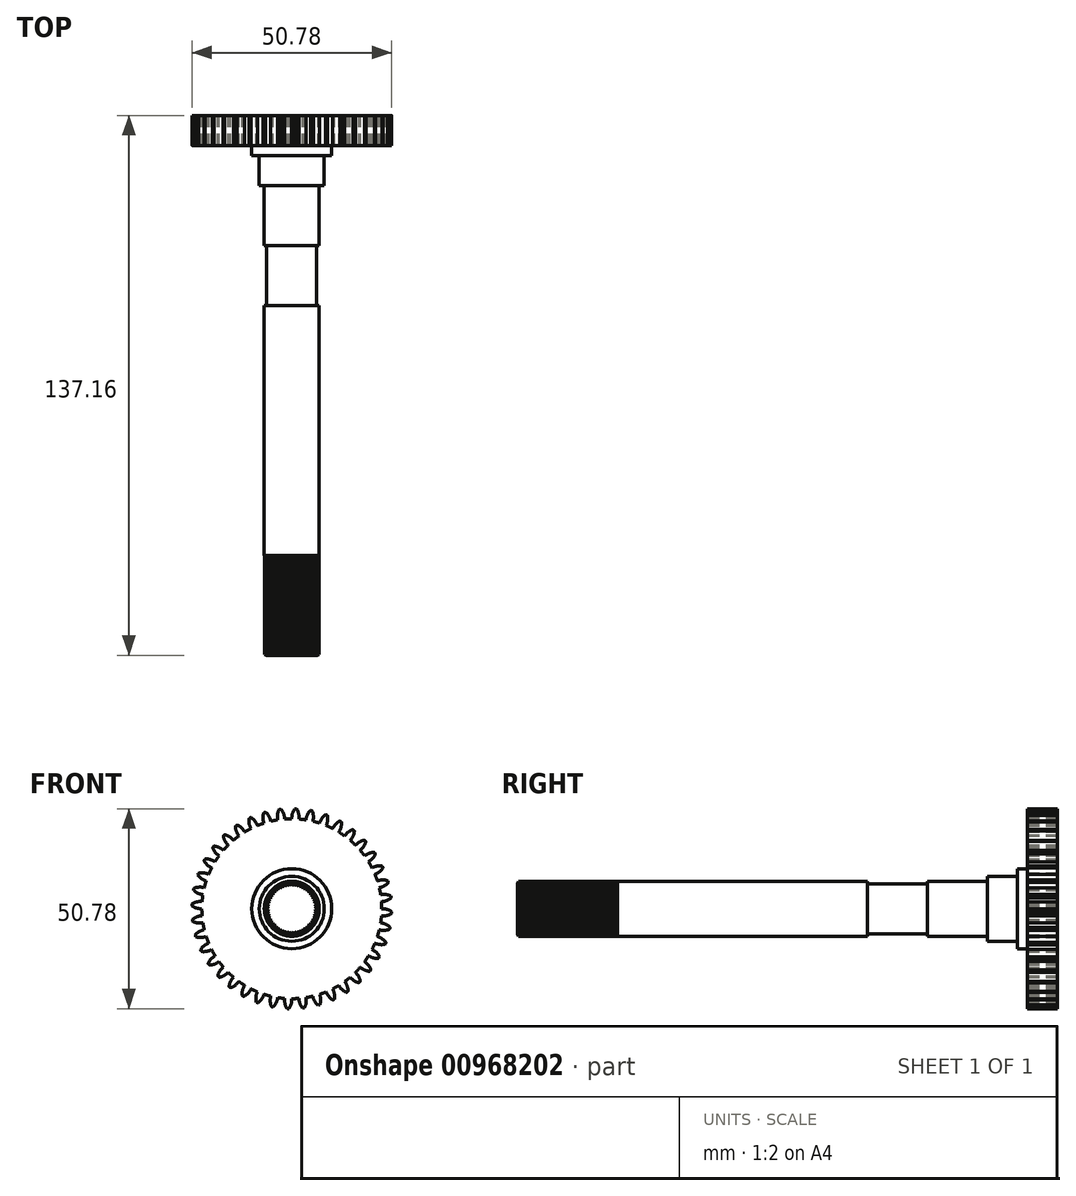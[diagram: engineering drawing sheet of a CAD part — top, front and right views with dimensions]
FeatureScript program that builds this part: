
annotation { "Feature Type Name" : "Feature", "Feature Type Description" : "" }
export const myFeature = defineFeature(function(context is Context, id is Id, definition is map)
    precondition{}
    {
        {
            var Q0;
            Q0=qCreatedBy(makeId("Front.planeOp"),FACE);
            var sketch = newSketch(context, id + "F0", { "sketchPlane" : qUnion([Q0])});
            skArc(sketch, "E0", {"start": v(1.24, 25.37) * mm, "mid": v(1, 25.38) * mm, "end": v(0.75, 25.39) * mm});
            skArc(sketch, "E1", {"start": v(3.58, 22.58) * mm, "mid": v(1.8, 22.79) * mm, "end": v(0, 22.86) * mm});
            skLineSegment(sketch, "E2", {"start": v(0, 0) * mm, "end": v(3.58, 22.58) * mm});
            skLineSegment(sketch, "E3", {"start": v(0, 0) * mm, "end": v(0, 23.2) * mm});
            skLineSegment(sketch, "E4", {"start": v(0, 0) * mm, "end": v(1.82, 23.13) * mm});
            skArc(sketch, "E5", {"start": v(0.75, 25.39) * mm, "mid": v(0.16, 24.19) * mm, "end": v(0, 22.86) * mm});
            skArc(sketch, "E6", {"start": v(1.8, 22.79) * mm, "mid": v(1.73, 24.13) * mm, "end": v(1.24, 25.37) * mm});
            skLineSegment(sketch, "E7.1.0", {"start": v(0, 0) * mm, "end": v(-1.82, 23.13) * mm});
            skLineSegment(sketch, "E7.1.1", {"start": v(0, 0) * mm, "end": v(-3.63, 22.92) * mm});
            skLineSegment(sketch, "E7.1.2", {"start": v(0, 0) * mm, "end": v(0, 22.86) * mm});
            skArc(sketch, "E7.1.3", {"start": v(0, 22.86) * mm, "mid": v(-1.8, 22.79) * mm, "end": v(-3.58, 22.58) * mm});
            skArc(sketch, "E7.1.4", {"start": v(-1.8, 22.79) * mm, "mid": v(-2.06, 24.1) * mm, "end": v(-2.74, 25.25) * mm});
            skArc(sketch, "E7.1.5", {"start": v(-3.23, 25.2) * mm, "mid": v(-3.62, 23.91) * mm, "end": v(-3.58, 22.58) * mm});
            skArc(sketch, "E7.1.6", {"start": v(-2.74, 25.25) * mm, "mid": v(-2.99, 25.22) * mm, "end": v(-3.23, 25.2) * mm});
            skLineSegment(sketch, "E7.2.0", {"start": v(0, 0) * mm, "end": v(-5.42, 22.56) * mm});
            skLineSegment(sketch, "E7.2.1", {"start": v(0, 0) * mm, "end": v(-7.17, 22.07) * mm});
            skLineSegment(sketch, "E7.2.2", {"start": v(0, 0) * mm, "end": v(-3.58, 22.58) * mm});
            skArc(sketch, "E7.2.3", {"start": v(-3.58, 22.58) * mm, "mid": v(-5.34, 22.23) * mm, "end": v(-7.06, 21.74) * mm});
            skArc(sketch, "E7.2.4", {"start": v(-5.34, 22.23) * mm, "mid": v(-5.8, 23.48) * mm, "end": v(-6.66, 24.51) * mm});
            skArc(sketch, "E7.2.5", {"start": v(-7.13, 24.38) * mm, "mid": v(-7.32, 23.05) * mm, "end": v(-7.06, 21.74) * mm});
            skArc(sketch, "E7.2.6", {"start": v(-6.66, 24.51) * mm, "mid": v(-6.9, 24.45) * mm, "end": v(-7.13, 24.38) * mm});
            skLineSegment(sketch, "E7.3.0", {"start": v(0, 0) * mm, "end": v(-8.88, 21.44) * mm});
            skLineSegment(sketch, "E7.3.1", {"start": v(0, 0) * mm, "end": v(-10.53, 20.67) * mm});
            skLineSegment(sketch, "E7.3.2", {"start": v(0, 0) * mm, "end": v(-7.06, 21.74) * mm});
            skArc(sketch, "E7.3.3", {"start": v(-7.06, 21.74) * mm, "mid": v(-8.75, 21.12) * mm, "end": v(-10.38, 20.37) * mm});
            skArc(sketch, "E7.3.4", {"start": v(-8.75, 21.12) * mm, "mid": v(-9.4, 22.28) * mm, "end": v(-10.4, 23.17) * mm});
            skArc(sketch, "E7.3.5", {"start": v(-10.86, 22.96) * mm, "mid": v(-10.83, 21.63) * mm, "end": v(-10.38, 20.37) * mm});
            skArc(sketch, "E7.3.6", {"start": v(-10.4, 23.17) * mm, "mid": v(-10.63, 23.07) * mm, "end": v(-10.86, 22.96) * mm});
            skLineSegment(sketch, "E7.4.0", {"start": v(0, 0) * mm, "end": v(-12.12, 19.78) * mm});
            skLineSegment(sketch, "E7.4.1", {"start": v(0, 0) * mm, "end": v(-13.64, 18.77) * mm});
            skLineSegment(sketch, "E7.4.2", {"start": v(0, 0) * mm, "end": v(-10.38, 20.37) * mm});
            skArc(sketch, "E7.4.3", {"start": v(-10.38, 20.37) * mm, "mid": v(-11.94, 19.5) * mm, "end": v(-13.44, 18.5) * mm});
            skArc(sketch, "E7.4.4", {"start": v(-11.94, 19.5) * mm, "mid": v(-12.78, 20.54) * mm, "end": v(-13.9, 21.26) * mm});
            skArc(sketch, "E7.4.5", {"start": v(-14.32, 20.98) * mm, "mid": v(-14.08, 19.66) * mm, "end": v(-13.44, 18.5) * mm});
            skArc(sketch, "E7.4.6", {"start": v(-13.9, 21.26) * mm, "mid": v(-14.11, 21.12) * mm, "end": v(-14.32, 20.98) * mm});
            skLineSegment(sketch, "E7.5.0", {"start": v(0, 0) * mm, "end": v(-15.07, 17.64) * mm});
            skLineSegment(sketch, "E7.5.1", {"start": v(0, 0) * mm, "end": v(-16.4, 16.4) * mm});
            skLineSegment(sketch, "E7.5.2", {"start": v(0, 0) * mm, "end": v(-13.44, 18.5) * mm});
            skArc(sketch, "E7.5.3", {"start": v(-13.44, 18.5) * mm, "mid": v(-14.85, 17.38) * mm, "end": v(-16.16, 16.16) * mm});
            skArc(sketch, "E7.5.4", {"start": v(-14.85, 17.38) * mm, "mid": v(-15.83, 18.29) * mm, "end": v(-17.06, 18.82) * mm});
            skArc(sketch, "E7.5.5", {"start": v(-17.42, 18.48) * mm, "mid": v(-16.99, 17.22) * mm, "end": v(-16.16, 16.16) * mm});
            skArc(sketch, "E7.5.6", {"start": v(-17.06, 18.82) * mm, "mid": v(-17.24, 18.65) * mm, "end": v(-17.42, 18.48) * mm});
            skLineSegment(sketch, "E7.6.0", {"start": v(0, 0) * mm, "end": v(-17.64, 15.07) * mm});
            skLineSegment(sketch, "E7.6.1", {"start": v(0, 0) * mm, "end": v(-18.77, 13.64) * mm});
            skLineSegment(sketch, "E7.6.2", {"start": v(0, 0) * mm, "end": v(-16.16, 16.16) * mm});
            skArc(sketch, "E7.6.3", {"start": v(-16.16, 16.16) * mm, "mid": v(-17.38, 14.85) * mm, "end": v(-18.5, 13.44) * mm});
            skArc(sketch, "E7.6.4", {"start": v(-17.38, 14.85) * mm, "mid": v(-18.5, 15.58) * mm, "end": v(-19.8, 15.92) * mm});
            skArc(sketch, "E7.6.5", {"start": v(-20.1, 15.53) * mm, "mid": v(-19.47, 14.35) * mm, "end": v(-18.5, 13.44) * mm});
            skArc(sketch, "E7.6.6", {"start": v(-19.8, 15.92) * mm, "mid": v(-19.95, 15.72) * mm, "end": v(-20.1, 15.53) * mm});
            skLineSegment(sketch, "E7.7.0", {"start": v(0, 0) * mm, "end": v(-19.78, 12.12) * mm});
            skLineSegment(sketch, "E7.7.1", {"start": v(0, 0) * mm, "end": v(-20.67, 10.53) * mm});
            skLineSegment(sketch, "E7.7.2", {"start": v(0, 0) * mm, "end": v(-18.5, 13.44) * mm});
            skArc(sketch, "E7.7.3", {"start": v(-18.5, 13.44) * mm, "mid": v(-19.5, 11.94) * mm, "end": v(-20.37, 10.38) * mm});
            skArc(sketch, "E7.7.4", {"start": v(-19.5, 11.94) * mm, "mid": v(-20.7, 12.5) * mm, "end": v(-22.04, 12.63) * mm});
            skArc(sketch, "E7.7.5", {"start": v(-22.28, 12.2) * mm, "mid": v(-21.48, 11.13) * mm, "end": v(-20.37, 10.38) * mm});
            skArc(sketch, "E7.7.6", {"start": v(-22.04, 12.63) * mm, "mid": v(-22.16, 12.41) * mm, "end": v(-22.28, 12.2) * mm});
            skLineSegment(sketch, "E7.8.0", {"start": v(0, 0) * mm, "end": v(-21.44, 8.88) * mm});
            skLineSegment(sketch, "E7.8.1", {"start": v(0, 0) * mm, "end": v(-22.07, 7.17) * mm});
            skLineSegment(sketch, "E7.8.2", {"start": v(0, 0) * mm, "end": v(-20.37, 10.38) * mm});
            skArc(sketch, "E7.8.3", {"start": v(-20.37, 10.38) * mm, "mid": v(-21.12, 8.75) * mm, "end": v(-21.74, 7.06) * mm});
            skArc(sketch, "E7.8.4", {"start": v(-21.12, 8.75) * mm, "mid": v(-22.4, 9.1) * mm, "end": v(-23.74, 9.02) * mm});
            skArc(sketch, "E7.8.5", {"start": v(-23.91, 8.56) * mm, "mid": v(-22.95, 7.63) * mm, "end": v(-21.74, 7.06) * mm});
            skArc(sketch, "E7.8.6", {"start": v(-23.74, 9.02) * mm, "mid": v(-23.83, 8.8) * mm, "end": v(-23.91, 8.56) * mm});
            skLineSegment(sketch, "E7.9.0", {"start": v(0, 0) * mm, "end": v(-22.56, 5.42) * mm});
            skLineSegment(sketch, "E7.9.1", {"start": v(0, 0) * mm, "end": v(-22.92, 3.63) * mm});
            skLineSegment(sketch, "E7.9.2", {"start": v(0, 0) * mm, "end": v(-21.74, 7.06) * mm});
            skArc(sketch, "E7.9.3", {"start": v(-21.74, 7.06) * mm, "mid": v(-22.23, 5.34) * mm, "end": v(-22.58, 3.58) * mm});
            skArc(sketch, "E7.9.4", {"start": v(-22.23, 5.34) * mm, "mid": v(-23.56, 5.49) * mm, "end": v(-24.86, 5.2) * mm});
            skArc(sketch, "E7.9.5", {"start": v(-24.96, 4.71) * mm, "mid": v(-23.86, 3.95) * mm, "end": v(-22.58, 3.58) * mm});
            skArc(sketch, "E7.9.6", {"start": v(-24.86, 5.2) * mm, "mid": v(-24.91, 4.96) * mm, "end": v(-24.96, 4.71) * mm});
            skLineSegment(sketch, "E7.10.0", {"start": v(0, 0) * mm, "end": v(-23.13, 1.82) * mm});
            skLineSegment(sketch, "E7.10.1", {"start": v(0, 0) * mm, "end": v(-23.2, 0) * mm});
            skLineSegment(sketch, "E7.10.2", {"start": v(0, 0) * mm, "end": v(-22.58, 3.58) * mm});
            skArc(sketch, "E7.10.3", {"start": v(-22.58, 3.58) * mm, "mid": v(-22.79, 1.8) * mm, "end": v(-22.86, 0) * mm});
            skArc(sketch, "E7.10.4", {"start": v(-22.79, 1.8) * mm, "mid": v(-24.13, 1.73) * mm, "end": v(-25.37, 1.24) * mm});
            skArc(sketch, "E7.10.5", {"start": v(-25.39, 0.75) * mm, "mid": v(-24.19, 0.16) * mm, "end": v(-22.86, 0) * mm});
            skArc(sketch, "E7.10.6", {"start": v(-25.37, 1.24) * mm, "mid": v(-25.38, 1) * mm, "end": v(-25.39, 0.75) * mm});
            skLineSegment(sketch, "E7.11.0", {"start": v(0, 0) * mm, "end": v(-23.13, -1.82) * mm});
            skLineSegment(sketch, "E7.11.1", {"start": v(0, 0) * mm, "end": v(-22.92, -3.63) * mm});
            skLineSegment(sketch, "E7.11.2", {"start": v(0, 0) * mm, "end": v(-22.86, 0) * mm});
            skArc(sketch, "E7.11.3", {"start": v(-22.86, 0) * mm, "mid": v(-22.79, -1.8) * mm, "end": v(-22.58, -3.58) * mm});
            skArc(sketch, "E7.11.4", {"start": v(-22.79, -1.8) * mm, "mid": v(-24.1, -2.06) * mm, "end": v(-25.25, -2.74) * mm});
            skArc(sketch, "E7.11.5", {"start": v(-25.2, -3.23) * mm, "mid": v(-23.91, -3.62) * mm, "end": v(-22.58, -3.58) * mm});
            skArc(sketch, "E7.11.6", {"start": v(-25.25, -2.74) * mm, "mid": v(-25.22, -2.99) * mm, "end": v(-25.2, -3.23) * mm});
            skLineSegment(sketch, "E7.12.0", {"start": v(0, 0) * mm, "end": v(-22.56, -5.42) * mm});
            skLineSegment(sketch, "E7.12.1", {"start": v(0, 0) * mm, "end": v(-22.07, -7.17) * mm});
            skLineSegment(sketch, "E7.12.2", {"start": v(0, 0) * mm, "end": v(-22.58, -3.58) * mm});
            skArc(sketch, "E7.12.3", {"start": v(-22.58, -3.58) * mm, "mid": v(-22.23, -5.34) * mm, "end": v(-21.74, -7.06) * mm});
            skArc(sketch, "E7.12.4", {"start": v(-22.23, -5.34) * mm, "mid": v(-23.48, -5.8) * mm, "end": v(-24.51, -6.66) * mm});
            skArc(sketch, "E7.12.5", {"start": v(-24.38, -7.13) * mm, "mid": v(-23.05, -7.32) * mm, "end": v(-21.74, -7.06) * mm});
            skArc(sketch, "E7.12.6", {"start": v(-24.51, -6.66) * mm, "mid": v(-24.45, -6.9) * mm, "end": v(-24.38, -7.13) * mm});
            skLineSegment(sketch, "E7.13.0", {"start": v(0, 0) * mm, "end": v(-21.44, -8.88) * mm});
            skLineSegment(sketch, "E7.13.1", {"start": v(0, 0) * mm, "end": v(-20.67, -10.53) * mm});
            skLineSegment(sketch, "E7.13.2", {"start": v(0, 0) * mm, "end": v(-21.74, -7.06) * mm});
            skArc(sketch, "E7.13.3", {"start": v(-21.74, -7.06) * mm, "mid": v(-21.12, -8.75) * mm, "end": v(-20.37, -10.38) * mm});
            skArc(sketch, "E7.13.4", {"start": v(-21.12, -8.75) * mm, "mid": v(-22.28, -9.4) * mm, "end": v(-23.17, -10.4) * mm});
            skArc(sketch, "E7.13.5", {"start": v(-22.96, -10.86) * mm, "mid": v(-21.63, -10.83) * mm, "end": v(-20.37, -10.38) * mm});
            skArc(sketch, "E7.13.6", {"start": v(-23.17, -10.4) * mm, "mid": v(-23.07, -10.63) * mm, "end": v(-22.96, -10.86) * mm});
            skLineSegment(sketch, "E7.14.0", {"start": v(0, 0) * mm, "end": v(-19.78, -12.12) * mm});
            skLineSegment(sketch, "E7.14.1", {"start": v(0, 0) * mm, "end": v(-18.77, -13.64) * mm});
            skLineSegment(sketch, "E7.14.2", {"start": v(0, 0) * mm, "end": v(-20.37, -10.38) * mm});
            skArc(sketch, "E7.14.3", {"start": v(-20.37, -10.38) * mm, "mid": v(-19.5, -11.94) * mm, "end": v(-18.5, -13.44) * mm});
            skArc(sketch, "E7.14.4", {"start": v(-19.5, -11.94) * mm, "mid": v(-20.54, -12.78) * mm, "end": v(-21.26, -13.9) * mm});
            skArc(sketch, "E7.14.5", {"start": v(-20.98, -14.32) * mm, "mid": v(-19.66, -14.08) * mm, "end": v(-18.5, -13.44) * mm});
            skArc(sketch, "E7.14.6", {"start": v(-21.26, -13.9) * mm, "mid": v(-21.12, -14.11) * mm, "end": v(-20.98, -14.32) * mm});
            skLineSegment(sketch, "E7.15.0", {"start": v(0, 0) * mm, "end": v(-17.64, -15.07) * mm});
            skLineSegment(sketch, "E7.15.1", {"start": v(0, 0) * mm, "end": v(-16.4, -16.4) * mm});
            skLineSegment(sketch, "E7.15.2", {"start": v(0, 0) * mm, "end": v(-18.5, -13.44) * mm});
            skArc(sketch, "E7.15.3", {"start": v(-18.5, -13.44) * mm, "mid": v(-17.38, -14.85) * mm, "end": v(-16.16, -16.16) * mm});
            skArc(sketch, "E7.15.4", {"start": v(-17.38, -14.85) * mm, "mid": v(-18.29, -15.83) * mm, "end": v(-18.82, -17.06) * mm});
            skArc(sketch, "E7.15.5", {"start": v(-18.48, -17.42) * mm, "mid": v(-17.22, -16.99) * mm, "end": v(-16.16, -16.16) * mm});
            skArc(sketch, "E7.15.6", {"start": v(-18.82, -17.06) * mm, "mid": v(-18.65, -17.24) * mm, "end": v(-18.48, -17.42) * mm});
            skLineSegment(sketch, "E7.16.0", {"start": v(0, 0) * mm, "end": v(-15.07, -17.64) * mm});
            skLineSegment(sketch, "E7.16.1", {"start": v(0, 0) * mm, "end": v(-13.64, -18.77) * mm});
            skLineSegment(sketch, "E7.16.2", {"start": v(0, 0) * mm, "end": v(-16.16, -16.16) * mm});
            skArc(sketch, "E7.16.3", {"start": v(-16.16, -16.16) * mm, "mid": v(-14.85, -17.38) * mm, "end": v(-13.44, -18.5) * mm});
            skArc(sketch, "E7.16.4", {"start": v(-14.85, -17.38) * mm, "mid": v(-15.58, -18.5) * mm, "end": v(-15.92, -19.8) * mm});
            skArc(sketch, "E7.16.5", {"start": v(-15.53, -20.1) * mm, "mid": v(-14.35, -19.47) * mm, "end": v(-13.44, -18.5) * mm});
            skArc(sketch, "E7.16.6", {"start": v(-15.92, -19.8) * mm, "mid": v(-15.72, -19.95) * mm, "end": v(-15.53, -20.1) * mm});
            skLineSegment(sketch, "E7.17.0", {"start": v(0, 0) * mm, "end": v(-12.12, -19.78) * mm});
            skLineSegment(sketch, "E7.17.1", {"start": v(0, 0) * mm, "end": v(-10.53, -20.67) * mm});
            skLineSegment(sketch, "E7.17.2", {"start": v(0, 0) * mm, "end": v(-13.44, -18.5) * mm});
            skArc(sketch, "E7.17.3", {"start": v(-13.44, -18.5) * mm, "mid": v(-11.94, -19.5) * mm, "end": v(-10.38, -20.37) * mm});
            skArc(sketch, "E7.17.4", {"start": v(-11.94, -19.5) * mm, "mid": v(-12.5, -20.7) * mm, "end": v(-12.63, -22.04) * mm});
            skArc(sketch, "E7.17.5", {"start": v(-12.2, -22.28) * mm, "mid": v(-11.13, -21.48) * mm, "end": v(-10.38, -20.37) * mm});
            skArc(sketch, "E7.17.6", {"start": v(-12.63, -22.04) * mm, "mid": v(-12.41, -22.16) * mm, "end": v(-12.2, -22.28) * mm});
            skLineSegment(sketch, "E7.18.0", {"start": v(0, 0) * mm, "end": v(-8.88, -21.44) * mm});
            skLineSegment(sketch, "E7.18.1", {"start": v(0, 0) * mm, "end": v(-7.17, -22.07) * mm});
            skLineSegment(sketch, "E7.18.2", {"start": v(0, 0) * mm, "end": v(-10.38, -20.37) * mm});
            skArc(sketch, "E7.18.3", {"start": v(-10.38, -20.37) * mm, "mid": v(-8.75, -21.12) * mm, "end": v(-7.06, -21.74) * mm});
            skArc(sketch, "E7.18.4", {"start": v(-8.75, -21.12) * mm, "mid": v(-9.1, -22.4) * mm, "end": v(-9.02, -23.74) * mm});
            skArc(sketch, "E7.18.5", {"start": v(-8.56, -23.91) * mm, "mid": v(-7.63, -22.95) * mm, "end": v(-7.06, -21.74) * mm});
            skArc(sketch, "E7.18.6", {"start": v(-9.02, -23.74) * mm, "mid": v(-8.8, -23.83) * mm, "end": v(-8.56, -23.91) * mm});
            skLineSegment(sketch, "E7.19.0", {"start": v(0, 0) * mm, "end": v(-5.42, -22.56) * mm});
            skLineSegment(sketch, "E7.19.1", {"start": v(0, 0) * mm, "end": v(-3.63, -22.92) * mm});
            skLineSegment(sketch, "E7.19.2", {"start": v(0, 0) * mm, "end": v(-7.06, -21.74) * mm});
            skArc(sketch, "E7.19.3", {"start": v(-7.06, -21.74) * mm, "mid": v(-5.34, -22.23) * mm, "end": v(-3.58, -22.58) * mm});
            skArc(sketch, "E7.19.4", {"start": v(-5.34, -22.23) * mm, "mid": v(-5.49, -23.56) * mm, "end": v(-5.2, -24.86) * mm});
            skArc(sketch, "E7.19.5", {"start": v(-4.71, -24.96) * mm, "mid": v(-3.95, -23.86) * mm, "end": v(-3.58, -22.58) * mm});
            skArc(sketch, "E7.19.6", {"start": v(-5.2, -24.86) * mm, "mid": v(-4.96, -24.91) * mm, "end": v(-4.71, -24.96) * mm});
            skLineSegment(sketch, "E7.20.0", {"start": v(0, 0) * mm, "end": v(-1.82, -23.13) * mm});
            skLineSegment(sketch, "E7.20.1", {"start": v(0, 0) * mm, "end": v(0, -23.2) * mm});
            skLineSegment(sketch, "E7.20.2", {"start": v(0, 0) * mm, "end": v(-3.58, -22.58) * mm});
            skArc(sketch, "E7.20.3", {"start": v(-3.58, -22.58) * mm, "mid": v(-1.8, -22.79) * mm, "end": v(0, -22.86) * mm});
            skArc(sketch, "E7.20.4", {"start": v(-1.8, -22.79) * mm, "mid": v(-1.73, -24.13) * mm, "end": v(-1.24, -25.37) * mm});
            skArc(sketch, "E7.20.5", {"start": v(-0.75, -25.39) * mm, "mid": v(-0.16, -24.19) * mm, "end": v(0, -22.86) * mm});
            skArc(sketch, "E7.20.6", {"start": v(-1.24, -25.37) * mm, "mid": v(-1, -25.38) * mm, "end": v(-0.75, -25.39) * mm});
            skLineSegment(sketch, "E7.21.0", {"start": v(0, 0) * mm, "end": v(1.82, -23.13) * mm});
            skLineSegment(sketch, "E7.21.1", {"start": v(0, 0) * mm, "end": v(3.63, -22.92) * mm});
            skLineSegment(sketch, "E7.21.2", {"start": v(0, 0) * mm, "end": v(0, -22.86) * mm});
            skArc(sketch, "E7.21.3", {"start": v(0, -22.86) * mm, "mid": v(1.8, -22.79) * mm, "end": v(3.58, -22.58) * mm});
            skArc(sketch, "E7.21.4", {"start": v(1.8, -22.79) * mm, "mid": v(2.06, -24.1) * mm, "end": v(2.74, -25.25) * mm});
            skArc(sketch, "E7.21.5", {"start": v(3.23, -25.2) * mm, "mid": v(3.62, -23.91) * mm, "end": v(3.58, -22.58) * mm});
            skArc(sketch, "E7.21.6", {"start": v(2.74, -25.25) * mm, "mid": v(2.99, -25.22) * mm, "end": v(3.23, -25.2) * mm});
            skLineSegment(sketch, "E7.22.0", {"start": v(0, 0) * mm, "end": v(5.42, -22.56) * mm});
            skLineSegment(sketch, "E7.22.1", {"start": v(0, 0) * mm, "end": v(7.17, -22.07) * mm});
            skLineSegment(sketch, "E7.22.2", {"start": v(0, 0) * mm, "end": v(3.58, -22.58) * mm});
            skArc(sketch, "E7.22.3", {"start": v(3.58, -22.58) * mm, "mid": v(5.34, -22.23) * mm, "end": v(7.06, -21.74) * mm});
            skArc(sketch, "E7.22.4", {"start": v(5.34, -22.23) * mm, "mid": v(5.8, -23.48) * mm, "end": v(6.66, -24.51) * mm});
            skArc(sketch, "E7.22.5", {"start": v(7.13, -24.38) * mm, "mid": v(7.32, -23.05) * mm, "end": v(7.06, -21.74) * mm});
            skArc(sketch, "E7.22.6", {"start": v(6.66, -24.51) * mm, "mid": v(6.9, -24.45) * mm, "end": v(7.13, -24.38) * mm});
            skLineSegment(sketch, "E7.23.0", {"start": v(0, 0) * mm, "end": v(8.88, -21.44) * mm});
            skLineSegment(sketch, "E7.23.1", {"start": v(0, 0) * mm, "end": v(10.53, -20.67) * mm});
            skLineSegment(sketch, "E7.23.2", {"start": v(0, 0) * mm, "end": v(7.06, -21.74) * mm});
            skArc(sketch, "E7.23.3", {"start": v(7.06, -21.74) * mm, "mid": v(8.75, -21.12) * mm, "end": v(10.38, -20.37) * mm});
            skArc(sketch, "E7.23.4", {"start": v(8.75, -21.12) * mm, "mid": v(9.4, -22.28) * mm, "end": v(10.4, -23.17) * mm});
            skArc(sketch, "E7.23.5", {"start": v(10.86, -22.96) * mm, "mid": v(10.83, -21.63) * mm, "end": v(10.38, -20.37) * mm});
            skArc(sketch, "E7.23.6", {"start": v(10.4, -23.17) * mm, "mid": v(10.63, -23.07) * mm, "end": v(10.86, -22.96) * mm});
            skLineSegment(sketch, "E7.24.0", {"start": v(0, 0) * mm, "end": v(12.12, -19.78) * mm});
            skLineSegment(sketch, "E7.24.1", {"start": v(0, 0) * mm, "end": v(13.64, -18.77) * mm});
            skLineSegment(sketch, "E7.24.2", {"start": v(0, 0) * mm, "end": v(10.38, -20.37) * mm});
            skArc(sketch, "E7.24.3", {"start": v(10.38, -20.37) * mm, "mid": v(11.94, -19.5) * mm, "end": v(13.44, -18.5) * mm});
            skArc(sketch, "E7.24.4", {"start": v(11.94, -19.5) * mm, "mid": v(12.78, -20.54) * mm, "end": v(13.9, -21.26) * mm});
            skArc(sketch, "E7.24.5", {"start": v(14.32, -20.98) * mm, "mid": v(14.08, -19.66) * mm, "end": v(13.44, -18.5) * mm});
            skArc(sketch, "E7.24.6", {"start": v(13.9, -21.26) * mm, "mid": v(14.11, -21.12) * mm, "end": v(14.32, -20.98) * mm});
            skLineSegment(sketch, "E7.25.0", {"start": v(0, 0) * mm, "end": v(15.07, -17.64) * mm});
            skLineSegment(sketch, "E7.25.1", {"start": v(0, 0) * mm, "end": v(16.4, -16.4) * mm});
            skLineSegment(sketch, "E7.25.2", {"start": v(0, 0) * mm, "end": v(13.44, -18.5) * mm});
            skArc(sketch, "E7.25.3", {"start": v(13.44, -18.5) * mm, "mid": v(14.85, -17.38) * mm, "end": v(16.16, -16.16) * mm});
            skArc(sketch, "E7.25.4", {"start": v(14.85, -17.38) * mm, "mid": v(15.83, -18.29) * mm, "end": v(17.06, -18.82) * mm});
            skArc(sketch, "E7.25.5", {"start": v(17.42, -18.48) * mm, "mid": v(16.99, -17.22) * mm, "end": v(16.16, -16.16) * mm});
            skArc(sketch, "E7.25.6", {"start": v(17.06, -18.82) * mm, "mid": v(17.24, -18.65) * mm, "end": v(17.42, -18.48) * mm});
            skLineSegment(sketch, "E7.26.0", {"start": v(0, 0) * mm, "end": v(17.64, -15.07) * mm});
            skLineSegment(sketch, "E7.26.1", {"start": v(0, 0) * mm, "end": v(18.77, -13.64) * mm});
            skLineSegment(sketch, "E7.26.2", {"start": v(0, 0) * mm, "end": v(16.16, -16.16) * mm});
            skArc(sketch, "E7.26.3", {"start": v(16.16, -16.16) * mm, "mid": v(17.38, -14.85) * mm, "end": v(18.5, -13.44) * mm});
            skArc(sketch, "E7.26.4", {"start": v(17.38, -14.85) * mm, "mid": v(18.5, -15.58) * mm, "end": v(19.8, -15.92) * mm});
            skArc(sketch, "E7.26.5", {"start": v(20.1, -15.53) * mm, "mid": v(19.47, -14.35) * mm, "end": v(18.5, -13.44) * mm});
            skArc(sketch, "E7.26.6", {"start": v(19.8, -15.92) * mm, "mid": v(19.95, -15.72) * mm, "end": v(20.1, -15.53) * mm});
            skLineSegment(sketch, "E7.27.0", {"start": v(0, 0) * mm, "end": v(19.78, -12.12) * mm});
            skLineSegment(sketch, "E7.27.1", {"start": v(0, 0) * mm, "end": v(20.67, -10.53) * mm});
            skLineSegment(sketch, "E7.27.2", {"start": v(0, 0) * mm, "end": v(18.5, -13.44) * mm});
            skArc(sketch, "E7.27.3", {"start": v(18.5, -13.44) * mm, "mid": v(19.5, -11.94) * mm, "end": v(20.37, -10.38) * mm});
            skArc(sketch, "E7.27.4", {"start": v(19.5, -11.94) * mm, "mid": v(20.7, -12.5) * mm, "end": v(22.04, -12.63) * mm});
            skArc(sketch, "E7.27.5", {"start": v(22.28, -12.2) * mm, "mid": v(21.48, -11.13) * mm, "end": v(20.37, -10.38) * mm});
            skArc(sketch, "E7.27.6", {"start": v(22.04, -12.63) * mm, "mid": v(22.16, -12.41) * mm, "end": v(22.28, -12.2) * mm});
            skLineSegment(sketch, "E7.28.0", {"start": v(0, 0) * mm, "end": v(21.44, -8.88) * mm});
            skLineSegment(sketch, "E7.28.1", {"start": v(0, 0) * mm, "end": v(22.07, -7.17) * mm});
            skLineSegment(sketch, "E7.28.2", {"start": v(0, 0) * mm, "end": v(20.37, -10.38) * mm});
            skArc(sketch, "E7.28.3", {"start": v(20.37, -10.38) * mm, "mid": v(21.12, -8.75) * mm, "end": v(21.74, -7.06) * mm});
            skArc(sketch, "E7.28.4", {"start": v(21.12, -8.75) * mm, "mid": v(22.4, -9.1) * mm, "end": v(23.74, -9.02) * mm});
            skArc(sketch, "E7.28.5", {"start": v(23.91, -8.56) * mm, "mid": v(22.95, -7.63) * mm, "end": v(21.74, -7.06) * mm});
            skArc(sketch, "E7.28.6", {"start": v(23.74, -9.02) * mm, "mid": v(23.83, -8.8) * mm, "end": v(23.91, -8.56) * mm});
            skLineSegment(sketch, "E7.29.0", {"start": v(0, 0) * mm, "end": v(22.56, -5.42) * mm});
            skLineSegment(sketch, "E7.29.1", {"start": v(0, 0) * mm, "end": v(22.92, -3.63) * mm});
            skLineSegment(sketch, "E7.29.2", {"start": v(0, 0) * mm, "end": v(21.74, -7.06) * mm});
            skArc(sketch, "E7.29.3", {"start": v(21.74, -7.06) * mm, "mid": v(22.23, -5.34) * mm, "end": v(22.58, -3.58) * mm});
            skArc(sketch, "E7.29.4", {"start": v(22.23, -5.34) * mm, "mid": v(23.56, -5.49) * mm, "end": v(24.86, -5.2) * mm});
            skArc(sketch, "E7.29.5", {"start": v(24.96, -4.71) * mm, "mid": v(23.86, -3.95) * mm, "end": v(22.58, -3.58) * mm});
            skArc(sketch, "E7.29.6", {"start": v(24.86, -5.2) * mm, "mid": v(24.91, -4.96) * mm, "end": v(24.96, -4.71) * mm});
            skLineSegment(sketch, "E7.30.0", {"start": v(0, 0) * mm, "end": v(23.13, -1.82) * mm});
            skLineSegment(sketch, "E7.30.1", {"start": v(0, 0) * mm, "end": v(23.2, 0) * mm});
            skLineSegment(sketch, "E7.30.2", {"start": v(0, 0) * mm, "end": v(22.58, -3.58) * mm});
            skArc(sketch, "E7.30.3", {"start": v(22.58, -3.58) * mm, "mid": v(22.79, -1.8) * mm, "end": v(22.86, 0) * mm});
            skArc(sketch, "E7.30.4", {"start": v(22.79, -1.8) * mm, "mid": v(24.13, -1.73) * mm, "end": v(25.37, -1.24) * mm});
            skArc(sketch, "E7.30.5", {"start": v(25.39, -0.75) * mm, "mid": v(24.19, -0.16) * mm, "end": v(22.86, 0) * mm});
            skArc(sketch, "E7.30.6", {"start": v(25.37, -1.24) * mm, "mid": v(25.38, -1) * mm, "end": v(25.39, -0.75) * mm});
            skLineSegment(sketch, "E7.31.0", {"start": v(0, 0) * mm, "end": v(23.13, 1.82) * mm});
            skLineSegment(sketch, "E7.31.1", {"start": v(0, 0) * mm, "end": v(22.92, 3.63) * mm});
            skLineSegment(sketch, "E7.31.2", {"start": v(0, 0) * mm, "end": v(22.86, 0) * mm});
            skArc(sketch, "E7.31.3", {"start": v(22.86, 0) * mm, "mid": v(22.79, 1.8) * mm, "end": v(22.58, 3.58) * mm});
            skArc(sketch, "E7.31.4", {"start": v(22.79, 1.8) * mm, "mid": v(24.1, 2.06) * mm, "end": v(25.25, 2.74) * mm});
            skArc(sketch, "E7.31.5", {"start": v(25.2, 3.23) * mm, "mid": v(23.91, 3.62) * mm, "end": v(22.58, 3.58) * mm});
            skArc(sketch, "E7.31.6", {"start": v(25.25, 2.74) * mm, "mid": v(25.22, 2.99) * mm, "end": v(25.2, 3.23) * mm});
            skLineSegment(sketch, "E7.32.0", {"start": v(0, 0) * mm, "end": v(22.56, 5.42) * mm});
            skLineSegment(sketch, "E7.32.1", {"start": v(0, 0) * mm, "end": v(22.07, 7.17) * mm});
            skLineSegment(sketch, "E7.32.2", {"start": v(0, 0) * mm, "end": v(22.58, 3.58) * mm});
            skArc(sketch, "E7.32.3", {"start": v(22.58, 3.58) * mm, "mid": v(22.23, 5.34) * mm, "end": v(21.74, 7.06) * mm});
            skArc(sketch, "E7.32.4", {"start": v(22.23, 5.34) * mm, "mid": v(23.48, 5.8) * mm, "end": v(24.51, 6.66) * mm});
            skArc(sketch, "E7.32.5", {"start": v(24.38, 7.13) * mm, "mid": v(23.05, 7.32) * mm, "end": v(21.74, 7.06) * mm});
            skArc(sketch, "E7.32.6", {"start": v(24.51, 6.66) * mm, "mid": v(24.45, 6.9) * mm, "end": v(24.38, 7.13) * mm});
            skLineSegment(sketch, "E7.33.0", {"start": v(0, 0) * mm, "end": v(21.44, 8.88) * mm});
            skLineSegment(sketch, "E7.33.1", {"start": v(0, 0) * mm, "end": v(20.67, 10.53) * mm});
            skLineSegment(sketch, "E7.33.2", {"start": v(0, 0) * mm, "end": v(21.74, 7.06) * mm});
            skArc(sketch, "E7.33.3", {"start": v(21.74, 7.06) * mm, "mid": v(21.12, 8.75) * mm, "end": v(20.37, 10.38) * mm});
            skArc(sketch, "E7.33.4", {"start": v(21.12, 8.75) * mm, "mid": v(22.28, 9.4) * mm, "end": v(23.17, 10.4) * mm});
            skArc(sketch, "E7.33.5", {"start": v(22.96, 10.86) * mm, "mid": v(21.63, 10.83) * mm, "end": v(20.37, 10.38) * mm});
            skArc(sketch, "E7.33.6", {"start": v(23.17, 10.4) * mm, "mid": v(23.07, 10.63) * mm, "end": v(22.96, 10.86) * mm});
            skLineSegment(sketch, "E7.34.0", {"start": v(0, 0) * mm, "end": v(19.78, 12.12) * mm});
            skLineSegment(sketch, "E7.34.1", {"start": v(0, 0) * mm, "end": v(18.77, 13.64) * mm});
            skLineSegment(sketch, "E7.34.2", {"start": v(0, 0) * mm, "end": v(20.37, 10.38) * mm});
            skArc(sketch, "E7.34.3", {"start": v(20.37, 10.38) * mm, "mid": v(19.5, 11.94) * mm, "end": v(18.5, 13.44) * mm});
            skArc(sketch, "E7.34.4", {"start": v(19.5, 11.94) * mm, "mid": v(20.54, 12.78) * mm, "end": v(21.26, 13.9) * mm});
            skArc(sketch, "E7.34.5", {"start": v(20.98, 14.32) * mm, "mid": v(19.66, 14.08) * mm, "end": v(18.5, 13.44) * mm});
            skArc(sketch, "E7.34.6", {"start": v(21.26, 13.9) * mm, "mid": v(21.12, 14.11) * mm, "end": v(20.98, 14.32) * mm});
            skLineSegment(sketch, "E7.35.0", {"start": v(0, 0) * mm, "end": v(17.64, 15.07) * mm});
            skLineSegment(sketch, "E7.35.1", {"start": v(0, 0) * mm, "end": v(16.4, 16.4) * mm});
            skLineSegment(sketch, "E7.35.2", {"start": v(0, 0) * mm, "end": v(18.5, 13.44) * mm});
            skArc(sketch, "E7.35.3", {"start": v(18.5, 13.44) * mm, "mid": v(17.38, 14.85) * mm, "end": v(16.16, 16.16) * mm});
            skArc(sketch, "E7.35.4", {"start": v(17.38, 14.85) * mm, "mid": v(18.29, 15.83) * mm, "end": v(18.82, 17.06) * mm});
            skArc(sketch, "E7.35.5", {"start": v(18.48, 17.42) * mm, "mid": v(17.22, 16.99) * mm, "end": v(16.16, 16.16) * mm});
            skArc(sketch, "E7.35.6", {"start": v(18.82, 17.06) * mm, "mid": v(18.65, 17.24) * mm, "end": v(18.48, 17.42) * mm});
            skLineSegment(sketch, "E7.36.0", {"start": v(0, 0) * mm, "end": v(15.07, 17.64) * mm});
            skLineSegment(sketch, "E7.36.1", {"start": v(0, 0) * mm, "end": v(13.64, 18.77) * mm});
            skLineSegment(sketch, "E7.36.2", {"start": v(0, 0) * mm, "end": v(16.16, 16.16) * mm});
            skArc(sketch, "E7.36.3", {"start": v(16.16, 16.16) * mm, "mid": v(14.85, 17.38) * mm, "end": v(13.44, 18.5) * mm});
            skArc(sketch, "E7.36.4", {"start": v(14.85, 17.38) * mm, "mid": v(15.58, 18.5) * mm, "end": v(15.92, 19.8) * mm});
            skArc(sketch, "E7.36.5", {"start": v(15.53, 20.1) * mm, "mid": v(14.35, 19.47) * mm, "end": v(13.44, 18.5) * mm});
            skArc(sketch, "E7.36.6", {"start": v(15.92, 19.8) * mm, "mid": v(15.72, 19.95) * mm, "end": v(15.53, 20.1) * mm});
            skLineSegment(sketch, "E7.37.0", {"start": v(0, 0) * mm, "end": v(12.12, 19.78) * mm});
            skLineSegment(sketch, "E7.37.1", {"start": v(0, 0) * mm, "end": v(10.53, 20.67) * mm});
            skLineSegment(sketch, "E7.37.2", {"start": v(0, 0) * mm, "end": v(13.44, 18.5) * mm});
            skArc(sketch, "E7.37.3", {"start": v(13.44, 18.5) * mm, "mid": v(11.94, 19.5) * mm, "end": v(10.38, 20.37) * mm});
            skArc(sketch, "E7.37.4", {"start": v(11.94, 19.5) * mm, "mid": v(12.5, 20.7) * mm, "end": v(12.63, 22.04) * mm});
            skArc(sketch, "E7.37.5", {"start": v(12.2, 22.28) * mm, "mid": v(11.13, 21.48) * mm, "end": v(10.38, 20.37) * mm});
            skArc(sketch, "E7.37.6", {"start": v(12.63, 22.04) * mm, "mid": v(12.41, 22.16) * mm, "end": v(12.2, 22.28) * mm});
            skLineSegment(sketch, "E7.38.0", {"start": v(0, 0) * mm, "end": v(8.88, 21.44) * mm});
            skLineSegment(sketch, "E7.38.1", {"start": v(0, 0) * mm, "end": v(7.17, 22.07) * mm});
            skLineSegment(sketch, "E7.38.2", {"start": v(0, 0) * mm, "end": v(10.38, 20.37) * mm});
            skArc(sketch, "E7.38.3", {"start": v(10.38, 20.37) * mm, "mid": v(8.75, 21.12) * mm, "end": v(7.06, 21.74) * mm});
            skArc(sketch, "E7.38.4", {"start": v(8.75, 21.12) * mm, "mid": v(9.1, 22.4) * mm, "end": v(9.02, 23.74) * mm});
            skArc(sketch, "E7.38.5", {"start": v(8.56, 23.91) * mm, "mid": v(7.63, 22.95) * mm, "end": v(7.06, 21.74) * mm});
            skArc(sketch, "E7.38.6", {"start": v(9.02, 23.74) * mm, "mid": v(8.8, 23.83) * mm, "end": v(8.56, 23.91) * mm});
            skLineSegment(sketch, "E7.39.0", {"start": v(0, 0) * mm, "end": v(5.42, 22.56) * mm});
            skLineSegment(sketch, "E7.39.1", {"start": v(0, 0) * mm, "end": v(3.63, 22.92) * mm});
            skLineSegment(sketch, "E7.39.2", {"start": v(0, 0) * mm, "end": v(7.06, 21.74) * mm});
            skArc(sketch, "E7.39.3", {"start": v(7.06, 21.74) * mm, "mid": v(5.34, 22.23) * mm, "end": v(3.58, 22.58) * mm});
            skArc(sketch, "E7.39.4", {"start": v(5.34, 22.23) * mm, "mid": v(5.49, 23.56) * mm, "end": v(5.2, 24.86) * mm});
            skArc(sketch, "E7.39.5", {"start": v(4.71, 24.96) * mm, "mid": v(3.95, 23.86) * mm, "end": v(3.58, 22.58) * mm});
            skArc(sketch, "E7.39.6", {"start": v(5.2, 24.86) * mm, "mid": v(4.96, 24.91) * mm, "end": v(4.71, 24.96) * mm});
            skSolve(sketch);
        }
        {
            var Q0;
            {var subQ0=sQuery(id+"F0.wireOp",EDGE,"E7.39.0");var subQ1=sQuery(id+"F0.wireOp",EDGE,"E7.38.1");var subQ2=sQuery(id+"F0.wireOp",EDGE,"E7.38.0");var subQ3=sQuery(id+"F0.wireOp",EDGE,"E7.37.1");var subQ4=sQuery(id+"F0.wireOp",EDGE,"E7.37.0");var subQ5=sQuery(id+"F0.wireOp",EDGE,"E7.36.1");var subQ6=sQuery(id+"F0.wireOp",EDGE,"E7.36.0");var subQ7=sQuery(id+"F0.wireOp",EDGE,"E7.35.1");var subQ8=sQuery(id+"F0.wireOp",EDGE,"E7.35.0");var subQ9=sQuery(id+"F0.wireOp",EDGE,"E7.34.1");var subQ10=sQuery(id+"F0.wireOp",EDGE,"E7.34.0");var subQ11=sQuery(id+"F0.wireOp",EDGE,"E7.33.1");var subQ12=sQuery(id+"F0.wireOp",EDGE,"E7.33.0");var subQ13=sQuery(id+"F0.wireOp",EDGE,"E7.32.1");var subQ14=sQuery(id+"F0.wireOp",EDGE,"E7.32.0");var subQ15=sQuery(id+"F0.wireOp",EDGE,"E7.31.1");var subQ16=sQuery(id+"F0.wireOp",EDGE,"E7.31.0");var subQ17=sQuery(id+"F0.wireOp",EDGE,"E7.30.1");var subQ18=sQuery(id+"F0.wireOp",EDGE,"E7.30.0");var subQ19=sQuery(id+"F0.wireOp",EDGE,"E7.29.1");var subQ20=sQuery(id+"F0.wireOp",EDGE,"E7.29.0");var subQ21=sQuery(id+"F0.wireOp",EDGE,"E7.28.1");var subQ22=sQuery(id+"F0.wireOp",EDGE,"E7.28.0");var subQ23=sQuery(id+"F0.wireOp",EDGE,"E7.27.1");var subQ24=sQuery(id+"F0.wireOp",EDGE,"E7.27.0");var subQ25=sQuery(id+"F0.wireOp",EDGE,"E7.26.1");var subQ26=sQuery(id+"F0.wireOp",EDGE,"E7.26.0");var subQ27=sQuery(id+"F0.wireOp",EDGE,"E7.25.1");var subQ28=sQuery(id+"F0.wireOp",EDGE,"E7.25.0");var subQ29=sQuery(id+"F0.wireOp",EDGE,"E7.24.1");var subQ30=sQuery(id+"F0.wireOp",EDGE,"E7.24.0");var subQ31=sQuery(id+"F0.wireOp",EDGE,"E7.23.1");var subQ32=sQuery(id+"F0.wireOp",EDGE,"E7.23.0");var subQ33=sQuery(id+"F0.wireOp",EDGE,"E7.22.1");var subQ34=sQuery(id+"F0.wireOp",EDGE,"E7.22.0");var subQ35=sQuery(id+"F0.wireOp",EDGE,"E7.21.1");var subQ36=sQuery(id+"F0.wireOp",EDGE,"E7.21.0");var subQ37=sQuery(id+"F0.wireOp",EDGE,"E7.20.1");var subQ38=sQuery(id+"F0.wireOp",EDGE,"E7.20.0");var subQ39=sQuery(id+"F0.wireOp",EDGE,"E7.19.1");var subQ40=sQuery(id+"F0.wireOp",EDGE,"E7.19.0");var subQ41=sQuery(id+"F0.wireOp",EDGE,"E7.18.1");var subQ42=sQuery(id+"F0.wireOp",EDGE,"E7.18.0");var subQ43=sQuery(id+"F0.wireOp",EDGE,"E7.17.1");var subQ44=sQuery(id+"F0.wireOp",EDGE,"E7.17.0");var subQ45=sQuery(id+"F0.wireOp",EDGE,"E7.16.1");var subQ46=sQuery(id+"F0.wireOp",EDGE,"E7.16.0");var subQ47=sQuery(id+"F0.wireOp",EDGE,"E7.15.1");var subQ48=sQuery(id+"F0.wireOp",EDGE,"E7.15.0");var subQ49=sQuery(id+"F0.wireOp",EDGE,"E7.14.1");var subQ50=sQuery(id+"F0.wireOp",EDGE,"E7.14.0");var subQ51=sQuery(id+"F0.wireOp",EDGE,"E7.13.1");var subQ52=sQuery(id+"F0.wireOp",EDGE,"E7.13.0");var subQ53=sQuery(id+"F0.wireOp",EDGE,"E7.12.1");var subQ54=sQuery(id+"F0.wireOp",EDGE,"E7.12.0");var subQ55=sQuery(id+"F0.wireOp",EDGE,"E7.11.1");var subQ56=sQuery(id+"F0.wireOp",EDGE,"E7.11.0");var subQ57=sQuery(id+"F0.wireOp",EDGE,"E7.10.1");var subQ58=sQuery(id+"F0.wireOp",EDGE,"E7.10.0");var subQ59=sQuery(id+"F0.wireOp",EDGE,"E7.9.1");var subQ60=sQuery(id+"F0.wireOp",EDGE,"E7.9.0");var subQ61=sQuery(id+"F0.wireOp",EDGE,"E7.8.1");var subQ62=sQuery(id+"F0.wireOp",EDGE,"E7.8.0");var subQ63=sQuery(id+"F0.wireOp",EDGE,"E7.7.1");var subQ64=sQuery(id+"F0.wireOp",EDGE,"E7.7.0");var subQ65=sQuery(id+"F0.wireOp",EDGE,"E7.6.1");var subQ66=sQuery(id+"F0.wireOp",EDGE,"E7.6.0");var subQ67=sQuery(id+"F0.wireOp",EDGE,"E7.5.1");var subQ68=sQuery(id+"F0.wireOp",EDGE,"E7.5.0");var subQ69=sQuery(id+"F0.wireOp",EDGE,"E7.4.1");var subQ70=sQuery(id+"F0.wireOp",EDGE,"E7.4.0");var subQ71=sQuery(id+"F0.wireOp",EDGE,"E7.3.1");var subQ72=sQuery(id+"F0.wireOp",EDGE,"E7.3.0");var subQ73=sQuery(id+"F0.wireOp",EDGE,"E7.2.1");var subQ74=sQuery(id+"F0.wireOp",EDGE,"E7.2.0");var subQ75=sQuery(id+"F0.wireOp",EDGE,"E7.1.1");var subQ76=sQuery(id+"F0.wireOp",EDGE,"E7.1.0");var subQ77=sQuery(id+"F0.wireOp",EDGE,"E4");var subQ78=sQuery(id+"F0.wireOp",EDGE,"E3");var subQ79=sQuery(id+"F0.wireOp",EDGE,"E2");var subQ81=sQuery(id+"F0.wireOp",EDGE,"E7.27.4");var subQ82=sQuery(id+"F0.wireOp",EDGE,"E7.27.3");var subQ83=makeQuery(id+"F0.imprint","INTERSECT",VERTEX,{"derivedFrom":[subQ24,subQ82,subQ81]});var subQ85=sQuery(id+"F0.wireOp",EDGE,"E7.28.3");var subQ86=sQuery(id+"F0.wireOp",EDGE,"E7.27.5");var subQ88=makeQuery(id+"F0.imprint","IMPRINT",EDGE,{"disambiguationData":[TD([[subQ83,-1.0]])],"derivedFrom":subQ82});var subQ90=sQuery(id+"F0.wireOp",EDGE,"E7.35.4");var subQ91=sQuery(id+"F0.wireOp",EDGE,"E7.35.3");var subQ92=makeQuery(id+"F0.imprint","INTERSECT",VERTEX,{"derivedFrom":[subQ8,subQ91,subQ90]});var subQ94=sQuery(id+"F0.wireOp",EDGE,"E7.36.3");var subQ95=sQuery(id+"F0.wireOp",EDGE,"E7.35.5");var subQ97=makeQuery(id+"F0.imprint","IMPRINT",EDGE,{"disambiguationData":[TD([[subQ92,-1.0]])],"derivedFrom":subQ91});var subQ99=sQuery(id+"F0.wireOp",EDGE,"E7.8.4");var subQ100=sQuery(id+"F0.wireOp",EDGE,"E7.8.3");var subQ101=makeQuery(id+"F0.imprint","INTERSECT",VERTEX,{"derivedFrom":[subQ62,subQ100,subQ99]});var subQ103=sQuery(id+"F0.wireOp",EDGE,"E7.9.3");var subQ104=sQuery(id+"F0.wireOp",EDGE,"E7.8.5");var subQ106=makeQuery(id+"F0.imprint","IMPRINT",EDGE,{"disambiguationData":[TD([[subQ101,-1.0]])],"derivedFrom":subQ100});var subQ108=sQuery(id+"F0.wireOp",EDGE,"E7.31.3");var subQ109=sQuery(id+"F0.wireOp",EDGE,"E7.30.5");var subQ110=sQuery(id+"F0.wireOp",EDGE,"E7.30.3");var subQ113=sQuery(id+"F0.wireOp",EDGE,"E7.31.4");var subQ114=makeQuery(id+"F0.imprint","INTERSECT",VERTEX,{"derivedFrom":[subQ16,subQ108,subQ113]});var subQ116=sQuery(id+"F0.wireOp",EDGE,"E7.16.4");var subQ117=sQuery(id+"F0.wireOp",EDGE,"E7.16.3");var subQ118=makeQuery(id+"F0.imprint","INTERSECT",VERTEX,{"derivedFrom":[subQ46,subQ117,subQ116]});var subQ120=sQuery(id+"F0.wireOp",EDGE,"E7.17.3");var subQ121=sQuery(id+"F0.wireOp",EDGE,"E7.16.5");var subQ123=makeQuery(id+"F0.imprint","IMPRINT",EDGE,{"disambiguationData":[TD([[subQ118,-1.0]])],"derivedFrom":subQ117});var subQ125=sQuery(id+"F0.wireOp",EDGE,"E7.3.4");var subQ126=sQuery(id+"F0.wireOp",EDGE,"E7.3.3");var subQ127=makeQuery(id+"F0.imprint","INTERSECT",VERTEX,{"derivedFrom":[subQ72,subQ126,subQ125]});var subQ129=sQuery(id+"F0.wireOp",EDGE,"E7.4.3");var subQ130=sQuery(id+"F0.wireOp",EDGE,"E7.3.5");var subQ132=makeQuery(id+"F0.imprint","IMPRINT",EDGE,{"disambiguationData":[TD([[subQ127,-1.0]])],"derivedFrom":subQ126});var subQ134=sQuery(id+"F0.wireOp",EDGE,"E7.24.4");var subQ135=sQuery(id+"F0.wireOp",EDGE,"E7.24.3");var subQ136=makeQuery(id+"F0.imprint","INTERSECT",VERTEX,{"derivedFrom":[subQ30,subQ135,subQ134]});var subQ138=sQuery(id+"F0.wireOp",EDGE,"E7.25.3");var subQ139=sQuery(id+"F0.wireOp",EDGE,"E7.24.5");var subQ141=makeQuery(id+"F0.imprint","IMPRINT",EDGE,{"disambiguationData":[TD([[subQ136,-1.0]])],"derivedFrom":subQ135});var subQ143=sQuery(id+"F0.wireOp",EDGE,"E7.11.4");var subQ144=sQuery(id+"F0.wireOp",EDGE,"E7.11.3");var subQ145=makeQuery(id+"F0.imprint","INTERSECT",VERTEX,{"derivedFrom":[subQ56,subQ144,subQ143]});var subQ147=sQuery(id+"F0.wireOp",EDGE,"E7.12.3");var subQ148=sQuery(id+"F0.wireOp",EDGE,"E7.11.5");var subQ150=makeQuery(id+"F0.imprint","IMPRINT",EDGE,{"disambiguationData":[TD([[subQ145,-1.0]])],"derivedFrom":subQ144});var subQ152=sQuery(id+"F0.wireOp",EDGE,"E7.32.4");var subQ153=sQuery(id+"F0.wireOp",EDGE,"E7.32.3");var subQ154=makeQuery(id+"F0.imprint","INTERSECT",VERTEX,{"derivedFrom":[subQ14,subQ153,subQ152]});var subQ156=sQuery(id+"F0.wireOp",EDGE,"E7.33.3");var subQ157=sQuery(id+"F0.wireOp",EDGE,"E7.32.5");var subQ159=makeQuery(id+"F0.imprint","IMPRINT",EDGE,{"disambiguationData":[TD([[subQ154,-1.0]])],"derivedFrom":subQ153});var subQ161=sQuery(id+"F0.wireOp",EDGE,"E7.19.4");var subQ162=sQuery(id+"F0.wireOp",EDGE,"E7.19.3");var subQ163=makeQuery(id+"F0.imprint","INTERSECT",VERTEX,{"derivedFrom":[subQ40,subQ162,subQ161]});var subQ165=sQuery(id+"F0.wireOp",EDGE,"E7.20.3");var subQ166=sQuery(id+"F0.wireOp",EDGE,"E7.19.5");var subQ168=makeQuery(id+"F0.imprint","IMPRINT",EDGE,{"disambiguationData":[TD([[subQ163,-1.0]])],"derivedFrom":subQ162});var subQ170=sQuery(id+"F0.wireOp",EDGE,"E7.36.5");var subQ171=makeQuery(id+"F0.imprint","INTERSECT",VERTEX,{"derivedFrom":[subQ5,subQ170]});var subQ172=sQuery(id+"F0.wireOp",EDGE,"E7.37.3");var subQ174=makeQuery(id+"F0.imprint","IMPRINT",EDGE,{"disambiguationData":[TD([[subQ171,1.0]])],"derivedFrom":subQ5});var subQ175=sQuery(id+"F0.wireOp",EDGE,"E7.23.5");var subQ176=makeQuery(id+"F0.imprint","INTERSECT",VERTEX,{"derivedFrom":[subQ31,subQ175]});var subQ177=sQuery(id+"F0.wireOp",EDGE,"E7.23.3");var subQ179=makeQuery(id+"F0.imprint","IMPRINT",EDGE,{"disambiguationData":[TD([[subQ176,1.0]])],"derivedFrom":subQ31});var subQ180=sQuery(id+"F0.wireOp",EDGE,"E7.9.4");var subQ181=makeQuery(id+"F0.imprint","INTERSECT",VERTEX,{"derivedFrom":[subQ60,subQ103,subQ180]});var subQ183=sQuery(id+"F0.wireOp",EDGE,"E7.31.5");var subQ184=makeQuery(id+"F0.imprint","INTERSECT",VERTEX,{"derivedFrom":[subQ15,subQ183]});var subQ186=makeQuery(id+"F0.imprint","IMPRINT",EDGE,{"disambiguationData":[TD([[subQ184,1.0]])],"derivedFrom":subQ15});var subQ187=sQuery(id+"F0.wireOp",EDGE,"E7.25.4");var subQ188=makeQuery(id+"F0.imprint","INTERSECT",VERTEX,{"derivedFrom":[subQ28,subQ138,subQ187]});var subQ190=sQuery(id+"F0.wireOp",EDGE,"E7.39.1");var subQ191=makeQuery(id+"F0.imprint","IMPRINT",EDGE,{"derivedFrom":subQ190});var subQ193=sQuery(id+"F0.wireOp",EDGE,"E7.39.3");var subQ194=sQuery(id+"F0.wireOp",EDGE,"E1");var subQ197=sQuery(id+"F0.wireOp",EDGE,"E7.1.3");var subQ198=sQuery(id+"F0.wireOp",EDGE,"E5");var subQ200=sQuery(id+"F0.wireOp",EDGE,"E6");var subQ201=makeQuery(id+"F0.imprint","INTERSECT",VERTEX,{"derivedFrom":[subQ194,subQ77,subQ200]});var subQ202=makeQuery(id+"F0.imprint","IMPRINT",EDGE,{"disambiguationData":[TD([[subQ201,-1.0]])],"derivedFrom":subQ194});var subQ205=sQuery(id+"F0.wireOp",EDGE,"E7.15.3");var subQ206=sQuery(id+"F0.wireOp",EDGE,"E7.14.5");var subQ207=sQuery(id+"F0.wireOp",EDGE,"E7.14.3");var subQ210=sQuery(id+"F0.wireOp",EDGE,"E7.15.4");var subQ211=makeQuery(id+"F0.imprint","INTERSECT",VERTEX,{"derivedFrom":[subQ48,subQ205,subQ210]});var subQ213=sQuery(id+"F0.wireOp",EDGE,"E7.12.5");var subQ214=makeQuery(id+"F0.imprint","INTERSECT",VERTEX,{"derivedFrom":[subQ53,subQ213]});var subQ215=sQuery(id+"F0.wireOp",EDGE,"E7.13.3");var subQ217=makeQuery(id+"F0.imprint","IMPRINT",EDGE,{"disambiguationData":[TD([[subQ214,1.0]])],"derivedFrom":subQ53});var subQ218=sQuery(id+"F0.wireOp",EDGE,"E7.20.5");var subQ219=makeQuery(id+"F0.imprint","INTERSECT",VERTEX,{"derivedFrom":[subQ37,subQ218]});var subQ220=sQuery(id+"F0.wireOp",EDGE,"E7.21.3");var subQ222=makeQuery(id+"F0.imprint","IMPRINT",EDGE,{"disambiguationData":[TD([[subQ219,1.0]])],"derivedFrom":subQ37});var subQ223=sQuery(id+"F0.wireOp",EDGE,"E7.28.5");var subQ224=makeQuery(id+"F0.imprint","INTERSECT",VERTEX,{"derivedFrom":[subQ21,subQ223]});var subQ225=sQuery(id+"F0.wireOp",EDGE,"E7.29.3");var subQ227=makeQuery(id+"F0.imprint","IMPRINT",EDGE,{"disambiguationData":[TD([[subQ224,1.0]])],"derivedFrom":subQ21});var subQ228=sQuery(id+"F0.wireOp",EDGE,"E7.15.5");var subQ229=makeQuery(id+"F0.imprint","INTERSECT",VERTEX,{"derivedFrom":[subQ47,subQ228]});var subQ231=makeQuery(id+"F0.imprint","IMPRINT",EDGE,{"disambiguationData":[TD([[subQ229,1.0]])],"derivedFrom":subQ47});var subQ232=sQuery(id+"F0.wireOp",EDGE,"E7.20.4");var subQ233=makeQuery(id+"F0.imprint","INTERSECT",VERTEX,{"derivedFrom":[subQ38,subQ232]});var subQ234=sQuery(id+"F0.wireOp",EDGE,"E7.20.6");var subQ235=makeQuery(id+"F0.imprint","INTERSECT",VERTEX,{"derivedFrom":[subQ38,subQ165,subQ232]});var subQ236=makeQuery(id+"F0.imprint","IMPRINT",EDGE,{"disambiguationData":[TD([[subQ235,-1.0]])],"derivedFrom":subQ165});var subQ237=makeQuery(id+"F0.imprint","IMPRINT",EDGE,{"disambiguationData":[TD([[subQ233,1.0]])],"derivedFrom":subQ38});var subQ238=sQuery(id+"F0.wireOp",EDGE,"E7.28.4");var subQ239=makeQuery(id+"F0.imprint","INTERSECT",VERTEX,{"derivedFrom":[subQ22,subQ238]});var subQ240=sQuery(id+"F0.wireOp",EDGE,"E7.28.6");var subQ241=makeQuery(id+"F0.imprint","INTERSECT",VERTEX,{"derivedFrom":[subQ22,subQ85,subQ238]});var subQ242=makeQuery(id+"F0.imprint","IMPRINT",EDGE,{"disambiguationData":[TD([[subQ241,-1.0]])],"derivedFrom":subQ85});var subQ243=makeQuery(id+"F0.imprint","IMPRINT",EDGE,{"disambiguationData":[TD([[subQ239,1.0]])],"derivedFrom":subQ22});var subQ244=sQuery(id+"F0.wireOp",EDGE,"E7.36.4");var subQ245=makeQuery(id+"F0.imprint","INTERSECT",VERTEX,{"derivedFrom":[subQ6,subQ244]});var subQ246=sQuery(id+"F0.wireOp",EDGE,"E7.36.6");var subQ247=makeQuery(id+"F0.imprint","INTERSECT",VERTEX,{"derivedFrom":[subQ6,subQ94,subQ244]});var subQ248=makeQuery(id+"F0.imprint","IMPRINT",EDGE,{"disambiguationData":[TD([[subQ247,-1.0]])],"derivedFrom":subQ94});var subQ249=makeQuery(id+"F0.imprint","IMPRINT",EDGE,{"disambiguationData":[TD([[subQ245,1.0]])],"derivedFrom":subQ6});var subQ250=sQuery(id+"F0.wireOp",EDGE,"E7.18.3");var subQ251=sQuery(id+"F0.wireOp",EDGE,"E7.17.5");var subQ254=sQuery(id+"F0.wireOp",EDGE,"E7.18.4");var subQ255=makeQuery(id+"F0.imprint","INTERSECT",VERTEX,{"derivedFrom":[subQ42,subQ250,subQ254]});var subQ257=sQuery(id+"F0.wireOp",EDGE,"E7.34.3");var subQ258=sQuery(id+"F0.wireOp",EDGE,"E7.33.5");var subQ261=sQuery(id+"F0.wireOp",EDGE,"E7.34.4");var subQ262=makeQuery(id+"F0.imprint","INTERSECT",VERTEX,{"derivedFrom":[subQ10,subQ257,subQ261]});var subQ264=sQuery(id+"F0.wireOp",EDGE,"E7.4.4");var subQ265=makeQuery(id+"F0.imprint","INTERSECT",VERTEX,{"derivedFrom":[subQ70,subQ264]});var subQ266=sQuery(id+"F0.wireOp",EDGE,"E7.4.6");var subQ267=sQuery(id+"F0.wireOp",EDGE,"E7.5.3");var subQ268=sQuery(id+"F0.wireOp",EDGE,"E7.4.5");var subQ270=makeQuery(id+"F0.imprint","INTERSECT",VERTEX,{"derivedFrom":[subQ70,subQ129,subQ264]});var subQ271=makeQuery(id+"F0.imprint","IMPRINT",EDGE,{"disambiguationData":[TD([[subQ270,-1.0]])],"derivedFrom":subQ129});var subQ272=makeQuery(id+"F0.imprint","INTERSECT",VERTEX,{"derivedFrom":[subQ69,subQ268]});var subQ273=makeQuery(id+"F0.imprint","IMPRINT",EDGE,{"disambiguationData":[TD([[subQ272,1.0]])],"derivedFrom":subQ69});var subQ274=makeQuery(id+"F0.imprint","IMPRINT",EDGE,{"disambiguationData":[TD([[subQ265,1.0]])],"derivedFrom":subQ70});var subQ275=sQuery(id+"F0.wireOp",EDGE,"E7.12.4");var subQ276=makeQuery(id+"F0.imprint","INTERSECT",VERTEX,{"derivedFrom":[subQ54,subQ275]});var subQ277=sQuery(id+"F0.wireOp",EDGE,"E7.12.6");var subQ278=makeQuery(id+"F0.imprint","INTERSECT",VERTEX,{"derivedFrom":[subQ54,subQ147,subQ275]});var subQ279=makeQuery(id+"F0.imprint","IMPRINT",EDGE,{"disambiguationData":[TD([[subQ278,-1.0]])],"derivedFrom":subQ147});var subQ280=makeQuery(id+"F0.imprint","IMPRINT",EDGE,{"disambiguationData":[TD([[subQ276,1.0]])],"derivedFrom":subQ54});var subQ281=sQuery(id+"F0.wireOp",EDGE,"E7.17.4");var subQ282=makeQuery(id+"F0.imprint","INTERSECT",VERTEX,{"derivedFrom":[subQ44,subQ281]});var subQ283=makeQuery(id+"F0.imprint","INTERSECT",VERTEX,{"derivedFrom":[subQ44,subQ120,subQ281]});var subQ284=makeQuery(id+"F0.imprint","IMPRINT",EDGE,{"disambiguationData":[TD([[subQ282,1.0]])],"derivedFrom":subQ44});var subQ285=makeQuery(id+"F0.imprint","INTERSECT",VERTEX,{"derivedFrom":[subQ28,subQ187]});var subQ286=makeQuery(id+"F0.imprint","IMPRINT",EDGE,{"disambiguationData":[TD([[subQ285,1.0]])],"derivedFrom":subQ28});var subQ287=sQuery(id+"F0.wireOp",EDGE,"E7.33.4");var subQ288=makeQuery(id+"F0.imprint","INTERSECT",VERTEX,{"derivedFrom":[subQ12,subQ287]});var subQ289=makeQuery(id+"F0.imprint","INTERSECT",VERTEX,{"derivedFrom":[subQ12,subQ156,subQ287]});var subQ290=makeQuery(id+"F0.imprint","IMPRINT",EDGE,{"disambiguationData":[TD([[subQ288,1.0]])],"derivedFrom":subQ12});var subQ291=sQuery(id+"F0.wireOp",EDGE,"E7.2.3");var subQ292=sQuery(id+"F0.wireOp",EDGE,"E7.1.5");var subQ295=sQuery(id+"F0.wireOp",EDGE,"E7.2.4");var subQ296=makeQuery(id+"F0.imprint","INTERSECT",VERTEX,{"derivedFrom":[subQ74,subQ291,subQ295]});var subQ298=makeQuery(id+"F0.imprint","INTERSECT",VERTEX,{"derivedFrom":[subQ60,subQ180]});var subQ299=makeQuery(id+"F0.imprint","IMPRINT",EDGE,{"disambiguationData":[TD([[subQ298,1.0]])],"derivedFrom":subQ60});var subQ300=sQuery(id+"F0.wireOp",EDGE,"E7.7.4");var subQ301=makeQuery(id+"F0.imprint","INTERSECT",VERTEX,{"derivedFrom":[subQ64,subQ300]});var subQ302=sQuery(id+"F0.wireOp",EDGE,"E7.7.6");var subQ303=sQuery(id+"F0.wireOp",EDGE,"E7.7.5");var subQ304=sQuery(id+"F0.wireOp",EDGE,"E7.7.3");var subQ306=makeQuery(id+"F0.imprint","INTERSECT",VERTEX,{"derivedFrom":[subQ64,subQ304,subQ300]});var subQ307=makeQuery(id+"F0.imprint","IMPRINT",EDGE,{"disambiguationData":[TD([[subQ306,-1.0]])],"derivedFrom":subQ304});var subQ308=makeQuery(id+"F0.imprint","INTERSECT",VERTEX,{"derivedFrom":[subQ63,subQ303]});var subQ309=makeQuery(id+"F0.imprint","IMPRINT",EDGE,{"disambiguationData":[TD([[subQ308,1.0]])],"derivedFrom":subQ63});var subQ310=makeQuery(id+"F0.imprint","IMPRINT",EDGE,{"disambiguationData":[TD([[subQ301,1.0]])],"derivedFrom":subQ64});var subQ311=makeQuery(id+"F0.imprint","INTERSECT",VERTEX,{"derivedFrom":[subQ48,subQ210]});var subQ312=sQuery(id+"F0.wireOp",EDGE,"E7.15.6");var subQ313=makeQuery(id+"F0.imprint","IMPRINT",EDGE,{"disambiguationData":[TD([[subQ211,-1.0]])],"derivedFrom":subQ205});var subQ314=makeQuery(id+"F0.imprint","IMPRINT",EDGE,{"disambiguationData":[TD([[subQ311,1.0]])],"derivedFrom":subQ48});var subQ315=sQuery(id+"F0.wireOp",EDGE,"E7.23.4");var subQ316=makeQuery(id+"F0.imprint","INTERSECT",VERTEX,{"derivedFrom":[subQ32,subQ315]});var subQ317=sQuery(id+"F0.wireOp",EDGE,"E7.23.6");var subQ318=makeQuery(id+"F0.imprint","INTERSECT",VERTEX,{"derivedFrom":[subQ32,subQ177,subQ315]});var subQ319=makeQuery(id+"F0.imprint","IMPRINT",EDGE,{"disambiguationData":[TD([[subQ318,-1.0]])],"derivedFrom":subQ177});var subQ320=makeQuery(id+"F0.imprint","IMPRINT",EDGE,{"disambiguationData":[TD([[subQ316,1.0]])],"derivedFrom":subQ32});var subQ321=makeQuery(id+"F0.imprint","INTERSECT",VERTEX,{"derivedFrom":[subQ16,subQ113]});var subQ322=sQuery(id+"F0.wireOp",EDGE,"E7.31.6");var subQ323=makeQuery(id+"F0.imprint","IMPRINT",EDGE,{"disambiguationData":[TD([[subQ114,-1.0]])],"derivedFrom":subQ108});var subQ324=makeQuery(id+"F0.imprint","IMPRINT",EDGE,{"disambiguationData":[TD([[subQ321,1.0]])],"derivedFrom":subQ16});var subQ327=makeQuery(id+"F0.imprint","INTERSECT",VERTEX,{"derivedFrom":[subQ77,subQ200]});var subQ328=makeQuery(id+"F0.imprint","IMPRINT",EDGE,{"disambiguationData":[TD([[subQ327,1.0]])],"derivedFrom":subQ77});var subQ329=makeQuery(id+"F0.imprint","INTERSECT",VERTEX,{"derivedFrom":[subQ78,subQ198]});var subQ330=makeQuery(id+"F0.imprint","IMPRINT",EDGE,{"disambiguationData":[TD([[subQ329,1.0]])],"derivedFrom":subQ78});var subQ331=sQuery(id+"F0.wireOp",EDGE,"E0");var subQ332=sQuery(id+"F0.wireOp",EDGE,"E7.9.6");var subQ333=sQuery(id+"F0.wireOp",EDGE,"E7.10.3");var subQ334=sQuery(id+"F0.wireOp",EDGE,"E7.9.5");var subQ336=makeQuery(id+"F0.imprint","IMPRINT",EDGE,{"disambiguationData":[TD([[subQ181,-1.0]])],"derivedFrom":subQ103});var subQ337=makeQuery(id+"F0.imprint","INTERSECT",VERTEX,{"derivedFrom":[subQ59,subQ334]});var subQ338=makeQuery(id+"F0.imprint","IMPRINT",EDGE,{"disambiguationData":[TD([[subQ337,1.0]])],"derivedFrom":subQ59});var subQ339=sQuery(id+"F0.wireOp",EDGE,"E7.17.6");var subQ340=makeQuery(id+"F0.imprint","IMPRINT",EDGE,{"disambiguationData":[TD([[subQ283,-1.0]])],"derivedFrom":subQ120});var subQ341=makeQuery(id+"F0.imprint","INTERSECT",VERTEX,{"derivedFrom":[subQ43,subQ251]});var subQ342=makeQuery(id+"F0.imprint","IMPRINT",EDGE,{"disambiguationData":[TD([[subQ341,1.0]])],"derivedFrom":subQ43});var subQ343=sQuery(id+"F0.wireOp",EDGE,"E7.25.6");var subQ344=sQuery(id+"F0.wireOp",EDGE,"E7.26.3");var subQ345=sQuery(id+"F0.wireOp",EDGE,"E7.25.5");var subQ347=makeQuery(id+"F0.imprint","IMPRINT",EDGE,{"disambiguationData":[TD([[subQ188,-1.0]])],"derivedFrom":subQ138});var subQ348=makeQuery(id+"F0.imprint","INTERSECT",VERTEX,{"derivedFrom":[subQ27,subQ345]});var subQ349=makeQuery(id+"F0.imprint","IMPRINT",EDGE,{"disambiguationData":[TD([[subQ348,1.0]])],"derivedFrom":subQ27});var subQ350=sQuery(id+"F0.wireOp",EDGE,"E7.33.6");var subQ351=makeQuery(id+"F0.imprint","IMPRINT",EDGE,{"disambiguationData":[TD([[subQ289,-1.0]])],"derivedFrom":subQ156});var subQ352=makeQuery(id+"F0.imprint","INTERSECT",VERTEX,{"derivedFrom":[subQ11,subQ258]});var subQ353=makeQuery(id+"F0.imprint","IMPRINT",EDGE,{"disambiguationData":[TD([[subQ352,1.0]])],"derivedFrom":subQ11});var subQ354=sQuery(id+"F0.wireOp",EDGE,"E7.38.4");var subQ355=makeQuery(id+"F0.imprint","INTERSECT",VERTEX,{"derivedFrom":[subQ2,subQ354]});var subQ356=sQuery(id+"F0.wireOp",EDGE,"E7.38.3");var subQ357=makeQuery(id+"F0.imprint","INTERSECT",VERTEX,{"derivedFrom":[subQ2,subQ356,subQ354]});var subQ358=makeQuery(id+"F0.imprint","IMPRINT",EDGE,{"disambiguationData":[TD([[subQ355,1.0]])],"derivedFrom":subQ2});var subQ361=sQuery(id+"F0.wireOp",EDGE,"E7.1.4");var subQ362=makeQuery(id+"F0.imprint","INTERSECT",VERTEX,{"derivedFrom":[subQ76,subQ361]});var subQ363=sQuery(id+"F0.wireOp",EDGE,"E7.1.6");var subQ364=makeQuery(id+"F0.imprint","INTERSECT",VERTEX,{"derivedFrom":[subQ76,subQ197,subQ361]});var subQ365=makeQuery(id+"F0.imprint","IMPRINT",EDGE,{"disambiguationData":[TD([[subQ364,-1.0]])],"derivedFrom":subQ197});var subQ366=makeQuery(id+"F0.imprint","INTERSECT",VERTEX,{"derivedFrom":[subQ75,subQ292]});var subQ367=makeQuery(id+"F0.imprint","IMPRINT",EDGE,{"disambiguationData":[TD([[subQ366,1.0]])],"derivedFrom":subQ75});var subQ368=makeQuery(id+"F0.imprint","IMPRINT",EDGE,{"disambiguationData":[TD([[subQ362,1.0]])],"derivedFrom":subQ76});var subQ369=sQuery(id+"F0.wireOp",EDGE,"E7.14.4");var subQ370=makeQuery(id+"F0.imprint","INTERSECT",VERTEX,{"derivedFrom":[subQ50,subQ369]});var subQ371=makeQuery(id+"F0.imprint","INTERSECT",VERTEX,{"derivedFrom":[subQ50,subQ207,subQ369]});var subQ372=makeQuery(id+"F0.imprint","IMPRINT",EDGE,{"disambiguationData":[TD([[subQ370,1.0]])],"derivedFrom":subQ50});var subQ373=sQuery(id+"F0.wireOp",EDGE,"E7.22.4");var subQ374=makeQuery(id+"F0.imprint","INTERSECT",VERTEX,{"derivedFrom":[subQ34,subQ373]});var subQ375=sQuery(id+"F0.wireOp",EDGE,"E7.22.3");var subQ376=makeQuery(id+"F0.imprint","INTERSECT",VERTEX,{"derivedFrom":[subQ34,subQ375,subQ373]});var subQ377=makeQuery(id+"F0.imprint","IMPRINT",EDGE,{"disambiguationData":[TD([[subQ374,1.0]])],"derivedFrom":subQ34});var subQ378=sQuery(id+"F0.wireOp",EDGE,"E7.30.4");var subQ379=makeQuery(id+"F0.imprint","INTERSECT",VERTEX,{"derivedFrom":[subQ18,subQ378]});var subQ380=makeQuery(id+"F0.imprint","INTERSECT",VERTEX,{"derivedFrom":[subQ18,subQ110,subQ378]});var subQ381=makeQuery(id+"F0.imprint","IMPRINT",EDGE,{"disambiguationData":[TD([[subQ379,1.0]])],"derivedFrom":subQ18});var subQ392=makeQuery(id+"F0.imprint","INTERSECT",VERTEX,{"derivedFrom":[subQ45,subQ121]});var subQ393=makeQuery(id+"F0.imprint","IMPRINT",EDGE,{"disambiguationData":[TD([[subQ392,1.0]])],"derivedFrom":subQ45});var subQ394=makeQuery(id+"F0.imprint","INTERSECT",VERTEX,{"derivedFrom":[subQ29,subQ139]});var subQ395=makeQuery(id+"F0.imprint","IMPRINT",EDGE,{"disambiguationData":[TD([[subQ394,1.0]])],"derivedFrom":subQ29});var subQ396=makeQuery(id+"F0.imprint","INTERSECT",VERTEX,{"derivedFrom":[subQ13,subQ157]});var subQ397=makeQuery(id+"F0.imprint","IMPRINT",EDGE,{"disambiguationData":[TD([[subQ396,1.0]])],"derivedFrom":subQ13});var subQ399=makeQuery(id+"F0.imprint","INTERSECT",VERTEX,{"derivedFrom":[subQ61,subQ104]});var subQ400=makeQuery(id+"F0.imprint","IMPRINT",EDGE,{"disambiguationData":[TD([[subQ399,1.0]])],"derivedFrom":subQ61});var subQ402=sQuery(id+"F0.wireOp",EDGE,"E7.22.5");var subQ404=makeQuery(id+"F0.imprint","IMPRINT",EDGE,{"disambiguationData":[TD([[subQ376,-1.0]])],"derivedFrom":subQ375});var subQ406=makeQuery(id+"F0.imprint","INTERSECT",VERTEX,{"derivedFrom":[subQ42,subQ254]});var subQ407=sQuery(id+"F0.wireOp",EDGE,"E7.18.6");var subQ408=sQuery(id+"F0.wireOp",EDGE,"E7.18.5");var subQ410=makeQuery(id+"F0.imprint","IMPRINT",EDGE,{"disambiguationData":[TD([[subQ255,-1.0]])],"derivedFrom":subQ250});var subQ411=makeQuery(id+"F0.imprint","INTERSECT",VERTEX,{"derivedFrom":[subQ41,subQ408]});var subQ412=makeQuery(id+"F0.imprint","IMPRINT",EDGE,{"disambiguationData":[TD([[subQ411,1.0]])],"derivedFrom":subQ41});var subQ413=makeQuery(id+"F0.imprint","IMPRINT",EDGE,{"disambiguationData":[TD([[subQ406,1.0]])],"derivedFrom":subQ42});var subQ415=makeQuery(id+"F0.imprint","IMPRINT",EDGE,{"disambiguationData":[TD([[subQ380,-1.0]])],"derivedFrom":subQ110});var subQ416=sQuery(id+"F0.wireOp",EDGE,"E7.26.4");var subQ417=makeQuery(id+"F0.imprint","INTERSECT",VERTEX,{"derivedFrom":[subQ26,subQ416]});var subQ418=sQuery(id+"F0.wireOp",EDGE,"E7.26.6");var subQ419=sQuery(id+"F0.wireOp",EDGE,"E7.26.5");var subQ421=makeQuery(id+"F0.imprint","INTERSECT",VERTEX,{"derivedFrom":[subQ26,subQ344,subQ416]});var subQ422=makeQuery(id+"F0.imprint","IMPRINT",EDGE,{"disambiguationData":[TD([[subQ421,-1.0]])],"derivedFrom":subQ344});var subQ423=makeQuery(id+"F0.imprint","INTERSECT",VERTEX,{"derivedFrom":[subQ25,subQ419]});var subQ424=makeQuery(id+"F0.imprint","IMPRINT",EDGE,{"disambiguationData":[TD([[subQ423,1.0]])],"derivedFrom":subQ25});var subQ425=makeQuery(id+"F0.imprint","IMPRINT",EDGE,{"disambiguationData":[TD([[subQ417,1.0]])],"derivedFrom":subQ26});var subQ427=sQuery(id+"F0.wireOp",EDGE,"E7.38.5");var subQ429=makeQuery(id+"F0.imprint","IMPRINT",EDGE,{"disambiguationData":[TD([[subQ357,-1.0]])],"derivedFrom":subQ356});var subQ431=makeQuery(id+"F0.imprint","INTERSECT",VERTEX,{"derivedFrom":[subQ10,subQ261]});var subQ432=sQuery(id+"F0.wireOp",EDGE,"E7.34.6");var subQ433=sQuery(id+"F0.wireOp",EDGE,"E7.34.5");var subQ435=makeQuery(id+"F0.imprint","IMPRINT",EDGE,{"disambiguationData":[TD([[subQ262,-1.0]])],"derivedFrom":subQ257});var subQ436=makeQuery(id+"F0.imprint","INTERSECT",VERTEX,{"derivedFrom":[subQ9,subQ433]});var subQ437=makeQuery(id+"F0.imprint","IMPRINT",EDGE,{"disambiguationData":[TD([[subQ436,1.0]])],"derivedFrom":subQ9});var subQ438=makeQuery(id+"F0.imprint","IMPRINT",EDGE,{"disambiguationData":[TD([[subQ431,1.0]])],"derivedFrom":subQ10});var subQ439=sQuery(id+"F0.wireOp",EDGE,"E7.21.4");var subQ440=makeQuery(id+"F0.imprint","INTERSECT",VERTEX,{"derivedFrom":[subQ36,subQ220,subQ439]});var subQ442=sQuery(id+"F0.wireOp",EDGE,"E7.13.5");var subQ446=sQuery(id+"F0.wireOp",EDGE,"E7.37.4");var subQ447=makeQuery(id+"F0.imprint","INTERSECT",VERTEX,{"derivedFrom":[subQ4,subQ172,subQ446]});var subQ449=sQuery(id+"F0.wireOp",EDGE,"E7.29.5");var subQ452=sQuery(id+"F0.wireOp",EDGE,"E7.6.4");var subQ453=sQuery(id+"F0.wireOp",EDGE,"E7.6.3");var subQ454=makeQuery(id+"F0.imprint","INTERSECT",VERTEX,{"derivedFrom":[subQ66,subQ453,subQ452]});var subQ456=sQuery(id+"F0.wireOp",EDGE,"E7.6.5");var subQ458=makeQuery(id+"F0.imprint","IMPRINT",EDGE,{"disambiguationData":[TD([[subQ454,-1.0]])],"derivedFrom":subQ453});var subQ460=makeQuery(id+"F0.imprint","INTERSECT",VERTEX,{"derivedFrom":[subQ74,subQ295]});var subQ461=sQuery(id+"F0.wireOp",EDGE,"E7.2.6");var subQ462=sQuery(id+"F0.wireOp",EDGE,"E7.2.5");var subQ464=makeQuery(id+"F0.imprint","IMPRINT",EDGE,{"disambiguationData":[TD([[subQ296,-1.0]])],"derivedFrom":subQ291});var subQ465=makeQuery(id+"F0.imprint","INTERSECT",VERTEX,{"derivedFrom":[subQ73,subQ462]});var subQ466=makeQuery(id+"F0.imprint","IMPRINT",EDGE,{"disambiguationData":[TD([[subQ465,1.0]])],"derivedFrom":subQ73});var subQ467=makeQuery(id+"F0.imprint","IMPRINT",EDGE,{"disambiguationData":[TD([[subQ460,1.0]])],"derivedFrom":subQ74});var subQ468=makeQuery(id+"F0.imprint","IMPRINT",EDGE,{"disambiguationData":[TD([[subQ371,-1.0]])],"derivedFrom":subQ207});var subQ469=sQuery(id+"F0.wireOp",EDGE,"E7.10.4");var subQ470=makeQuery(id+"F0.imprint","INTERSECT",VERTEX,{"derivedFrom":[subQ58,subQ469]});var subQ471=sQuery(id+"F0.wireOp",EDGE,"E7.10.6");var subQ472=sQuery(id+"F0.wireOp",EDGE,"E7.10.5");var subQ474=makeQuery(id+"F0.imprint","INTERSECT",VERTEX,{"derivedFrom":[subQ58,subQ333,subQ469]});var subQ475=makeQuery(id+"F0.imprint","IMPRINT",EDGE,{"disambiguationData":[TD([[subQ474,-1.0]])],"derivedFrom":subQ333});var subQ476=makeQuery(id+"F0.imprint","INTERSECT",VERTEX,{"derivedFrom":[subQ57,subQ472]});var subQ477=makeQuery(id+"F0.imprint","IMPRINT",EDGE,{"disambiguationData":[TD([[subQ476,1.0]])],"derivedFrom":subQ57});var subQ478=makeQuery(id+"F0.imprint","IMPRINT",EDGE,{"disambiguationData":[TD([[subQ470,1.0]])],"derivedFrom":subQ58});var subQ479=sQuery(id+"F0.wireOp",EDGE,"E7.5.4");var subQ480=makeQuery(id+"F0.imprint","INTERSECT",VERTEX,{"derivedFrom":[subQ68,subQ267,subQ479]});var subQ482=sQuery(id+"F0.wireOp",EDGE,"E7.39.4");var subQ483=makeQuery(id+"F0.imprint","INTERSECT",VERTEX,{"derivedFrom":[subQ0,subQ482]});var subQ484=makeQuery(id+"F0.imprint","INTERSECT",VERTEX,{"derivedFrom":[subQ0,subQ193,subQ482]});var subQ485=makeQuery(id+"F0.imprint","IMPRINT",EDGE,{"disambiguationData":[TD([[subQ483,1.0]])],"derivedFrom":subQ0});var subQ486=makeQuery(id+"F0.imprint","INTERSECT",VERTEX,{"derivedFrom":[subQ7,subQ95]});var subQ487=makeQuery(id+"F0.imprint","IMPRINT",EDGE,{"disambiguationData":[TD([[subQ486,1.0]])],"derivedFrom":subQ7});var subQ491=makeQuery(id+"F0.imprint","INTERSECT",VERTEX,{"derivedFrom":[subQ55,subQ148]});var subQ492=makeQuery(id+"F0.imprint","IMPRINT",EDGE,{"disambiguationData":[TD([[subQ491,1.0]])],"derivedFrom":subQ55});var subQ493=makeQuery(id+"F0.imprint","INTERSECT",VERTEX,{"derivedFrom":[subQ39,subQ166]});var subQ494=makeQuery(id+"F0.imprint","IMPRINT",EDGE,{"disambiguationData":[TD([[subQ493,1.0]])],"derivedFrom":subQ39});var subQ495=makeQuery(id+"F0.imprint","INTERSECT",VERTEX,{"derivedFrom":[subQ23,subQ86]});var subQ496=makeQuery(id+"F0.imprint","IMPRINT",EDGE,{"disambiguationData":[TD([[subQ495,1.0]])],"derivedFrom":subQ23});var subQ499=sQuery(id+"F0.wireOp",EDGE,"E7.37.5");var subQ500=makeQuery(id+"F0.imprint","INTERSECT",VERTEX,{"derivedFrom":[subQ3,subQ499]});var subQ502=makeQuery(id+"F0.imprint","IMPRINT",EDGE,{"disambiguationData":[TD([[subQ500,1.0]])],"derivedFrom":subQ3});var subQ505=makeQuery(id+"F0.imprint","INTERSECT",VERTEX,{"derivedFrom":[subQ51,subQ442]});var subQ506=makeQuery(id+"F0.imprint","IMPRINT",EDGE,{"disambiguationData":[TD([[subQ505,1.0]])],"derivedFrom":subQ51});var subQ507=sQuery(id+"F0.wireOp",EDGE,"E7.21.5");var subQ508=makeQuery(id+"F0.imprint","INTERSECT",VERTEX,{"derivedFrom":[subQ35,subQ507]});var subQ510=makeQuery(id+"F0.imprint","IMPRINT",EDGE,{"disambiguationData":[TD([[subQ508,1.0]])],"derivedFrom":subQ35});var subQ511=makeQuery(id+"F0.imprint","INTERSECT",VERTEX,{"derivedFrom":[subQ19,subQ449]});var subQ512=makeQuery(id+"F0.imprint","IMPRINT",EDGE,{"disambiguationData":[TD([[subQ511,1.0]])],"derivedFrom":subQ19});var subQ513=makeQuery(id+"F0.imprint","INTERSECT",VERTEX,{"derivedFrom":[subQ40,subQ161]});var subQ514=sQuery(id+"F0.wireOp",EDGE,"E7.19.6");var subQ515=makeQuery(id+"F0.imprint","IMPRINT",EDGE,{"disambiguationData":[TD([[subQ513,1.0]])],"derivedFrom":subQ40});var subQ516=makeQuery(id+"F0.imprint","INTERSECT",VERTEX,{"derivedFrom":[subQ24,subQ81]});var subQ517=sQuery(id+"F0.wireOp",EDGE,"E7.27.6");var subQ518=makeQuery(id+"F0.imprint","IMPRINT",EDGE,{"disambiguationData":[TD([[subQ516,1.0]])],"derivedFrom":subQ24});var subQ519=makeQuery(id+"F0.imprint","INTERSECT",VERTEX,{"derivedFrom":[subQ8,subQ90]});var subQ520=sQuery(id+"F0.wireOp",EDGE,"E7.35.6");var subQ521=makeQuery(id+"F0.imprint","IMPRINT",EDGE,{"disambiguationData":[TD([[subQ519,1.0]])],"derivedFrom":subQ8});var subQ524=makeQuery(id+"F0.imprint","INTERSECT",VERTEX,{"derivedFrom":[subQ72,subQ125]});var subQ525=sQuery(id+"F0.wireOp",EDGE,"E7.3.6");var subQ526=makeQuery(id+"F0.imprint","INTERSECT",VERTEX,{"derivedFrom":[subQ71,subQ130]});var subQ527=makeQuery(id+"F0.imprint","IMPRINT",EDGE,{"disambiguationData":[TD([[subQ526,1.0]])],"derivedFrom":subQ71});var subQ528=makeQuery(id+"F0.imprint","IMPRINT",EDGE,{"disambiguationData":[TD([[subQ524,1.0]])],"derivedFrom":subQ72});var subQ529=makeQuery(id+"F0.imprint","INTERSECT",VERTEX,{"derivedFrom":[subQ56,subQ143]});var subQ530=sQuery(id+"F0.wireOp",EDGE,"E7.11.6");var subQ531=makeQuery(id+"F0.imprint","IMPRINT",EDGE,{"disambiguationData":[TD([[subQ529,1.0]])],"derivedFrom":subQ56});var subQ532=makeQuery(id+"F0.imprint","INTERSECT",VERTEX,{"derivedFrom":[subQ66,subQ452]});var subQ533=makeQuery(id+"F0.imprint","IMPRINT",EDGE,{"disambiguationData":[TD([[subQ532,1.0]])],"derivedFrom":subQ66});var subQ534=sQuery(id+"F0.wireOp",EDGE,"E7.5.5");var subQ535=makeQuery(id+"F0.imprint","INTERSECT",VERTEX,{"derivedFrom":[subQ67,subQ534]});var subQ537=makeQuery(id+"F0.imprint","IMPRINT",EDGE,{"disambiguationData":[TD([[subQ535,1.0]])],"derivedFrom":subQ67});var subQ538=makeQuery(id+"F0.imprint","INTERSECT",VERTEX,{"derivedFrom":[subQ68,subQ479]});var subQ539=makeQuery(id+"F0.imprint","IMPRINT",EDGE,{"disambiguationData":[TD([[subQ538,1.0]])],"derivedFrom":subQ68});var subQ542=makeQuery(id+"F0.imprint","INTERSECT",VERTEX,{"derivedFrom":[subQ46,subQ116]});var subQ543=makeQuery(id+"F0.imprint","IMPRINT",EDGE,{"disambiguationData":[TD([[subQ542,1.0]])],"derivedFrom":subQ46});var subQ544=makeQuery(id+"F0.imprint","INTERSECT",VERTEX,{"derivedFrom":[subQ30,subQ134]});var subQ545=makeQuery(id+"F0.imprint","IMPRINT",EDGE,{"disambiguationData":[TD([[subQ544,1.0]])],"derivedFrom":subQ30});var subQ546=makeQuery(id+"F0.imprint","INTERSECT",VERTEX,{"derivedFrom":[subQ14,subQ152]});var subQ547=makeQuery(id+"F0.imprint","IMPRINT",EDGE,{"disambiguationData":[TD([[subQ546,1.0]])],"derivedFrom":subQ14});var subQ548=makeQuery(id+"F0.imprint","IMPRINT",EDGE,{"derivedFrom":subQ79});var subQ549=makeQuery(id+"F0.imprint","INTERSECT",VERTEX,{"derivedFrom":[subQ62,subQ99]});var subQ550=makeQuery(id+"F0.imprint","IMPRINT",EDGE,{"disambiguationData":[TD([[subQ549,1.0]])],"derivedFrom":subQ62});var subQ551=makeQuery(id+"F0.imprint","INTERSECT",VERTEX,{"derivedFrom":[subQ36,subQ439]});var subQ552=sQuery(id+"F0.wireOp",EDGE,"E7.21.6");var subQ553=makeQuery(id+"F0.imprint","IMPRINT",EDGE,{"disambiguationData":[TD([[subQ440,-1.0]])],"derivedFrom":subQ220});var subQ554=makeQuery(id+"F0.imprint","IMPRINT",EDGE,{"disambiguationData":[TD([[subQ551,1.0]])],"derivedFrom":subQ36});var subQ556=sQuery(id+"F0.wireOp",EDGE,"E7.29.4");var subQ557=makeQuery(id+"F0.imprint","INTERSECT",VERTEX,{"derivedFrom":[subQ20,subQ556]});var subQ558=sQuery(id+"F0.wireOp",EDGE,"E7.29.6");var subQ559=makeQuery(id+"F0.imprint","INTERSECT",VERTEX,{"derivedFrom":[subQ20,subQ225,subQ556]});var subQ560=makeQuery(id+"F0.imprint","IMPRINT",EDGE,{"disambiguationData":[TD([[subQ559,-1.0]])],"derivedFrom":subQ225});var subQ561=makeQuery(id+"F0.imprint","IMPRINT",EDGE,{"disambiguationData":[TD([[subQ557,1.0]])],"derivedFrom":subQ20});var subQ563=makeQuery(id+"F0.imprint","INTERSECT",VERTEX,{"derivedFrom":[subQ4,subQ446]});var subQ564=sQuery(id+"F0.wireOp",EDGE,"E7.37.6");var subQ565=makeQuery(id+"F0.imprint","IMPRINT",EDGE,{"disambiguationData":[TD([[subQ447,-1.0]])],"derivedFrom":subQ172});var subQ566=makeQuery(id+"F0.imprint","IMPRINT",EDGE,{"disambiguationData":[TD([[subQ563,1.0]])],"derivedFrom":subQ4});var subQ568=makeQuery(id+"F0.imprint","INTERSECT",VERTEX,{"derivedFrom":[subQ65,subQ456]});var subQ569=makeQuery(id+"F0.imprint","IMPRINT",EDGE,{"disambiguationData":[TD([[subQ568,1.0]])],"derivedFrom":subQ65});var subQ570=sQuery(id+"F0.wireOp",EDGE,"E7.13.4");var subQ571=makeQuery(id+"F0.imprint","INTERSECT",VERTEX,{"derivedFrom":[subQ52,subQ215,subQ570]});var subQ574=sQuery(id+"F0.wireOp",EDGE,"E7.5.6");var subQ575=makeQuery(id+"F0.imprint","IMPRINT",EDGE,{"disambiguationData":[TD([[subQ480,-1.0]])],"derivedFrom":subQ267});var subQ577=makeQuery(id+"F0.imprint","INTERSECT",VERTEX,{"derivedFrom":[subQ52,subQ570]});var subQ578=sQuery(id+"F0.wireOp",EDGE,"E7.13.6");var subQ579=makeQuery(id+"F0.imprint","IMPRINT",EDGE,{"disambiguationData":[TD([[subQ571,-1.0]])],"derivedFrom":subQ215});var subQ580=makeQuery(id+"F0.imprint","IMPRINT",EDGE,{"disambiguationData":[TD([[subQ577,1.0]])],"derivedFrom":subQ52});var subQ582=makeQuery(id+"F0.imprint","INTERSECT",VERTEX,{"derivedFrom":[subQ49,subQ206]});var subQ583=makeQuery(id+"F0.imprint","IMPRINT",EDGE,{"disambiguationData":[TD([[subQ582,1.0]])],"derivedFrom":subQ49});var subQ584=makeQuery(id+"F0.imprint","INTERSECT",VERTEX,{"derivedFrom":[subQ33,subQ402]});var subQ585=makeQuery(id+"F0.imprint","IMPRINT",EDGE,{"disambiguationData":[TD([[subQ584,1.0]])],"derivedFrom":subQ33});var subQ586=makeQuery(id+"F0.imprint","INTERSECT",VERTEX,{"derivedFrom":[subQ17,subQ109]});var subQ587=makeQuery(id+"F0.imprint","IMPRINT",EDGE,{"disambiguationData":[TD([[subQ586,1.0]])],"derivedFrom":subQ17});var subQ588=makeQuery(id+"F0.imprint","INTERSECT",VERTEX,{"derivedFrom":[subQ1,subQ427]});var subQ589=makeQuery(id+"F0.imprint","IMPRINT",EDGE,{"disambiguationData":[TD([[subQ588,1.0]])],"derivedFrom":subQ1});var subQ590=sQuery(id+"F0.wireOp",EDGE,"E7.8.6");var subQ591=sQuery(id+"F0.wireOp",EDGE,"E7.16.6");var subQ592=sQuery(id+"F0.wireOp",EDGE,"E7.24.6");var subQ593=sQuery(id+"F0.wireOp",EDGE,"E7.32.6");var subQ594=sQuery(id+"F0.wireOp",EDGE,"E7.38.6");var subQ595=sQuery(id+"F0.wireOp",EDGE,"E7.6.6");var subQ596=sQuery(id+"F0.wireOp",EDGE,"E7.14.6");var subQ597=sQuery(id+"F0.wireOp",EDGE,"E7.22.6");var subQ598=sQuery(id+"F0.wireOp",EDGE,"E7.30.6");Q0=qUnion([makeQuery(id+"F0.imprint","IMPRINT",FACE,{"disambiguationData":[TD([[subQ338,1.0]])]}),makeQuery(id+"F0.imprint","IMPRINT",FACE,{"disambiguationData":[TD([[makeQuery(id+"F0.imprint","IMPRINT",EDGE,{"disambiguationData":[TD([[subQ127,1.0]])],"derivedFrom":subQ126}),1.0]])]}),makeQuery(id+"F0.imprint","IMPRINT",FACE,{"disambiguationData":[TD([[subQ353,1.0]])]}),makeQuery(id+"F0.imprint","IMPRINT",FACE,{"disambiguationData":[TD([[subQ349,1.0]])]}),makeQuery(id+"F0.imprint","IMPRINT",FACE,{"disambiguationData":[TD([[subQ342,1.0]])]}),makeQuery(id+"F0.imprint","IMPRINT",FACE,{"disambiguationData":[TD([[subQ579,1.0]])]}),makeQuery(id+"F0.imprint","IMPRINT",FACE,{"disambiguationData":[TD([[subQ575,1.0]])]}),makeQuery(id+"F0.imprint","IMPRINT",FACE,{"disambiguationData":[TD([[makeQuery(id+"F0.imprint","IMPRINT",EDGE,{"disambiguationData":[TD([[subQ92,1.0]])],"derivedFrom":subQ91}),1.0]])]}),makeQuery(id+"F0.imprint","IMPRINT",FACE,{"disambiguationData":[TD([[makeQuery(id+"F0.imprint","IMPRINT",EDGE,{"disambiguationData":[TD([[subQ163,1.0]])],"derivedFrom":subQ162}),1.0]])]}),makeQuery(id+"F0.imprint","IMPRINT",FACE,{"disambiguationData":[TD([[subQ565,1.0]])]}),makeQuery(id+"F0.imprint","IMPRINT",FACE,{"disambiguationData":[TD([[subQ560,1.0]])]}),makeQuery(id+"F0.imprint","IMPRINT",FACE,{"disambiguationData":[TD([[subQ553,1.0]])]}),makeQuery(id+"F0.imprint","IMPRINT",FACE,{"disambiguationData":[TD([[makeQuery(id+"F0.imprint","IMPRINT",EDGE,{"disambiguationData":[TD([[subQ357,1.0]])],"derivedFrom":subQ356}),1.0]])]}),makeQuery(id+"F0.imprint","IMPRINT",FACE,{"disambiguationData":[TD([[makeQuery(id+"F0.imprint","IMPRINT",EDGE,{"disambiguationData":[TD([[subQ376,1.0]])],"derivedFrom":subQ375}),1.0]])]}),makeQuery(id+"F0.imprint","IMPRINT",FACE,{"disambiguationData":[TD([[makeQuery(id+"F0.imprint","IMPRINT",EDGE,{"disambiguationData":[TD([[subQ454,1.0]])],"derivedFrom":subQ453}),1.0]])]}),makeQuery(id+"F0.imprint","IMPRINT",FACE,{"disambiguationData":[TD([[subQ521,-1.0]])]}),makeQuery(id+"F0.imprint","IMPRINT",FACE,{"disambiguationData":[TD([[makeQuery(id+"F0.imprint","IMPRINT",EDGE,{"derivedFrom":subQ598}),1.0]])]}),makeQuery(id+"F0.imprint","IMPRINT",FACE,{"disambiguationData":[TD([[makeQuery(id+"F0.imprint","IMPRINT",EDGE,{"derivedFrom":subQ597}),1.0]])]}),makeQuery(id+"F0.imprint","IMPRINT",FACE,{"disambiguationData":[TD([[makeQuery(id+"F0.imprint","IMPRINT",EDGE,{"derivedFrom":subQ596}),1.0]])]}),makeQuery(id+"F0.imprint","IMPRINT",FACE,{"disambiguationData":[TD([[makeQuery(id+"F0.imprint","IMPRINT",EDGE,{"derivedFrom":subQ595}),1.0]])]}),makeQuery(id+"F0.imprint","IMPRINT",FACE,{"disambiguationData":[TD([[makeQuery(id+"F0.imprint","IMPRINT",EDGE,{"derivedFrom":subQ594}),1.0]])]}),makeQuery(id+"F0.imprint","IMPRINT",FACE,{"disambiguationData":[TD([[subQ561,-1.0]])]}),makeQuery(id+"F0.imprint","IMPRINT",FACE,{"disambiguationData":[TD([[subQ554,-1.0]])]}),makeQuery(id+"F0.imprint","IMPRINT",FACE,{"disambiguationData":[TD([[subQ580,-1.0]])]}),makeQuery(id+"F0.imprint","IMPRINT",FACE,{"disambiguationData":[TD([[subQ548,-1.0]])]}),makeQuery(id+"F0.imprint","IMPRINT",FACE,{"disambiguationData":[TD([[makeQuery(id+"F0.imprint","IMPRINT",EDGE,{"disambiguationData":[TD([[subQ421,1.0]])],"derivedFrom":subQ344}),1.0]])]}),makeQuery(id+"F0.imprint","IMPRINT",FACE,{"disambiguationData":[TD([[makeQuery(id+"F0.imprint","IMPRINT",EDGE,{"disambiguationData":[TD([[subQ474,1.0]])],"derivedFrom":subQ333}),1.0]])]}),makeQuery(id+"F0.imprint","IMPRINT",FACE,{"disambiguationData":[TD([[subQ566,-1.0]])]}),makeQuery(id+"F0.imprint","IMPRINT",FACE,{"disambiguationData":[TD([[makeQuery(id+"F0.imprint","IMPRINT",EDGE,{"derivedFrom":subQ593}),1.0]])]}),makeQuery(id+"F0.imprint","IMPRINT",FACE,{"disambiguationData":[TD([[makeQuery(id+"F0.imprint","IMPRINT",EDGE,{"derivedFrom":subQ592}),1.0]])]}),makeQuery(id+"F0.imprint","IMPRINT",FACE,{"disambiguationData":[TD([[makeQuery(id+"F0.imprint","IMPRINT",EDGE,{"derivedFrom":subQ591}),1.0]])]}),makeQuery(id+"F0.imprint","IMPRINT",FACE,{"disambiguationData":[TD([[makeQuery(id+"F0.imprint","IMPRINT",EDGE,{"derivedFrom":subQ590}),1.0]])]}),makeQuery(id+"F0.imprint","IMPRINT",FACE,{"disambiguationData":[TD([[subQ518,-1.0]])]}),makeQuery(id+"F0.imprint","IMPRINT",FACE,{"disambiguationData":[TD([[subQ515,-1.0]])]}),makeQuery(id+"F0.imprint","IMPRINT",FACE,{"disambiguationData":[TD([[subQ531,-1.0]])]}),makeQuery(id+"F0.imprint","IMPRINT",FACE,{"disambiguationData":[TD([[subQ478,-1.0]])]}),makeQuery(id+"F0.imprint","IMPRINT",FACE,{"disambiguationData":[TD([[subQ589,1.0]])]}),makeQuery(id+"F0.imprint","IMPRINT",FACE,{"disambiguationData":[TD([[makeQuery(id+"F0.imprint","IMPRINT",EDGE,{"disambiguationData":[TD([[subQ270,1.0]])],"derivedFrom":subQ129}),1.0]])]}),makeQuery(id+"F0.imprint","IMPRINT",FACE,{"disambiguationData":[TD([[subQ587,1.0]])]}),makeQuery(id+"F0.imprint","IMPRINT",FACE,{"disambiguationData":[TD([[subQ438,-1.0]])]}),makeQuery(id+"F0.imprint","IMPRINT",FACE,{"disambiguationData":[TD([[subQ585,1.0]])]}),makeQuery(id+"F0.imprint","IMPRINT",FACE,{"disambiguationData":[TD([[subQ425,-1.0]])]}),makeQuery(id+"F0.imprint","IMPRINT",FACE,{"disambiguationData":[TD([[subQ309,1.0]])]}),makeQuery(id+"F0.imprint","IMPRINT",FACE,{"disambiguationData":[TD([[subQ583,1.0]])]}),makeQuery(id+"F0.imprint","IMPRINT",FACE,{"disambiguationData":[TD([[subQ413,-1.0]])]}),makeQuery(id+"F0.imprint","IMPRINT",FACE,{"disambiguationData":[TD([[subQ475,1.0]])]}),makeQuery(id+"F0.imprint","IMPRINT",FACE,{"disambiguationData":[TD([[makeQuery(id+"F0.imprint","IMPRINT",EDGE,{"derivedFrom":subQ578}),1.0]])]}),makeQuery(id+"F0.imprint","IMPRINT",FACE,{"disambiguationData":[TD([[subQ464,1.0]])]}),makeQuery(id+"F0.imprint","IMPRINT",FACE,{"disambiguationData":[TD([[makeQuery(id+"F0.imprint","IMPRINT",EDGE,{"derivedFrom":subQ574}),1.0]])]}),makeQuery(id+"F0.imprint","IMPRINT",FACE,{"disambiguationData":[TD([[makeQuery(id+"F0.imprint","IMPRINT",EDGE,{"disambiguationData":[TD([[subQ559,1.0]])],"derivedFrom":subQ225}),1.0]])]}),makeQuery(id+"F0.imprint","IMPRINT",FACE,{"disambiguationData":[TD([[makeQuery(id+"F0.imprint","IMPRINT",EDGE,{"disambiguationData":[TD([[subQ247,1.0]])],"derivedFrom":subQ94}),1.0]])]}),makeQuery(id+"F0.imprint","IMPRINT",FACE,{"disambiguationData":[TD([[makeQuery(id+"F0.imprint","IMPRINT",EDGE,{"disambiguationData":[TD([[subQ571,1.0]])],"derivedFrom":subQ215}),1.0]])]}),makeQuery(id+"F0.imprint","IMPRINT",FACE,{"disambiguationData":[TD([[makeQuery(id+"F0.imprint","IMPRINT",EDGE,{"disambiguationData":[TD([[subQ235,1.0]])],"derivedFrom":subQ165}),1.0]])]}),makeQuery(id+"F0.imprint","IMPRINT",FACE,{"disambiguationData":[TD([[subQ569,1.0]])]}),makeQuery(id+"F0.imprint","IMPRINT",FACE,{"disambiguationData":[TD([[subQ435,1.0]])]}),makeQuery(id+"F0.imprint","IMPRINT",FACE,{"disambiguationData":[TD([[makeQuery(id+"F0.imprint","IMPRINT",EDGE,{"derivedFrom":subQ564}),1.0]])]}),makeQuery(id+"F0.imprint","IMPRINT",FACE,{"disambiguationData":[TD([[subQ422,1.0]])]}),makeQuery(id+"F0.imprint","IMPRINT",FACE,{"disambiguationData":[TD([[makeQuery(id+"F0.imprint","IMPRINT",EDGE,{"derivedFrom":subQ558}),1.0]])]}),makeQuery(id+"F0.imprint","IMPRINT",FACE,{"disambiguationData":[TD([[subQ410,1.0]])]}),makeQuery(id+"F0.imprint","IMPRINT",FACE,{"disambiguationData":[TD([[makeQuery(id+"F0.imprint","IMPRINT",EDGE,{"derivedFrom":subQ552}),1.0]])]}),makeQuery(id+"F0.imprint","IMPRINT",FACE,{"disambiguationData":[TD([[subQ310,-1.0]])]}),makeQuery(id+"F0.imprint","IMPRINT",FACE,{"disambiguationData":[TD([[subQ550,-1.0]])]}),makeQuery(id+"F0.imprint","IMPRINT",FACE,{"disambiguationData":[TD([[subQ548,1.0]])]}),makeQuery(id+"F0.imprint","IMPRINT",FACE,{"disambiguationData":[TD([[subQ547,-1.0]])]}),makeQuery(id+"F0.imprint","IMPRINT",FACE,{"disambiguationData":[TD([[subQ545,-1.0]])]}),makeQuery(id+"F0.imprint","IMPRINT",FACE,{"disambiguationData":[TD([[subQ543,-1.0]])]}),makeQuery(id+"F0.imprint","IMPRINT",FACE,{"disambiguationData":[TD([[subQ330,1.0]])]}),makeQuery(id+"F0.imprint","IMPRINT",FACE,{"disambiguationData":[TD([[subQ328,-1.0]])]}),makeQuery(id+"F0.imprint","IMPRINT",FACE,{"disambiguationData":[TD([[subQ368,-1.0]])]}),makeQuery(id+"F0.imprint","IMPRINT",FACE,{"disambiguationData":[TD([[subQ367,1.0]])]}),makeQuery(id+"F0.imprint","IMPRINT",FACE,{"disambiguationData":[TD([[subQ467,-1.0]])]}),makeQuery(id+"F0.imprint","IMPRINT",FACE,{"disambiguationData":[TD([[subQ466,1.0]])]}),makeQuery(id+"F0.imprint","IMPRINT",FACE,{"disambiguationData":[TD([[subQ323,1.0]])]}),makeQuery(id+"F0.imprint","IMPRINT",FACE,{"disambiguationData":[TD([[subQ319,1.0]])]}),makeQuery(id+"F0.imprint","IMPRINT",FACE,{"disambiguationData":[TD([[subQ313,1.0]])]}),makeQuery(id+"F0.imprint","IMPRINT",FACE,{"disambiguationData":[TD([[subQ307,1.0]])]}),makeQuery(id+"F0.imprint","IMPRINT",FACE,{"disambiguationData":[TD([[subQ528,-1.0]])]}),makeQuery(id+"F0.imprint","IMPRINT",FACE,{"disambiguationData":[TD([[subQ191,-1.0]])]}),makeQuery(id+"F0.imprint","IMPRINT",FACE,{"disambiguationData":[TD([[subQ527,1.0]])]}),makeQuery(id+"F0.imprint","IMPRINT",FACE,{"disambiguationData":[TD([[subQ274,-1.0]])]}),makeQuery(id+"F0.imprint","IMPRINT",FACE,{"disambiguationData":[TD([[subQ273,1.0]])]}),makeQuery(id+"F0.imprint","IMPRINT",FACE,{"disambiguationData":[TD([[subQ539,-1.0]])]}),makeQuery(id+"F0.imprint","IMPRINT",FACE,{"disambiguationData":[TD([[subQ537,1.0]])]}),makeQuery(id+"F0.imprint","IMPRINT",FACE,{"disambiguationData":[TD([[subQ533,-1.0]])]}),makeQuery(id+"F0.imprint","IMPRINT",FACE,{"disambiguationData":[TD([[makeQuery(id+"F0.imprint","IMPRINT",EDGE,{"derivedFrom":subQ530}),1.0]])]}),makeQuery(id+"F0.imprint","IMPRINT",FACE,{"disambiguationData":[TD([[makeQuery(id+"F0.imprint","IMPRINT",EDGE,{"derivedFrom":subQ525}),1.0]])]}),makeQuery(id+"F0.imprint","IMPRINT",FACE,{"disambiguationData":[TD([[makeQuery(id+"F0.imprint","IMPRINT",EDGE,{"disambiguationData":[TD([[subQ154,1.0]])],"derivedFrom":subQ153}),1.0]])]}),makeQuery(id+"F0.imprint","IMPRINT",FACE,{"disambiguationData":[TD([[makeQuery(id+"F0.imprint","IMPRINT",EDGE,{"disambiguationData":[TD([[subQ118,1.0]])],"derivedFrom":subQ117}),1.0]])]}),makeQuery(id+"F0.imprint","IMPRINT",FACE,{"disambiguationData":[TD([[makeQuery(id+"F0.imprint","IMPRINT",EDGE,{"derivedFrom":subQ520}),1.0]])]}),makeQuery(id+"F0.imprint","IMPRINT",FACE,{"disambiguationData":[TD([[makeQuery(id+"F0.imprint","IMPRINT",EDGE,{"derivedFrom":subQ517}),1.0]])]}),makeQuery(id+"F0.imprint","IMPRINT",FACE,{"disambiguationData":[TD([[makeQuery(id+"F0.imprint","IMPRINT",EDGE,{"derivedFrom":subQ514}),1.0]])]}),makeQuery(id+"F0.imprint","IMPRINT",FACE,{"disambiguationData":[TD([[subQ512,1.0]])]}),makeQuery(id+"F0.imprint","IMPRINT",FACE,{"disambiguationData":[TD([[subQ510,1.0]])]}),makeQuery(id+"F0.imprint","IMPRINT",FACE,{"disambiguationData":[TD([[subQ506,1.0]])]}),makeQuery(id+"F0.imprint","IMPRINT",FACE,{"disambiguationData":[TD([[subQ365,1.0]])]}),makeQuery(id+"F0.imprint","IMPRINT",FACE,{"disambiguationData":[TD([[makeQuery(id+"F0.imprint","IMPRINT",EDGE,{"disambiguationData":[TD([[subQ83,1.0]])],"derivedFrom":subQ82}),1.0]])]}),makeQuery(id+"F0.imprint","IMPRINT",FACE,{"disambiguationData":[TD([[makeQuery(id+"F0.imprint","IMPRINT",EDGE,{"disambiguationData":[TD([[subQ145,1.0]])],"derivedFrom":subQ144}),1.0]])]}),makeQuery(id+"F0.imprint","IMPRINT",FACE,{"disambiguationData":[TD([[subQ502,1.0]])]}),makeQuery(id+"F0.imprint","IMPRINT",FACE,{"disambiguationData":[TD([[subQ351,1.0]])]}),makeQuery(id+"F0.imprint","IMPRINT",FACE,{"disambiguationData":[TD([[subQ347,1.0]])]}),makeQuery(id+"F0.imprint","IMPRINT",FACE,{"disambiguationData":[TD([[subQ340,1.0]])]}),makeQuery(id+"F0.imprint","IMPRINT",FACE,{"disambiguationData":[TD([[subQ336,1.0]])]}),makeQuery(id+"F0.imprint","IMPRINT",FACE,{"disambiguationData":[TD([[subQ496,1.0]])]}),makeQuery(id+"F0.imprint","IMPRINT",FACE,{"disambiguationData":[TD([[subQ494,1.0]])]}),makeQuery(id+"F0.imprint","IMPRINT",FACE,{"disambiguationData":[TD([[subQ492,1.0]])]}),makeQuery(id+"F0.imprint","IMPRINT",FACE,{"disambiguationData":[TD([[makeQuery(id+"F0.imprint","IMPRINT",EDGE,{"disambiguationData":[TD([[subQ484,1.0]])],"derivedFrom":subQ193}),1.0]])]}),makeQuery(id+"F0.imprint","IMPRINT",FACE,{"disambiguationData":[TD([[makeQuery(id+"F0.imprint","IMPRINT",EDGE,{"disambiguationData":[TD([[subQ318,1.0]])],"derivedFrom":subQ177}),1.0]])]}),makeQuery(id+"F0.imprint","IMPRINT",FACE,{"disambiguationData":[TD([[makeQuery(id+"F0.imprint","IMPRINT",EDGE,{"disambiguationData":[TD([[subQ306,1.0]])],"derivedFrom":subQ304}),1.0]])]}),makeQuery(id+"F0.imprint","IMPRINT",FACE,{"disambiguationData":[TD([[subQ487,1.0]])]}),makeQuery(id+"F0.imprint","IMPRINT",FACE,{"disambiguationData":[TD([[subQ477,1.0]])]}),makeQuery(id+"F0.imprint","IMPRINT",FACE,{"disambiguationData":[TD([[subQ485,-1.0]])]}),makeQuery(id+"F0.imprint","IMPRINT",FACE,{"disambiguationData":[TD([[makeQuery(id+"F0.imprint","IMPRINT",EDGE,{"disambiguationData":[TD([[subQ480,1.0]])],"derivedFrom":subQ267}),1.0]])]}),makeQuery(id+"F0.imprint","IMPRINT",FACE,{"disambiguationData":[TD([[subQ324,-1.0]])]}),makeQuery(id+"F0.imprint","IMPRINT",FACE,{"disambiguationData":[TD([[subQ437,1.0]])]}),makeQuery(id+"F0.imprint","IMPRINT",FACE,{"disambiguationData":[TD([[subQ320,-1.0]])]}),makeQuery(id+"F0.imprint","IMPRINT",FACE,{"disambiguationData":[TD([[subQ424,1.0]])]}),makeQuery(id+"F0.imprint","IMPRINT",FACE,{"disambiguationData":[TD([[subQ314,-1.0]])]}),makeQuery(id+"F0.imprint","IMPRINT",FACE,{"disambiguationData":[TD([[subQ412,1.0]])]}),makeQuery(id+"F0.imprint","IMPRINT",FACE,{"disambiguationData":[TD([[makeQuery(id+"F0.imprint","IMPRINT",EDGE,{"derivedFrom":subQ471}),1.0]])]}),makeQuery(id+"F0.imprint","IMPRINT",FACE,{"disambiguationData":[TD([[subQ468,1.0]])]}),makeQuery(id+"F0.imprint","IMPRINT",FACE,{"disambiguationData":[TD([[makeQuery(id+"F0.imprint","IMPRINT",EDGE,{"derivedFrom":subQ461}),1.0]])]}),makeQuery(id+"F0.imprint","IMPRINT",FACE,{"disambiguationData":[TD([[subQ458,1.0]])]}),makeQuery(id+"F0.imprint","IMPRINT",FACE,{"disambiguationData":[TD([[makeQuery(id+"F0.imprint","IMPRINT",EDGE,{"disambiguationData":[TD([[subQ380,1.0]])],"derivedFrom":subQ110}),1.0]])]}),makeQuery(id+"F0.imprint","IMPRINT",FACE,{"disambiguationData":[TD([[makeQuery(id+"F0.imprint","IMPRINT",EDGE,{"disambiguationData":[TD([[subQ447,1.0]])],"derivedFrom":subQ172}),1.0]])]}),makeQuery(id+"F0.imprint","IMPRINT",FACE,{"disambiguationData":[TD([[makeQuery(id+"F0.imprint","IMPRINT",EDGE,{"disambiguationData":[TD([[subQ371,1.0]])],"derivedFrom":subQ207}),1.0]])]}),makeQuery(id+"F0.imprint","IMPRINT",FACE,{"disambiguationData":[TD([[makeQuery(id+"F0.imprint","IMPRINT",EDGE,{"disambiguationData":[TD([[subQ440,1.0]])],"derivedFrom":subQ220}),1.0]])]}),makeQuery(id+"F0.imprint","IMPRINT",FACE,{"disambiguationData":[TD([[makeQuery(id+"F0.imprint","IMPRINT",EDGE,{"derivedFrom":subQ432}),1.0]])]}),makeQuery(id+"F0.imprint","IMPRINT",FACE,{"disambiguationData":[TD([[subQ429,1.0]])]}),makeQuery(id+"F0.imprint","IMPRINT",FACE,{"disambiguationData":[TD([[makeQuery(id+"F0.imprint","IMPRINT",EDGE,{"derivedFrom":subQ418}),1.0]])]}),makeQuery(id+"F0.imprint","IMPRINT",FACE,{"disambiguationData":[TD([[subQ415,1.0]])]}),makeQuery(id+"F0.imprint","IMPRINT",FACE,{"disambiguationData":[TD([[makeQuery(id+"F0.imprint","IMPRINT",EDGE,{"derivedFrom":subQ407}),1.0]])]}),makeQuery(id+"F0.imprint","IMPRINT",FACE,{"disambiguationData":[TD([[subQ404,1.0]])]}),makeQuery(id+"F0.imprint","IMPRINT",FACE,{"disambiguationData":[TD([[subQ400,1.0]])]}),makeQuery(id+"F0.imprint","IMPRINT",FACE,{"disambiguationData":[TD([[makeQuery(id+"F0.imprint","IMPRINT",EDGE,{"disambiguationData":[TD([[subQ364,1.0]])],"derivedFrom":subQ197}),1.0]])]}),makeQuery(id+"F0.imprint","IMPRINT",FACE,{"disambiguationData":[TD([[subQ397,1.0]])]}),makeQuery(id+"F0.imprint","IMPRINT",FACE,{"disambiguationData":[TD([[subQ395,1.0]])]}),makeQuery(id+"F0.imprint","IMPRINT",FACE,{"disambiguationData":[TD([[subQ393,1.0]])]}),makeQuery(id+"F0.imprint","IMPRINT",FACE,{"disambiguationData":[TD([[subQ279,1.0]])]}),makeQuery(id+"F0.imprint","IMPRINT",FACE,{"disambiguationData":[TD([[subQ271,1.0]])]}),makeQuery(id+"F0.imprint","IMPRINT",FACE,{"disambiguationData":[TD([[makeQuery(id+"F0.imprint","IMPRINT",EDGE,{"disambiguationData":[TD([[subQ289,1.0]])],"derivedFrom":subQ156}),1.0]])]}),makeQuery(id+"F0.imprint","IMPRINT",FACE,{"disambiguationData":[TD([[makeQuery(id+"F0.imprint","IMPRINT",EDGE,{"disambiguationData":[TD([[subQ283,1.0]])],"derivedFrom":subQ120}),1.0]])]}),makeQuery(id+"F0.imprint","IMPRINT",FACE,{"disambiguationData":[TD([[subQ248,1.0]])]}),makeQuery(id+"F0.imprint","IMPRINT",FACE,{"disambiguationData":[TD([[subQ242,1.0]])]}),makeQuery(id+"F0.imprint","IMPRINT",FACE,{"disambiguationData":[TD([[subQ236,1.0]])]}),makeQuery(id+"F0.imprint","IMPRINT",FACE,{"disambiguationData":[TD([[subQ381,-1.0]])]}),makeQuery(id+"F0.imprint","IMPRINT",FACE,{"disambiguationData":[TD([[subQ377,-1.0]])]}),makeQuery(id+"F0.imprint","IMPRINT",FACE,{"disambiguationData":[TD([[subQ372,-1.0]])]}),makeQuery(id+"F0.imprint","IMPRINT",FACE,{"disambiguationData":[TD([[makeQuery(id+"F0.imprint","IMPRINT",EDGE,{"derivedFrom":subQ363}),1.0]])]}),makeQuery(id+"F0.imprint","IMPRINT",FACE,{"disambiguationData":[TD([[makeQuery(id+"F0.imprint","IMPRINT",EDGE,{"disambiguationData":[TD([[subQ241,1.0]])],"derivedFrom":subQ85}),1.0]])]}),makeQuery(id+"F0.imprint","IMPRINT",FACE,{"disambiguationData":[TD([[makeQuery(id+"F0.imprint","IMPRINT",EDGE,{"disambiguationData":[TD([[subQ278,1.0]])],"derivedFrom":subQ147}),1.0]])]}),makeQuery(id+"F0.imprint","IMPRINT",FACE,{"disambiguationData":[TD([[subQ358,-1.0]])]}),makeQuery(id+"F0.imprint","IMPRINT",FACE,{"disambiguationData":[TD([[makeQuery(id+"F0.imprint","IMPRINT",EDGE,{"derivedFrom":subQ350}),1.0]])]}),makeQuery(id+"F0.imprint","IMPRINT",FACE,{"disambiguationData":[TD([[makeQuery(id+"F0.imprint","IMPRINT",EDGE,{"derivedFrom":subQ343}),1.0]])]}),makeQuery(id+"F0.imprint","IMPRINT",FACE,{"disambiguationData":[TD([[makeQuery(id+"F0.imprint","IMPRINT",EDGE,{"derivedFrom":subQ339}),1.0]])]}),makeQuery(id+"F0.imprint","IMPRINT",FACE,{"disambiguationData":[TD([[makeQuery(id+"F0.imprint","IMPRINT",EDGE,{"derivedFrom":subQ332}),1.0]])]}),makeQuery(id+"F0.imprint","IMPRINT",FACE,{"disambiguationData":[TD([[subQ243,-1.0]])]}),makeQuery(id+"F0.imprint","IMPRINT",FACE,{"disambiguationData":[TD([[subQ237,-1.0]])]}),makeQuery(id+"F0.imprint","IMPRINT",FACE,{"disambiguationData":[TD([[subQ280,-1.0]])]}),makeQuery(id+"F0.imprint","IMPRINT",FACE,{"disambiguationData":[TD([[makeQuery(id+"F0.imprint","IMPRINT",EDGE,{"derivedFrom":subQ331}),1.0]])]}),makeQuery(id+"F0.imprint","IMPRINT",FACE,{"disambiguationData":[TD([[makeQuery(id+"F0.imprint","IMPRINT",EDGE,{"disambiguationData":[TD([[subQ136,1.0]])],"derivedFrom":subQ135}),1.0]])]}),makeQuery(id+"F0.imprint","IMPRINT",FACE,{"disambiguationData":[TD([[makeQuery(id+"F0.imprint","IMPRINT",EDGE,{"disambiguationData":[TD([[subQ101,1.0]])],"derivedFrom":subQ100}),1.0]])]}),makeQuery(id+"F0.imprint","IMPRINT",FACE,{"disambiguationData":[TD([[subQ249,-1.0]])]}),makeQuery(id+"F0.imprint","IMPRINT",FACE,{"disambiguationData":[TD([[makeQuery(id+"F0.imprint","IMPRINT",EDGE,{"derivedFrom":subQ322}),1.0]])]}),makeQuery(id+"F0.imprint","IMPRINT",FACE,{"disambiguationData":[TD([[makeQuery(id+"F0.imprint","IMPRINT",EDGE,{"derivedFrom":subQ317}),1.0]])]}),makeQuery(id+"F0.imprint","IMPRINT",FACE,{"disambiguationData":[TD([[makeQuery(id+"F0.imprint","IMPRINT",EDGE,{"derivedFrom":subQ312}),1.0]])]}),makeQuery(id+"F0.imprint","IMPRINT",FACE,{"disambiguationData":[TD([[makeQuery(id+"F0.imprint","IMPRINT",EDGE,{"derivedFrom":subQ302}),1.0]])]}),makeQuery(id+"F0.imprint","IMPRINT",FACE,{"disambiguationData":[TD([[subQ299,-1.0]])]}),makeQuery(id+"F0.imprint","IMPRINT",FACE,{"disambiguationData":[TD([[makeQuery(id+"F0.imprint","IMPRINT",EDGE,{"disambiguationData":[TD([[subQ296,1.0]])],"derivedFrom":subQ291}),1.0]])]}),makeQuery(id+"F0.imprint","IMPRINT",FACE,{"disambiguationData":[TD([[subQ290,-1.0]])]}),makeQuery(id+"F0.imprint","IMPRINT",FACE,{"disambiguationData":[TD([[subQ286,-1.0]])]}),makeQuery(id+"F0.imprint","IMPRINT",FACE,{"disambiguationData":[TD([[subQ284,-1.0]])]}),makeQuery(id+"F0.imprint","IMPRINT",FACE,{"disambiguationData":[TD([[makeQuery(id+"F0.imprint","IMPRINT",EDGE,{"derivedFrom":subQ277}),1.0]])]}),makeQuery(id+"F0.imprint","IMPRINT",FACE,{"disambiguationData":[TD([[makeQuery(id+"F0.imprint","IMPRINT",EDGE,{"derivedFrom":subQ266}),1.0]])]}),makeQuery(id+"F0.imprint","IMPRINT",FACE,{"disambiguationData":[TD([[makeQuery(id+"F0.imprint","IMPRINT",EDGE,{"disambiguationData":[TD([[subQ262,1.0]])],"derivedFrom":subQ257}),1.0]])]}),makeQuery(id+"F0.imprint","IMPRINT",FACE,{"disambiguationData":[TD([[makeQuery(id+"F0.imprint","IMPRINT",EDGE,{"disambiguationData":[TD([[subQ255,1.0]])],"derivedFrom":subQ250}),1.0]])]}),makeQuery(id+"F0.imprint","IMPRINT",FACE,{"disambiguationData":[TD([[makeQuery(id+"F0.imprint","IMPRINT",EDGE,{"derivedFrom":subQ246}),1.0]])]}),makeQuery(id+"F0.imprint","IMPRINT",FACE,{"disambiguationData":[TD([[makeQuery(id+"F0.imprint","IMPRINT",EDGE,{"derivedFrom":subQ240}),1.0]])]}),makeQuery(id+"F0.imprint","IMPRINT",FACE,{"disambiguationData":[TD([[makeQuery(id+"F0.imprint","IMPRINT",EDGE,{"derivedFrom":subQ234}),1.0]])]}),makeQuery(id+"F0.imprint","IMPRINT",FACE,{"disambiguationData":[TD([[subQ231,1.0]])]}),makeQuery(id+"F0.imprint","IMPRINT",FACE,{"disambiguationData":[TD([[subQ227,1.0]])]}),makeQuery(id+"F0.imprint","IMPRINT",FACE,{"disambiguationData":[TD([[subQ222,1.0]])]}),makeQuery(id+"F0.imprint","IMPRINT",FACE,{"disambiguationData":[TD([[subQ217,1.0]])]}),makeQuery(id+"F0.imprint","IMPRINT",FACE,{"disambiguationData":[TD([[makeQuery(id+"F0.imprint","IMPRINT",EDGE,{"disambiguationData":[TD([[subQ211,1.0]])],"derivedFrom":subQ205}),1.0]])]}),makeQuery(id+"F0.imprint","IMPRINT",FACE,{"disambiguationData":[TD([[subQ202,1.0]])]}),makeQuery(id+"F0.imprint","IMPRINT",FACE,{"disambiguationData":[TD([[subQ191,1.0]])]}),makeQuery(id+"F0.imprint","IMPRINT",FACE,{"disambiguationData":[TD([[makeQuery(id+"F0.imprint","IMPRINT",EDGE,{"disambiguationData":[TD([[subQ188,1.0]])],"derivedFrom":subQ138}),1.0]])]}),makeQuery(id+"F0.imprint","IMPRINT",FACE,{"disambiguationData":[TD([[subQ186,1.0]])]}),makeQuery(id+"F0.imprint","IMPRINT",FACE,{"disambiguationData":[TD([[makeQuery(id+"F0.imprint","IMPRINT",EDGE,{"disambiguationData":[TD([[subQ181,1.0]])],"derivedFrom":subQ103}),1.0]])]}),makeQuery(id+"F0.imprint","IMPRINT",FACE,{"disambiguationData":[TD([[subQ179,1.0]])]}),makeQuery(id+"F0.imprint","IMPRINT",FACE,{"disambiguationData":[TD([[subQ174,1.0]])]}),makeQuery(id+"F0.imprint","IMPRINT",FACE,{"disambiguationData":[TD([[subQ168,1.0]])]}),makeQuery(id+"F0.imprint","IMPRINT",FACE,{"disambiguationData":[TD([[subQ159,1.0]])]}),makeQuery(id+"F0.imprint","IMPRINT",FACE,{"disambiguationData":[TD([[subQ150,1.0]])]}),makeQuery(id+"F0.imprint","IMPRINT",FACE,{"disambiguationData":[TD([[subQ141,1.0]])]}),makeQuery(id+"F0.imprint","IMPRINT",FACE,{"disambiguationData":[TD([[subQ132,1.0]])]}),makeQuery(id+"F0.imprint","IMPRINT",FACE,{"disambiguationData":[TD([[subQ123,1.0]])]}),makeQuery(id+"F0.imprint","IMPRINT",FACE,{"disambiguationData":[TD([[makeQuery(id+"F0.imprint","IMPRINT",EDGE,{"disambiguationData":[TD([[subQ114,1.0]])],"derivedFrom":subQ108}),1.0]])]}),makeQuery(id+"F0.imprint","IMPRINT",FACE,{"disambiguationData":[TD([[subQ106,1.0]])]}),makeQuery(id+"F0.imprint","IMPRINT",FACE,{"disambiguationData":[TD([[subQ97,1.0]])]}),makeQuery(id+"F0.imprint","IMPRINT",FACE,{"disambiguationData":[TD([[subQ88,1.0]])]})]);}
            extrude(context, id + "F1", {"entities" : qUnion([Q0]), "depth" : 7.62 * mm, "offsetDistance" : 25.4 * mm});
        }
        {
            var Q0;
            Q0=makeQuery(id+"F1.opExtrude","CAP_FACE",FACE,{"disambiguationData":[OSD([sQuery(id+"F0.wireOp",EDGE,"E0"),sQuery(id+"F0.wireOp",EDGE,"E1"),sQuery(id+"F0.wireOp",EDGE,"E5"),sQuery(id+"F0.wireOp",EDGE,"E6"),sQuery(id+"F0.wireOp",EDGE,"E7.1.3"),sQuery(id+"F0.wireOp",EDGE,"E7.1.4"),sQuery(id+"F0.wireOp",EDGE,"E7.1.5"),sQuery(id+"F0.wireOp",EDGE,"E7.1.6"),sQuery(id+"F0.wireOp",EDGE,"E7.2.3"),sQuery(id+"F0.wireOp",EDGE,"E7.2.4"),sQuery(id+"F0.wireOp",EDGE,"E7.2.5"),sQuery(id+"F0.wireOp",EDGE,"E7.2.6"),sQuery(id+"F0.wireOp",EDGE,"E7.3.3"),sQuery(id+"F0.wireOp",EDGE,"E7.3.4"),sQuery(id+"F0.wireOp",EDGE,"E7.3.5"),sQuery(id+"F0.wireOp",EDGE,"E7.3.6"),sQuery(id+"F0.wireOp",EDGE,"E7.4.3"),sQuery(id+"F0.wireOp",EDGE,"E7.4.4"),sQuery(id+"F0.wireOp",EDGE,"E7.4.5"),sQuery(id+"F0.wireOp",EDGE,"E7.4.6"),sQuery(id+"F0.wireOp",EDGE,"E7.5.3"),sQuery(id+"F0.wireOp",EDGE,"E7.5.4"),sQuery(id+"F0.wireOp",EDGE,"E7.5.5"),sQuery(id+"F0.wireOp",EDGE,"E7.5.6"),sQuery(id+"F0.wireOp",EDGE,"E7.6.3"),sQuery(id+"F0.wireOp",EDGE,"E7.6.4"),sQuery(id+"F0.wireOp",EDGE,"E7.6.5"),sQuery(id+"F0.wireOp",EDGE,"E7.6.6"),sQuery(id+"F0.wireOp",EDGE,"E7.7.3"),sQuery(id+"F0.wireOp",EDGE,"E7.7.4"),sQuery(id+"F0.wireOp",EDGE,"E7.7.5"),sQuery(id+"F0.wireOp",EDGE,"E7.7.6"),sQuery(id+"F0.wireOp",EDGE,"E7.8.3"),sQuery(id+"F0.wireOp",EDGE,"E7.8.4"),sQuery(id+"F0.wireOp",EDGE,"E7.8.5"),sQuery(id+"F0.wireOp",EDGE,"E7.8.6"),sQuery(id+"F0.wireOp",EDGE,"E7.9.3"),sQuery(id+"F0.wireOp",EDGE,"E7.9.4"),sQuery(id+"F0.wireOp",EDGE,"E7.9.5"),sQuery(id+"F0.wireOp",EDGE,"E7.9.6"),sQuery(id+"F0.wireOp",EDGE,"E7.10.3"),sQuery(id+"F0.wireOp",EDGE,"E7.10.4"),sQuery(id+"F0.wireOp",EDGE,"E7.10.5"),sQuery(id+"F0.wireOp",EDGE,"E7.10.6"),sQuery(id+"F0.wireOp",EDGE,"E7.11.3"),sQuery(id+"F0.wireOp",EDGE,"E7.11.4"),sQuery(id+"F0.wireOp",EDGE,"E7.11.5"),sQuery(id+"F0.wireOp",EDGE,"E7.11.6"),sQuery(id+"F0.wireOp",EDGE,"E7.12.3"),sQuery(id+"F0.wireOp",EDGE,"E7.12.4"),sQuery(id+"F0.wireOp",EDGE,"E7.12.5"),sQuery(id+"F0.wireOp",EDGE,"E7.12.6"),sQuery(id+"F0.wireOp",EDGE,"E7.13.3"),sQuery(id+"F0.wireOp",EDGE,"E7.13.4"),sQuery(id+"F0.wireOp",EDGE,"E7.13.5"),sQuery(id+"F0.wireOp",EDGE,"E7.13.6"),sQuery(id+"F0.wireOp",EDGE,"E7.14.3"),sQuery(id+"F0.wireOp",EDGE,"E7.14.4"),sQuery(id+"F0.wireOp",EDGE,"E7.14.5"),sQuery(id+"F0.wireOp",EDGE,"E7.14.6"),sQuery(id+"F0.wireOp",EDGE,"E7.15.3"),sQuery(id+"F0.wireOp",EDGE,"E7.15.4"),sQuery(id+"F0.wireOp",EDGE,"E7.15.5"),sQuery(id+"F0.wireOp",EDGE,"E7.15.6"),sQuery(id+"F0.wireOp",EDGE,"E7.16.3"),sQuery(id+"F0.wireOp",EDGE,"E7.16.4"),sQuery(id+"F0.wireOp",EDGE,"E7.16.5"),sQuery(id+"F0.wireOp",EDGE,"E7.16.6"),sQuery(id+"F0.wireOp",EDGE,"E7.17.3"),sQuery(id+"F0.wireOp",EDGE,"E7.17.4"),sQuery(id+"F0.wireOp",EDGE,"E7.17.5"),sQuery(id+"F0.wireOp",EDGE,"E7.17.6"),sQuery(id+"F0.wireOp",EDGE,"E7.18.3"),sQuery(id+"F0.wireOp",EDGE,"E7.18.4"),sQuery(id+"F0.wireOp",EDGE,"E7.18.5"),sQuery(id+"F0.wireOp",EDGE,"E7.18.6"),sQuery(id+"F0.wireOp",EDGE,"E7.19.3"),sQuery(id+"F0.wireOp",EDGE,"E7.19.4"),sQuery(id+"F0.wireOp",EDGE,"E7.19.5"),sQuery(id+"F0.wireOp",EDGE,"E7.19.6"),sQuery(id+"F0.wireOp",EDGE,"E7.20.3"),sQuery(id+"F0.wireOp",EDGE,"E7.20.4"),sQuery(id+"F0.wireOp",EDGE,"E7.20.5"),sQuery(id+"F0.wireOp",EDGE,"E7.20.6"),sQuery(id+"F0.wireOp",EDGE,"E7.21.3"),sQuery(id+"F0.wireOp",EDGE,"E7.21.4"),sQuery(id+"F0.wireOp",EDGE,"E7.21.5"),sQuery(id+"F0.wireOp",EDGE,"E7.21.6"),sQuery(id+"F0.wireOp",EDGE,"E7.22.3"),sQuery(id+"F0.wireOp",EDGE,"E7.22.4"),sQuery(id+"F0.wireOp",EDGE,"E7.22.5"),sQuery(id+"F0.wireOp",EDGE,"E7.22.6"),sQuery(id+"F0.wireOp",EDGE,"E7.23.3"),sQuery(id+"F0.wireOp",EDGE,"E7.23.4"),sQuery(id+"F0.wireOp",EDGE,"E7.23.5"),sQuery(id+"F0.wireOp",EDGE,"E7.23.6"),sQuery(id+"F0.wireOp",EDGE,"E7.24.3"),sQuery(id+"F0.wireOp",EDGE,"E7.24.4"),sQuery(id+"F0.wireOp",EDGE,"E7.24.5"),sQuery(id+"F0.wireOp",EDGE,"E7.24.6"),sQuery(id+"F0.wireOp",EDGE,"E7.25.3"),sQuery(id+"F0.wireOp",EDGE,"E7.25.4"),sQuery(id+"F0.wireOp",EDGE,"E7.25.5"),sQuery(id+"F0.wireOp",EDGE,"E7.25.6"),sQuery(id+"F0.wireOp",EDGE,"E7.26.3"),sQuery(id+"F0.wireOp",EDGE,"E7.26.4"),sQuery(id+"F0.wireOp",EDGE,"E7.26.5"),sQuery(id+"F0.wireOp",EDGE,"E7.26.6"),sQuery(id+"F0.wireOp",EDGE,"E7.27.3"),sQuery(id+"F0.wireOp",EDGE,"E7.27.4"),sQuery(id+"F0.wireOp",EDGE,"E7.27.5"),sQuery(id+"F0.wireOp",EDGE,"E7.27.6"),sQuery(id+"F0.wireOp",EDGE,"E7.28.3"),sQuery(id+"F0.wireOp",EDGE,"E7.28.4"),sQuery(id+"F0.wireOp",EDGE,"E7.28.5"),sQuery(id+"F0.wireOp",EDGE,"E7.28.6"),sQuery(id+"F0.wireOp",EDGE,"E7.29.3"),sQuery(id+"F0.wireOp",EDGE,"E7.29.4"),sQuery(id+"F0.wireOp",EDGE,"E7.29.5"),sQuery(id+"F0.wireOp",EDGE,"E7.29.6"),sQuery(id+"F0.wireOp",EDGE,"E7.30.3"),sQuery(id+"F0.wireOp",EDGE,"E7.30.4"),sQuery(id+"F0.wireOp",EDGE,"E7.30.5"),sQuery(id+"F0.wireOp",EDGE,"E7.30.6"),sQuery(id+"F0.wireOp",EDGE,"E7.31.3"),sQuery(id+"F0.wireOp",EDGE,"E7.31.4"),sQuery(id+"F0.wireOp",EDGE,"E7.31.5"),sQuery(id+"F0.wireOp",EDGE,"E7.31.6"),sQuery(id+"F0.wireOp",EDGE,"E7.32.3"),sQuery(id+"F0.wireOp",EDGE,"E7.32.4"),sQuery(id+"F0.wireOp",EDGE,"E7.32.5"),sQuery(id+"F0.wireOp",EDGE,"E7.32.6"),sQuery(id+"F0.wireOp",EDGE,"E7.33.3"),sQuery(id+"F0.wireOp",EDGE,"E7.33.4"),sQuery(id+"F0.wireOp",EDGE,"E7.33.5"),sQuery(id+"F0.wireOp",EDGE,"E7.33.6"),sQuery(id+"F0.wireOp",EDGE,"E7.34.3"),sQuery(id+"F0.wireOp",EDGE,"E7.34.4"),sQuery(id+"F0.wireOp",EDGE,"E7.34.5"),sQuery(id+"F0.wireOp",EDGE,"E7.34.6"),sQuery(id+"F0.wireOp",EDGE,"E7.35.3"),sQuery(id+"F0.wireOp",EDGE,"E7.35.4"),sQuery(id+"F0.wireOp",EDGE,"E7.35.5"),sQuery(id+"F0.wireOp",EDGE,"E7.35.6"),sQuery(id+"F0.wireOp",EDGE,"E7.36.3"),sQuery(id+"F0.wireOp",EDGE,"E7.36.4"),sQuery(id+"F0.wireOp",EDGE,"E7.36.5"),sQuery(id+"F0.wireOp",EDGE,"E7.36.6"),sQuery(id+"F0.wireOp",EDGE,"E7.37.3"),sQuery(id+"F0.wireOp",EDGE,"E7.37.4"),sQuery(id+"F0.wireOp",EDGE,"E7.37.5"),sQuery(id+"F0.wireOp",EDGE,"E7.37.6"),sQuery(id+"F0.wireOp",EDGE,"E7.38.3"),sQuery(id+"F0.wireOp",EDGE,"E7.38.4"),sQuery(id+"F0.wireOp",EDGE,"E7.38.5"),sQuery(id+"F0.wireOp",EDGE,"E7.38.6"),sQuery(id+"F0.wireOp",EDGE,"E7.39.3"),sQuery(id+"F0.wireOp",EDGE,"E7.39.4"),sQuery(id+"F0.wireOp",EDGE,"E7.39.5"),sQuery(id+"F0.wireOp",EDGE,"E7.39.6")])],"isStart":false});
            var sketch = newSketch(context, id + "F2", { "sketchPlane" : qUnion([Q0])});
            skCircle(sketch, "E8", {"center": v(0, 0) * mm, "radius": 10.16 * mm});
            skSolve(sketch);
        }
        {
            var Q0;
            Q0 = qSketchRegion(id + "F2", true);
            extrude(context, id + "F3", {"entities" : qUnion([Q0]), "operationType" : NewBodyOperationType.ADD, "depth" : 2.54 * mm, "offsetDistance" : 25.4 * mm});
        }
        {
            var Q0;
            Q0=makeQuery(id+"F3.opExtrude","CAP_FACE",FACE,{"disambiguationData":[OSD([sQuery(id+"F2.wireOp",EDGE,"E8")])],"isStart":false});
            var sketch = newSketch(context, id + "F4", { "sketchPlane" : qUnion([Q0])});
            skCircle(sketch, "E9", {"center": v(0, 0) * mm, "radius": 8.26 * mm});
            skSolve(sketch);
        }
        {
            var Q0;
            Q0 = qSketchRegion(id + "F4", true);
            extrude(context, id + "F5", {"entities" : qUnion([Q0]), "operationType" : NewBodyOperationType.ADD, "depth" : 7.62 * mm, "offsetDistance" : 25.4 * mm});
        }
        {
            var Q0;
            Q0=makeQuery(id+"F5.opExtrude","CAP_FACE",FACE,{"disambiguationData":[OSD([sQuery(id+"F4.wireOp",EDGE,"E9")])],"isStart":false});
            var sketch = newSketch(context, id + "F6", { "sketchPlane" : qUnion([Q0])});
            skCircle(sketch, "E10", {"center": v(0, 0) * mm, "radius": 6.99 * mm});
            skSolve(sketch);
        }
        {
            var Q0;
            Q0 = qSketchRegion(id + "F6", true);
            extrude(context, id + "F7", {"entities" : qUnion([Q0]), "operationType" : NewBodyOperationType.ADD, "depth" : 15.24 * mm, "offsetDistance" : 25.4 * mm});
        }
        {
            var Q0;
            Q0=makeQuery(id+"F7.opExtrude","CAP_FACE",FACE,{"disambiguationData":[OSD([sQuery(id+"F6.wireOp",EDGE,"E10")])],"isStart":false});
            var sketch = newSketch(context, id + "F8", { "sketchPlane" : qUnion([Q0])});
            skCircle(sketch, "E11", {"center": v(0, 0) * mm, "radius": 6.35 * mm});
            skSolve(sketch);
        }
        {
            var Q0;
            Q0 = qSketchRegion(id + "F8", true);
            extrude(context, id + "F9", {"entities" : qUnion([Q0]), "operationType" : NewBodyOperationType.ADD, "depth" : 15.24 * mm, "offsetDistance" : 25.4 * mm});
        }
        {
            var Q0;
            Q0=makeQuery(id+"F9.opExtrude","CAP_FACE",FACE,{"disambiguationData":[OSD([sQuery(id+"F8.wireOp",EDGE,"E11")])],"isStart":false});
            var sketch = newSketch(context, id + "F10", { "sketchPlane" : qUnion([Q0])});
            skCircle(sketch, "E12", {"center": v(0, 0) * mm, "radius": 6.99 * mm});
            skSolve(sketch);
        }
        {
            var Q0;
            Q0 = qSketchRegion(id + "F10", true);
            extrude(context, id + "F11", {"entities" : qUnion([Q0]), "operationType" : NewBodyOperationType.ADD, "depth" : 63.5 * mm, "offsetDistance" : 25.4 * mm});
        }
        {
            var Q0;
            Q0=makeQuery(id+"F11.opExtrude","CAP_FACE",FACE,{"disambiguationData":[OSD([sQuery(id+"F10.wireOp",EDGE,"E12")])],"isStart":false});
            var sketch = newSketch(context, id + "F12", { "sketchPlane" : qUnion([Q0])});
            skArc(sketch, "E13", {"start": v(0.66, 6.32) * mm, "mid": v(0.33, 6.34) * mm, "end": v(0, 6.35) * mm});
            skLineSegment(sketch, "E14", {"start": v(0, 0) * mm, "end": v(0, 6.35) * mm});
            skLineSegment(sketch, "E15", {"start": v(0, 0) * mm, "end": v(0.66, 6.32) * mm});
            skLineSegment(sketch, "E16", {"start": v(0, 0) * mm, "end": v(0.37, 6.98) * mm});
            skLineSegment(sketch, "E17", {"start": v(0, 6.35) * mm, "end": v(0.37, 6.98) * mm});
            skLineSegment(sketch, "E18", {"start": v(0.66, 6.32) * mm, "end": v(0.37, 6.98) * mm});
            skLineSegment(sketch, "E19.1.0", {"start": v(0, 0) * mm, "end": v(-0.66, 6.32) * mm});
            skLineSegment(sketch, "E19.1.1", {"start": v(0, 0) * mm, "end": v(-0.37, 6.98) * mm});
            skLineSegment(sketch, "E19.1.3", {"start": v(-0.66, 6.32) * mm, "end": v(-0.37, 6.98) * mm});
            skArc(sketch, "E19.1.4", {"start": v(0, 6.35) * mm, "mid": v(-0.33, 6.34) * mm, "end": v(-0.66, 6.32) * mm});
            skLineSegment(sketch, "E19.1.5", {"start": v(0, 6.35) * mm, "end": v(-0.37, 6.98) * mm});
            skLineSegment(sketch, "E19.2.0", {"start": v(0, 0) * mm, "end": v(-1.32, 6.21) * mm});
            skLineSegment(sketch, "E19.2.1", {"start": v(0, 0) * mm, "end": v(-1.1, 6.9) * mm});
            skLineSegment(sketch, "E19.2.2", {"start": v(0, 0) * mm, "end": v(-0.66, 6.32) * mm});
            skLineSegment(sketch, "E19.2.3", {"start": v(-1.32, 6.21) * mm, "end": v(-1.1, 6.9) * mm});
            skArc(sketch, "E19.2.4", {"start": v(-0.66, 6.32) * mm, "mid": v(-1, 6.27) * mm, "end": v(-1.32, 6.21) * mm});
            skLineSegment(sketch, "E19.2.5", {"start": v(-0.66, 6.32) * mm, "end": v(-1.1, 6.9) * mm});
            skLineSegment(sketch, "E19.3.0", {"start": v(0, 0) * mm, "end": v(-1.96, 6.04) * mm});
            skLineSegment(sketch, "E19.3.1", {"start": v(0, 0) * mm, "end": v(-1.8, 6.75) * mm});
            skLineSegment(sketch, "E19.3.2", {"start": v(0, 0) * mm, "end": v(-1.32, 6.21) * mm});
            skLineSegment(sketch, "E19.3.3", {"start": v(-1.96, 6.04) * mm, "end": v(-1.8, 6.75) * mm});
            skArc(sketch, "E19.3.4", {"start": v(-1.32, 6.21) * mm, "mid": v(-1.64, 6.13) * mm, "end": v(-1.96, 6.04) * mm});
            skLineSegment(sketch, "E19.3.5", {"start": v(-1.32, 6.21) * mm, "end": v(-1.8, 6.75) * mm});
            skLineSegment(sketch, "E19.4.0", {"start": v(0, 0) * mm, "end": v(-2.58, 5.8) * mm});
            skLineSegment(sketch, "E19.4.1", {"start": v(0, 0) * mm, "end": v(-2.5, 6.52) * mm});
            skLineSegment(sketch, "E19.4.2", {"start": v(0, 0) * mm, "end": v(-1.96, 6.04) * mm});
            skLineSegment(sketch, "E19.4.3", {"start": v(-2.58, 5.8) * mm, "end": v(-2.5, 6.52) * mm});
            skArc(sketch, "E19.4.4", {"start": v(-1.96, 6.04) * mm, "mid": v(-2.28, 5.93) * mm, "end": v(-2.58, 5.8) * mm});
            skLineSegment(sketch, "E19.4.5", {"start": v(-1.96, 6.04) * mm, "end": v(-2.5, 6.52) * mm});
            skLineSegment(sketch, "E19.5.0", {"start": v(0, 0) * mm, "end": v(-3.17, 5.5) * mm});
            skLineSegment(sketch, "E19.5.1", {"start": v(0, 0) * mm, "end": v(-3.17, 6.22) * mm});
            skLineSegment(sketch, "E19.5.2", {"start": v(0, 0) * mm, "end": v(-2.58, 5.8) * mm});
            skLineSegment(sketch, "E19.5.3", {"start": v(-3.17, 5.5) * mm, "end": v(-3.17, 6.22) * mm});
            skArc(sketch, "E19.5.4", {"start": v(-2.58, 5.8) * mm, "mid": v(-2.88, 5.66) * mm, "end": v(-3.17, 5.5) * mm});
            skLineSegment(sketch, "E19.5.5", {"start": v(-2.58, 5.8) * mm, "end": v(-3.17, 6.22) * mm});
            skLineSegment(sketch, "E19.6.0", {"start": v(0, 0) * mm, "end": v(-3.73, 5.14) * mm});
            skLineSegment(sketch, "E19.6.1", {"start": v(0, 0) * mm, "end": v(-3.8, 5.86) * mm});
            skLineSegment(sketch, "E19.6.2", {"start": v(0, 0) * mm, "end": v(-3.18, 5.5) * mm});
            skLineSegment(sketch, "E19.6.3", {"start": v(-3.73, 5.14) * mm, "end": v(-3.8, 5.86) * mm});
            skArc(sketch, "E19.6.4", {"start": v(-3.18, 5.5) * mm, "mid": v(-3.46, 5.33) * mm, "end": v(-3.73, 5.14) * mm});
            skLineSegment(sketch, "E19.6.5", {"start": v(-3.18, 5.5) * mm, "end": v(-3.8, 5.86) * mm});
            skLineSegment(sketch, "E19.7.0", {"start": v(0, 0) * mm, "end": v(-4.25, 4.72) * mm});
            skLineSegment(sketch, "E19.7.1", {"start": v(0, 0) * mm, "end": v(-4.4, 5.43) * mm});
            skLineSegment(sketch, "E19.7.2", {"start": v(0, 0) * mm, "end": v(-3.73, 5.14) * mm});
            skLineSegment(sketch, "E19.7.3", {"start": v(-4.25, 4.72) * mm, "end": v(-4.4, 5.43) * mm});
            skArc(sketch, "E19.7.4", {"start": v(-3.73, 5.14) * mm, "mid": v(-4, 4.93) * mm, "end": v(-4.25, 4.72) * mm});
            skLineSegment(sketch, "E19.7.5", {"start": v(-3.73, 5.14) * mm, "end": v(-4.4, 5.43) * mm});
            skLineSegment(sketch, "E19.8.0", {"start": v(0, 0) * mm, "end": v(-4.72, 4.25) * mm});
            skLineSegment(sketch, "E19.8.1", {"start": v(0, 0) * mm, "end": v(-4.94, 4.94) * mm});
            skLineSegment(sketch, "E19.8.2", {"start": v(0, 0) * mm, "end": v(-4.25, 4.72) * mm});
            skLineSegment(sketch, "E19.8.3", {"start": v(-4.72, 4.25) * mm, "end": v(-4.94, 4.94) * mm});
            skArc(sketch, "E19.8.4", {"start": v(-4.25, 4.72) * mm, "mid": v(-4.5, 4.5) * mm, "end": v(-4.72, 4.25) * mm});
            skLineSegment(sketch, "E19.8.5", {"start": v(-4.25, 4.72) * mm, "end": v(-4.94, 4.94) * mm});
            skLineSegment(sketch, "E19.9.0", {"start": v(0, 0) * mm, "end": v(-5.14, 3.73) * mm});
            skLineSegment(sketch, "E19.9.1", {"start": v(0, 0) * mm, "end": v(-5.43, 4.4) * mm});
            skLineSegment(sketch, "E19.9.2", {"start": v(0, 0) * mm, "end": v(-4.72, 4.25) * mm});
            skLineSegment(sketch, "E19.9.3", {"start": v(-5.14, 3.73) * mm, "end": v(-5.43, 4.4) * mm});
            skArc(sketch, "E19.9.4", {"start": v(-4.72, 4.25) * mm, "mid": v(-4.93, 4) * mm, "end": v(-5.14, 3.73) * mm});
            skLineSegment(sketch, "E19.9.5", {"start": v(-4.72, 4.25) * mm, "end": v(-5.43, 4.4) * mm});
            skLineSegment(sketch, "E19.10.0", {"start": v(0, 0) * mm, "end": v(-5.5, 3.18) * mm});
            skLineSegment(sketch, "E19.10.1", {"start": v(0, 0) * mm, "end": v(-5.86, 3.8) * mm});
            skLineSegment(sketch, "E19.10.2", {"start": v(0, 0) * mm, "end": v(-5.14, 3.73) * mm});
            skLineSegment(sketch, "E19.10.3", {"start": v(-5.5, 3.18) * mm, "end": v(-5.86, 3.8) * mm});
            skArc(sketch, "E19.10.4", {"start": v(-5.14, 3.73) * mm, "mid": v(-5.33, 3.46) * mm, "end": v(-5.5, 3.18) * mm});
            skLineSegment(sketch, "E19.10.5", {"start": v(-5.14, 3.73) * mm, "end": v(-5.86, 3.8) * mm});
            skLineSegment(sketch, "E19.11.0", {"start": v(0, 0) * mm, "end": v(-5.8, 2.58) * mm});
            skLineSegment(sketch, "E19.11.1", {"start": v(0, 0) * mm, "end": v(-6.22, 3.17) * mm});
            skLineSegment(sketch, "E19.11.2", {"start": v(0, 0) * mm, "end": v(-5.5, 3.18) * mm});
            skLineSegment(sketch, "E19.11.3", {"start": v(-5.8, 2.58) * mm, "end": v(-6.22, 3.17) * mm});
            skArc(sketch, "E19.11.4", {"start": v(-5.5, 3.17) * mm, "mid": v(-5.66, 2.88) * mm, "end": v(-5.8, 2.58) * mm});
            skLineSegment(sketch, "E19.11.5", {"start": v(-5.5, 3.18) * mm, "end": v(-6.22, 3.17) * mm});
            skLineSegment(sketch, "E19.12.0", {"start": v(0, 0) * mm, "end": v(-6.04, 1.96) * mm});
            skLineSegment(sketch, "E19.12.1", {"start": v(0, 0) * mm, "end": v(-6.52, 2.5) * mm});
            skLineSegment(sketch, "E19.12.2", {"start": v(0, 0) * mm, "end": v(-5.8, 2.58) * mm});
            skLineSegment(sketch, "E19.12.3", {"start": v(-6.04, 1.96) * mm, "end": v(-6.52, 2.5) * mm});
            skArc(sketch, "E19.12.4", {"start": v(-5.8, 2.58) * mm, "mid": v(-5.93, 2.28) * mm, "end": v(-6.04, 1.96) * mm});
            skLineSegment(sketch, "E19.12.5", {"start": v(-5.8, 2.58) * mm, "end": v(-6.52, 2.5) * mm});
            skLineSegment(sketch, "E19.13.0", {"start": v(0, 0) * mm, "end": v(-6.21, 1.32) * mm});
            skLineSegment(sketch, "E19.13.1", {"start": v(0, 0) * mm, "end": v(-6.75, 1.8) * mm});
            skLineSegment(sketch, "E19.13.2", {"start": v(0, 0) * mm, "end": v(-6.04, 1.96) * mm});
            skLineSegment(sketch, "E19.13.3", {"start": v(-6.21, 1.32) * mm, "end": v(-6.75, 1.8) * mm});
            skArc(sketch, "E19.13.4", {"start": v(-6.04, 1.96) * mm, "mid": v(-6.13, 1.64) * mm, "end": v(-6.21, 1.32) * mm});
            skLineSegment(sketch, "E19.13.5", {"start": v(-6.04, 1.96) * mm, "end": v(-6.75, 1.8) * mm});
            skLineSegment(sketch, "E19.14.0", {"start": v(0, 0) * mm, "end": v(-6.32, 0.66) * mm});
            skLineSegment(sketch, "E19.14.1", {"start": v(0, 0) * mm, "end": v(-6.9, 1.1) * mm});
            skLineSegment(sketch, "E19.14.2", {"start": v(0, 0) * mm, "end": v(-6.21, 1.32) * mm});
            skLineSegment(sketch, "E19.14.3", {"start": v(-6.32, 0.66) * mm, "end": v(-6.9, 1.1) * mm});
            skArc(sketch, "E19.14.4", {"start": v(-6.21, 1.32) * mm, "mid": v(-6.27, 1) * mm, "end": v(-6.32, 0.66) * mm});
            skLineSegment(sketch, "E19.14.5", {"start": v(-6.21, 1.32) * mm, "end": v(-6.9, 1.1) * mm});
            skLineSegment(sketch, "E19.15.0", {"start": v(0, 0) * mm, "end": v(-6.35, 0) * mm});
            skLineSegment(sketch, "E19.15.1", {"start": v(0, 0) * mm, "end": v(-6.98, 0.37) * mm});
            skLineSegment(sketch, "E19.15.2", {"start": v(0, 0) * mm, "end": v(-6.32, 0.66) * mm});
            skLineSegment(sketch, "E19.15.3", {"start": v(-6.35, 0) * mm, "end": v(-6.98, 0.37) * mm});
            skArc(sketch, "E19.15.4", {"start": v(-6.32, 0.66) * mm, "mid": v(-6.34, 0.33) * mm, "end": v(-6.35, 0) * mm});
            skLineSegment(sketch, "E19.15.5", {"start": v(-6.32, 0.66) * mm, "end": v(-6.98, 0.37) * mm});
            skLineSegment(sketch, "E19.16.0", {"start": v(0, 0) * mm, "end": v(-6.32, -0.66) * mm});
            skLineSegment(sketch, "E19.16.1", {"start": v(0, 0) * mm, "end": v(-6.98, -0.37) * mm});
            skLineSegment(sketch, "E19.16.2", {"start": v(0, 0) * mm, "end": v(-6.35, 0) * mm});
            skLineSegment(sketch, "E19.16.3", {"start": v(-6.32, -0.66) * mm, "end": v(-6.98, -0.37) * mm});
            skArc(sketch, "E19.16.4", {"start": v(-6.35, 0) * mm, "mid": v(-6.34, -0.33) * mm, "end": v(-6.32, -0.66) * mm});
            skLineSegment(sketch, "E19.16.5", {"start": v(-6.35, 0) * mm, "end": v(-6.98, -0.37) * mm});
            skLineSegment(sketch, "E19.17.0", {"start": v(0, 0) * mm, "end": v(-6.21, -1.32) * mm});
            skLineSegment(sketch, "E19.17.1", {"start": v(0, 0) * mm, "end": v(-6.9, -1.1) * mm});
            skLineSegment(sketch, "E19.17.2", {"start": v(0, 0) * mm, "end": v(-6.32, -0.66) * mm});
            skLineSegment(sketch, "E19.17.3", {"start": v(-6.21, -1.32) * mm, "end": v(-6.9, -1.1) * mm});
            skArc(sketch, "E19.17.4", {"start": v(-6.32, -0.66) * mm, "mid": v(-6.27, -1) * mm, "end": v(-6.21, -1.32) * mm});
            skLineSegment(sketch, "E19.17.5", {"start": v(-6.32, -0.66) * mm, "end": v(-6.9, -1.1) * mm});
            skLineSegment(sketch, "E19.18.0", {"start": v(0, 0) * mm, "end": v(-6.04, -1.96) * mm});
            skLineSegment(sketch, "E19.18.1", {"start": v(0, 0) * mm, "end": v(-6.75, -1.8) * mm});
            skLineSegment(sketch, "E19.18.2", {"start": v(0, 0) * mm, "end": v(-6.21, -1.32) * mm});
            skLineSegment(sketch, "E19.18.3", {"start": v(-6.04, -1.96) * mm, "end": v(-6.75, -1.8) * mm});
            skArc(sketch, "E19.18.4", {"start": v(-6.21, -1.32) * mm, "mid": v(-6.13, -1.64) * mm, "end": v(-6.04, -1.96) * mm});
            skLineSegment(sketch, "E19.18.5", {"start": v(-6.21, -1.32) * mm, "end": v(-6.75, -1.8) * mm});
            skLineSegment(sketch, "E19.19.0", {"start": v(0, 0) * mm, "end": v(-5.8, -2.58) * mm});
            skLineSegment(sketch, "E19.19.1", {"start": v(0, 0) * mm, "end": v(-6.52, -2.5) * mm});
            skLineSegment(sketch, "E19.19.2", {"start": v(0, 0) * mm, "end": v(-6.04, -1.96) * mm});
            skLineSegment(sketch, "E19.19.3", {"start": v(-5.8, -2.58) * mm, "end": v(-6.52, -2.5) * mm});
            skArc(sketch, "E19.19.4", {"start": v(-6.04, -1.96) * mm, "mid": v(-5.93, -2.28) * mm, "end": v(-5.8, -2.58) * mm});
            skLineSegment(sketch, "E19.19.5", {"start": v(-6.04, -1.96) * mm, "end": v(-6.52, -2.5) * mm});
            skLineSegment(sketch, "E19.20.0", {"start": v(0, 0) * mm, "end": v(-5.5, -3.18) * mm});
            skLineSegment(sketch, "E19.20.1", {"start": v(0, 0) * mm, "end": v(-6.22, -3.17) * mm});
            skLineSegment(sketch, "E19.20.2", {"start": v(0, 0) * mm, "end": v(-5.8, -2.58) * mm});
            skLineSegment(sketch, "E19.20.3", {"start": v(-5.5, -3.17) * mm, "end": v(-6.22, -3.17) * mm});
            skArc(sketch, "E19.20.4", {"start": v(-5.8, -2.58) * mm, "mid": v(-5.66, -2.88) * mm, "end": v(-5.5, -3.17) * mm});
            skLineSegment(sketch, "E19.20.5", {"start": v(-5.8, -2.58) * mm, "end": v(-6.22, -3.17) * mm});
            skLineSegment(sketch, "E19.21.0", {"start": v(0, 0) * mm, "end": v(-5.14, -3.73) * mm});
            skLineSegment(sketch, "E19.21.1", {"start": v(0, 0) * mm, "end": v(-5.86, -3.8) * mm});
            skLineSegment(sketch, "E19.21.2", {"start": v(0, 0) * mm, "end": v(-5.5, -3.18) * mm});
            skLineSegment(sketch, "E19.21.3", {"start": v(-5.14, -3.73) * mm, "end": v(-5.86, -3.8) * mm});
            skArc(sketch, "E19.21.4", {"start": v(-5.5, -3.18) * mm, "mid": v(-5.33, -3.46) * mm, "end": v(-5.14, -3.73) * mm});
            skLineSegment(sketch, "E19.21.5", {"start": v(-5.5, -3.18) * mm, "end": v(-5.86, -3.8) * mm});
            skLineSegment(sketch, "E19.22.0", {"start": v(0, 0) * mm, "end": v(-4.72, -4.25) * mm});
            skLineSegment(sketch, "E19.22.1", {"start": v(0, 0) * mm, "end": v(-5.43, -4.4) * mm});
            skLineSegment(sketch, "E19.22.2", {"start": v(0, 0) * mm, "end": v(-5.14, -3.73) * mm});
            skLineSegment(sketch, "E19.22.3", {"start": v(-4.72, -4.25) * mm, "end": v(-5.43, -4.4) * mm});
            skArc(sketch, "E19.22.4", {"start": v(-5.14, -3.73) * mm, "mid": v(-4.93, -4) * mm, "end": v(-4.72, -4.25) * mm});
            skLineSegment(sketch, "E19.22.5", {"start": v(-5.14, -3.73) * mm, "end": v(-5.43, -4.4) * mm});
            skLineSegment(sketch, "E19.23.0", {"start": v(0, 0) * mm, "end": v(-4.25, -4.72) * mm});
            skLineSegment(sketch, "E19.23.1", {"start": v(0, 0) * mm, "end": v(-4.94, -4.94) * mm});
            skLineSegment(sketch, "E19.23.2", {"start": v(0, 0) * mm, "end": v(-4.72, -4.25) * mm});
            skLineSegment(sketch, "E19.23.3", {"start": v(-4.25, -4.72) * mm, "end": v(-4.94, -4.94) * mm});
            skArc(sketch, "E19.23.4", {"start": v(-4.72, -4.25) * mm, "mid": v(-4.5, -4.5) * mm, "end": v(-4.25, -4.72) * mm});
            skLineSegment(sketch, "E19.23.5", {"start": v(-4.72, -4.25) * mm, "end": v(-4.94, -4.94) * mm});
            skLineSegment(sketch, "E19.24.0", {"start": v(0, 0) * mm, "end": v(-3.73, -5.14) * mm});
            skLineSegment(sketch, "E19.24.1", {"start": v(0, 0) * mm, "end": v(-4.4, -5.43) * mm});
            skLineSegment(sketch, "E19.24.2", {"start": v(0, 0) * mm, "end": v(-4.25, -4.72) * mm});
            skLineSegment(sketch, "E19.24.3", {"start": v(-3.73, -5.14) * mm, "end": v(-4.4, -5.43) * mm});
            skArc(sketch, "E19.24.4", {"start": v(-4.25, -4.72) * mm, "mid": v(-4, -4.93) * mm, "end": v(-3.73, -5.14) * mm});
            skLineSegment(sketch, "E19.24.5", {"start": v(-4.25, -4.72) * mm, "end": v(-4.4, -5.43) * mm});
            skLineSegment(sketch, "E19.25.0", {"start": v(0, 0) * mm, "end": v(-3.17, -5.5) * mm});
            skLineSegment(sketch, "E19.25.1", {"start": v(0, 0) * mm, "end": v(-3.8, -5.86) * mm});
            skLineSegment(sketch, "E19.25.2", {"start": v(0, 0) * mm, "end": v(-3.73, -5.14) * mm});
            skLineSegment(sketch, "E19.25.3", {"start": v(-3.17, -5.5) * mm, "end": v(-3.8, -5.86) * mm});
            skArc(sketch, "E19.25.4", {"start": v(-3.73, -5.14) * mm, "mid": v(-3.46, -5.33) * mm, "end": v(-3.17, -5.5) * mm});
            skLineSegment(sketch, "E19.25.5", {"start": v(-3.73, -5.14) * mm, "end": v(-3.8, -5.86) * mm});
            skLineSegment(sketch, "E19.26.0", {"start": v(0, 0) * mm, "end": v(-2.58, -5.8) * mm});
            skLineSegment(sketch, "E19.26.1", {"start": v(0, 0) * mm, "end": v(-3.17, -6.22) * mm});
            skLineSegment(sketch, "E19.26.2", {"start": v(0, 0) * mm, "end": v(-3.17, -5.5) * mm});
            skLineSegment(sketch, "E19.26.3", {"start": v(-2.58, -5.8) * mm, "end": v(-3.17, -6.22) * mm});
            skArc(sketch, "E19.26.4", {"start": v(-3.17, -5.5) * mm, "mid": v(-2.88, -5.66) * mm, "end": v(-2.58, -5.8) * mm});
            skLineSegment(sketch, "E19.26.5", {"start": v(-3.17, -5.5) * mm, "end": v(-3.17, -6.22) * mm});
            skLineSegment(sketch, "E19.27.0", {"start": v(0, 0) * mm, "end": v(-1.96, -6.04) * mm});
            skLineSegment(sketch, "E19.27.1", {"start": v(0, 0) * mm, "end": v(-2.5, -6.52) * mm});
            skLineSegment(sketch, "E19.27.2", {"start": v(0, 0) * mm, "end": v(-2.58, -5.8) * mm});
            skLineSegment(sketch, "E19.27.3", {"start": v(-1.96, -6.04) * mm, "end": v(-2.5, -6.52) * mm});
            skArc(sketch, "E19.27.4", {"start": v(-2.58, -5.8) * mm, "mid": v(-2.28, -5.93) * mm, "end": v(-1.96, -6.04) * mm});
            skLineSegment(sketch, "E19.27.5", {"start": v(-2.58, -5.8) * mm, "end": v(-2.5, -6.52) * mm});
            skLineSegment(sketch, "E19.28.0", {"start": v(0, 0) * mm, "end": v(-1.32, -6.21) * mm});
            skLineSegment(sketch, "E19.28.1", {"start": v(0, 0) * mm, "end": v(-1.8, -6.75) * mm});
            skLineSegment(sketch, "E19.28.2", {"start": v(0, 0) * mm, "end": v(-1.96, -6.04) * mm});
            skLineSegment(sketch, "E19.28.3", {"start": v(-1.32, -6.21) * mm, "end": v(-1.8, -6.75) * mm});
            skArc(sketch, "E19.28.4", {"start": v(-1.96, -6.04) * mm, "mid": v(-1.64, -6.13) * mm, "end": v(-1.32, -6.21) * mm});
            skLineSegment(sketch, "E19.28.5", {"start": v(-1.96, -6.04) * mm, "end": v(-1.8, -6.75) * mm});
            skLineSegment(sketch, "E19.29.0", {"start": v(0, 0) * mm, "end": v(-0.66, -6.32) * mm});
            skLineSegment(sketch, "E19.29.1", {"start": v(0, 0) * mm, "end": v(-1.1, -6.9) * mm});
            skLineSegment(sketch, "E19.29.2", {"start": v(0, 0) * mm, "end": v(-1.32, -6.21) * mm});
            skLineSegment(sketch, "E19.29.3", {"start": v(-0.66, -6.32) * mm, "end": v(-1.1, -6.9) * mm});
            skArc(sketch, "E19.29.4", {"start": v(-1.32, -6.21) * mm, "mid": v(-1, -6.27) * mm, "end": v(-0.66, -6.32) * mm});
            skLineSegment(sketch, "E19.29.5", {"start": v(-1.32, -6.21) * mm, "end": v(-1.1, -6.9) * mm});
            skLineSegment(sketch, "E19.30.0", {"start": v(0, 0) * mm, "end": v(0, -6.35) * mm});
            skLineSegment(sketch, "E19.30.1", {"start": v(0, 0) * mm, "end": v(-0.37, -6.98) * mm});
            skLineSegment(sketch, "E19.30.2", {"start": v(0, 0) * mm, "end": v(-0.66, -6.32) * mm});
            skLineSegment(sketch, "E19.30.3", {"start": v(0, -6.35) * mm, "end": v(-0.37, -6.98) * mm});
            skArc(sketch, "E19.30.4", {"start": v(-0.66, -6.32) * mm, "mid": v(-0.33, -6.34) * mm, "end": v(0, -6.35) * mm});
            skLineSegment(sketch, "E19.30.5", {"start": v(-0.66, -6.32) * mm, "end": v(-0.37, -6.98) * mm});
            skLineSegment(sketch, "E19.31.0", {"start": v(0, 0) * mm, "end": v(0.66, -6.32) * mm});
            skLineSegment(sketch, "E19.31.1", {"start": v(0, 0) * mm, "end": v(0.37, -6.98) * mm});
            skLineSegment(sketch, "E19.31.2", {"start": v(0, 0) * mm, "end": v(0, -6.35) * mm});
            skLineSegment(sketch, "E19.31.3", {"start": v(0.66, -6.32) * mm, "end": v(0.37, -6.98) * mm});
            skArc(sketch, "E19.31.4", {"start": v(0, -6.35) * mm, "mid": v(0.33, -6.34) * mm, "end": v(0.66, -6.32) * mm});
            skLineSegment(sketch, "E19.31.5", {"start": v(0, -6.35) * mm, "end": v(0.37, -6.98) * mm});
            skLineSegment(sketch, "E19.32.0", {"start": v(0, 0) * mm, "end": v(1.32, -6.21) * mm});
            skLineSegment(sketch, "E19.32.1", {"start": v(0, 0) * mm, "end": v(1.1, -6.9) * mm});
            skLineSegment(sketch, "E19.32.2", {"start": v(0, 0) * mm, "end": v(0.66, -6.32) * mm});
            skLineSegment(sketch, "E19.32.3", {"start": v(1.32, -6.21) * mm, "end": v(1.1, -6.9) * mm});
            skArc(sketch, "E19.32.4", {"start": v(0.66, -6.32) * mm, "mid": v(1, -6.27) * mm, "end": v(1.32, -6.21) * mm});
            skLineSegment(sketch, "E19.32.5", {"start": v(0.66, -6.32) * mm, "end": v(1.1, -6.9) * mm});
            skLineSegment(sketch, "E19.33.0", {"start": v(0, 0) * mm, "end": v(1.96, -6.04) * mm});
            skLineSegment(sketch, "E19.33.1", {"start": v(0, 0) * mm, "end": v(1.8, -6.75) * mm});
            skLineSegment(sketch, "E19.33.2", {"start": v(0, 0) * mm, "end": v(1.32, -6.21) * mm});
            skLineSegment(sketch, "E19.33.3", {"start": v(1.96, -6.04) * mm, "end": v(1.8, -6.75) * mm});
            skArc(sketch, "E19.33.4", {"start": v(1.32, -6.21) * mm, "mid": v(1.64, -6.13) * mm, "end": v(1.96, -6.04) * mm});
            skLineSegment(sketch, "E19.33.5", {"start": v(1.32, -6.21) * mm, "end": v(1.8, -6.75) * mm});
            skLineSegment(sketch, "E19.34.0", {"start": v(0, 0) * mm, "end": v(2.58, -5.8) * mm});
            skLineSegment(sketch, "E19.34.1", {"start": v(0, 0) * mm, "end": v(2.5, -6.52) * mm});
            skLineSegment(sketch, "E19.34.2", {"start": v(0, 0) * mm, "end": v(1.96, -6.04) * mm});
            skLineSegment(sketch, "E19.34.3", {"start": v(2.58, -5.8) * mm, "end": v(2.5, -6.52) * mm});
            skArc(sketch, "E19.34.4", {"start": v(1.96, -6.04) * mm, "mid": v(2.28, -5.93) * mm, "end": v(2.58, -5.8) * mm});
            skLineSegment(sketch, "E19.34.5", {"start": v(1.96, -6.04) * mm, "end": v(2.5, -6.52) * mm});
            skLineSegment(sketch, "E19.35.0", {"start": v(0, 0) * mm, "end": v(3.17, -5.5) * mm});
            skLineSegment(sketch, "E19.35.1", {"start": v(0, 0) * mm, "end": v(3.17, -6.22) * mm});
            skLineSegment(sketch, "E19.35.2", {"start": v(0, 0) * mm, "end": v(2.58, -5.8) * mm});
            skLineSegment(sketch, "E19.35.3", {"start": v(3.17, -5.5) * mm, "end": v(3.17, -6.22) * mm});
            skArc(sketch, "E19.35.4", {"start": v(2.58, -5.8) * mm, "mid": v(2.88, -5.66) * mm, "end": v(3.17, -5.5) * mm});
            skLineSegment(sketch, "E19.35.5", {"start": v(2.58, -5.8) * mm, "end": v(3.17, -6.22) * mm});
            skLineSegment(sketch, "E19.36.0", {"start": v(0, 0) * mm, "end": v(3.73, -5.14) * mm});
            skLineSegment(sketch, "E19.36.1", {"start": v(0, 0) * mm, "end": v(3.8, -5.86) * mm});
            skLineSegment(sketch, "E19.36.2", {"start": v(0, 0) * mm, "end": v(3.18, -5.5) * mm});
            skLineSegment(sketch, "E19.36.3", {"start": v(3.73, -5.14) * mm, "end": v(3.8, -5.86) * mm});
            skArc(sketch, "E19.36.4", {"start": v(3.18, -5.5) * mm, "mid": v(3.46, -5.33) * mm, "end": v(3.73, -5.14) * mm});
            skLineSegment(sketch, "E19.36.5", {"start": v(3.18, -5.5) * mm, "end": v(3.8, -5.86) * mm});
            skLineSegment(sketch, "E19.37.0", {"start": v(0, 0) * mm, "end": v(4.25, -4.72) * mm});
            skLineSegment(sketch, "E19.37.1", {"start": v(0, 0) * mm, "end": v(4.4, -5.43) * mm});
            skLineSegment(sketch, "E19.37.2", {"start": v(0, 0) * mm, "end": v(3.73, -5.14) * mm});
            skLineSegment(sketch, "E19.37.3", {"start": v(4.25, -4.72) * mm, "end": v(4.4, -5.43) * mm});
            skArc(sketch, "E19.37.4", {"start": v(3.73, -5.14) * mm, "mid": v(4, -4.93) * mm, "end": v(4.25, -4.72) * mm});
            skLineSegment(sketch, "E19.37.5", {"start": v(3.73, -5.14) * mm, "end": v(4.4, -5.43) * mm});
            skLineSegment(sketch, "E19.38.0", {"start": v(0, 0) * mm, "end": v(4.72, -4.25) * mm});
            skLineSegment(sketch, "E19.38.1", {"start": v(0, 0) * mm, "end": v(4.94, -4.94) * mm});
            skLineSegment(sketch, "E19.38.2", {"start": v(0, 0) * mm, "end": v(4.25, -4.72) * mm});
            skLineSegment(sketch, "E19.38.3", {"start": v(4.72, -4.25) * mm, "end": v(4.94, -4.94) * mm});
            skArc(sketch, "E19.38.4", {"start": v(4.25, -4.72) * mm, "mid": v(4.5, -4.5) * mm, "end": v(4.72, -4.25) * mm});
            skLineSegment(sketch, "E19.38.5", {"start": v(4.25, -4.72) * mm, "end": v(4.94, -4.94) * mm});
            skLineSegment(sketch, "E19.39.0", {"start": v(0, 0) * mm, "end": v(5.14, -3.73) * mm});
            skLineSegment(sketch, "E19.39.1", {"start": v(0, 0) * mm, "end": v(5.43, -4.4) * mm});
            skLineSegment(sketch, "E19.39.2", {"start": v(0, 0) * mm, "end": v(4.72, -4.25) * mm});
            skLineSegment(sketch, "E19.39.3", {"start": v(5.14, -3.73) * mm, "end": v(5.43, -4.4) * mm});
            skArc(sketch, "E19.39.4", {"start": v(4.72, -4.25) * mm, "mid": v(4.93, -4) * mm, "end": v(5.14, -3.73) * mm});
            skLineSegment(sketch, "E19.39.5", {"start": v(4.72, -4.25) * mm, "end": v(5.43, -4.4) * mm});
            skLineSegment(sketch, "E19.40.0", {"start": v(0, 0) * mm, "end": v(5.5, -3.18) * mm});
            skLineSegment(sketch, "E19.40.1", {"start": v(0, 0) * mm, "end": v(5.86, -3.8) * mm});
            skLineSegment(sketch, "E19.40.2", {"start": v(0, 0) * mm, "end": v(5.14, -3.73) * mm});
            skLineSegment(sketch, "E19.40.3", {"start": v(5.5, -3.18) * mm, "end": v(5.86, -3.8) * mm});
            skArc(sketch, "E19.40.4", {"start": v(5.14, -3.73) * mm, "mid": v(5.33, -3.46) * mm, "end": v(5.5, -3.18) * mm});
            skLineSegment(sketch, "E19.40.5", {"start": v(5.14, -3.73) * mm, "end": v(5.86, -3.8) * mm});
            skLineSegment(sketch, "E19.41.0", {"start": v(0, 0) * mm, "end": v(5.8, -2.58) * mm});
            skLineSegment(sketch, "E19.41.1", {"start": v(0, 0) * mm, "end": v(6.22, -3.17) * mm});
            skLineSegment(sketch, "E19.41.2", {"start": v(0, 0) * mm, "end": v(5.5, -3.18) * mm});
            skLineSegment(sketch, "E19.41.3", {"start": v(5.8, -2.58) * mm, "end": v(6.22, -3.17) * mm});
            skArc(sketch, "E19.41.4", {"start": v(5.5, -3.18) * mm, "mid": v(5.66, -2.88) * mm, "end": v(5.8, -2.58) * mm});
            skLineSegment(sketch, "E19.41.5", {"start": v(5.5, -3.18) * mm, "end": v(6.22, -3.17) * mm});
            skLineSegment(sketch, "E19.42.0", {"start": v(0, 0) * mm, "end": v(6.04, -1.96) * mm});
            skLineSegment(sketch, "E19.42.1", {"start": v(0, 0) * mm, "end": v(6.52, -2.5) * mm});
            skLineSegment(sketch, "E19.42.2", {"start": v(0, 0) * mm, "end": v(5.8, -2.58) * mm});
            skLineSegment(sketch, "E19.42.3", {"start": v(6.04, -1.96) * mm, "end": v(6.52, -2.5) * mm});
            skArc(sketch, "E19.42.4", {"start": v(5.8, -2.58) * mm, "mid": v(5.93, -2.28) * mm, "end": v(6.04, -1.96) * mm});
            skLineSegment(sketch, "E19.42.5", {"start": v(5.8, -2.58) * mm, "end": v(6.52, -2.5) * mm});
            skLineSegment(sketch, "E19.43.0", {"start": v(0, 0) * mm, "end": v(6.21, -1.32) * mm});
            skLineSegment(sketch, "E19.43.1", {"start": v(0, 0) * mm, "end": v(6.75, -1.8) * mm});
            skLineSegment(sketch, "E19.43.2", {"start": v(0, 0) * mm, "end": v(6.04, -1.96) * mm});
            skLineSegment(sketch, "E19.43.3", {"start": v(6.21, -1.32) * mm, "end": v(6.75, -1.8) * mm});
            skArc(sketch, "E19.43.4", {"start": v(6.04, -1.96) * mm, "mid": v(6.13, -1.64) * mm, "end": v(6.21, -1.32) * mm});
            skLineSegment(sketch, "E19.43.5", {"start": v(6.04, -1.96) * mm, "end": v(6.75, -1.8) * mm});
            skLineSegment(sketch, "E19.44.0", {"start": v(0, 0) * mm, "end": v(6.32, -0.66) * mm});
            skLineSegment(sketch, "E19.44.1", {"start": v(0, 0) * mm, "end": v(6.9, -1.1) * mm});
            skLineSegment(sketch, "E19.44.2", {"start": v(0, 0) * mm, "end": v(6.21, -1.32) * mm});
            skLineSegment(sketch, "E19.44.3", {"start": v(6.32, -0.66) * mm, "end": v(6.9, -1.1) * mm});
            skArc(sketch, "E19.44.4", {"start": v(6.21, -1.32) * mm, "mid": v(6.27, -1) * mm, "end": v(6.32, -0.66) * mm});
            skLineSegment(sketch, "E19.44.5", {"start": v(6.21, -1.32) * mm, "end": v(6.9, -1.1) * mm});
            skLineSegment(sketch, "E19.45.0", {"start": v(0, 0) * mm, "end": v(6.35, 0) * mm});
            skLineSegment(sketch, "E19.45.1", {"start": v(0, 0) * mm, "end": v(6.98, -0.37) * mm});
            skLineSegment(sketch, "E19.45.2", {"start": v(0, 0) * mm, "end": v(6.32, -0.66) * mm});
            skLineSegment(sketch, "E19.45.3", {"start": v(6.35, 0) * mm, "end": v(6.98, -0.37) * mm});
            skArc(sketch, "E19.45.4", {"start": v(6.32, -0.66) * mm, "mid": v(6.34, -0.33) * mm, "end": v(6.35, 0) * mm});
            skLineSegment(sketch, "E19.45.5", {"start": v(6.32, -0.66) * mm, "end": v(6.98, -0.37) * mm});
            skLineSegment(sketch, "E19.46.0", {"start": v(0, 0) * mm, "end": v(6.32, 0.66) * mm});
            skLineSegment(sketch, "E19.46.1", {"start": v(0, 0) * mm, "end": v(6.98, 0.37) * mm});
            skLineSegment(sketch, "E19.46.2", {"start": v(0, 0) * mm, "end": v(6.35, 0) * mm});
            skLineSegment(sketch, "E19.46.3", {"start": v(6.32, 0.66) * mm, "end": v(6.98, 0.37) * mm});
            skArc(sketch, "E19.46.4", {"start": v(6.35, 0) * mm, "mid": v(6.34, 0.33) * mm, "end": v(6.32, 0.66) * mm});
            skLineSegment(sketch, "E19.46.5", {"start": v(6.35, 0) * mm, "end": v(6.98, 0.37) * mm});
            skLineSegment(sketch, "E19.47.0", {"start": v(0, 0) * mm, "end": v(6.21, 1.32) * mm});
            skLineSegment(sketch, "E19.47.1", {"start": v(0, 0) * mm, "end": v(6.9, 1.1) * mm});
            skLineSegment(sketch, "E19.47.2", {"start": v(0, 0) * mm, "end": v(6.32, 0.66) * mm});
            skLineSegment(sketch, "E19.47.3", {"start": v(6.21, 1.32) * mm, "end": v(6.9, 1.1) * mm});
            skArc(sketch, "E19.47.4", {"start": v(6.32, 0.66) * mm, "mid": v(6.27, 1) * mm, "end": v(6.21, 1.32) * mm});
            skLineSegment(sketch, "E19.47.5", {"start": v(6.32, 0.66) * mm, "end": v(6.9, 1.1) * mm});
            skLineSegment(sketch, "E19.48.0", {"start": v(0, 0) * mm, "end": v(6.04, 1.96) * mm});
            skLineSegment(sketch, "E19.48.1", {"start": v(0, 0) * mm, "end": v(6.75, 1.8) * mm});
            skLineSegment(sketch, "E19.48.2", {"start": v(0, 0) * mm, "end": v(6.21, 1.32) * mm});
            skLineSegment(sketch, "E19.48.3", {"start": v(6.04, 1.96) * mm, "end": v(6.75, 1.8) * mm});
            skArc(sketch, "E19.48.4", {"start": v(6.21, 1.32) * mm, "mid": v(6.13, 1.64) * mm, "end": v(6.04, 1.96) * mm});
            skLineSegment(sketch, "E19.48.5", {"start": v(6.21, 1.32) * mm, "end": v(6.75, 1.8) * mm});
            skLineSegment(sketch, "E19.49.0", {"start": v(0, 0) * mm, "end": v(5.8, 2.58) * mm});
            skLineSegment(sketch, "E19.49.1", {"start": v(0, 0) * mm, "end": v(6.52, 2.5) * mm});
            skLineSegment(sketch, "E19.49.2", {"start": v(0, 0) * mm, "end": v(6.04, 1.96) * mm});
            skLineSegment(sketch, "E19.49.3", {"start": v(5.8, 2.58) * mm, "end": v(6.52, 2.5) * mm});
            skArc(sketch, "E19.49.4", {"start": v(6.04, 1.96) * mm, "mid": v(5.93, 2.28) * mm, "end": v(5.8, 2.58) * mm});
            skLineSegment(sketch, "E19.49.5", {"start": v(6.04, 1.96) * mm, "end": v(6.52, 2.5) * mm});
            skLineSegment(sketch, "E19.50.0", {"start": v(0, 0) * mm, "end": v(5.5, 3.18) * mm});
            skLineSegment(sketch, "E19.50.1", {"start": v(0, 0) * mm, "end": v(6.22, 3.17) * mm});
            skLineSegment(sketch, "E19.50.2", {"start": v(0, 0) * mm, "end": v(5.8, 2.58) * mm});
            skLineSegment(sketch, "E19.50.3", {"start": v(5.5, 3.18) * mm, "end": v(6.22, 3.17) * mm});
            skArc(sketch, "E19.50.4", {"start": v(5.8, 2.58) * mm, "mid": v(5.66, 2.88) * mm, "end": v(5.5, 3.18) * mm});
            skLineSegment(sketch, "E19.50.5", {"start": v(5.8, 2.58) * mm, "end": v(6.22, 3.17) * mm});
            skLineSegment(sketch, "E19.51.0", {"start": v(0, 0) * mm, "end": v(5.14, 3.73) * mm});
            skLineSegment(sketch, "E19.51.1", {"start": v(0, 0) * mm, "end": v(5.86, 3.8) * mm});
            skLineSegment(sketch, "E19.51.2", {"start": v(0, 0) * mm, "end": v(5.5, 3.18) * mm});
            skLineSegment(sketch, "E19.51.3", {"start": v(5.14, 3.73) * mm, "end": v(5.86, 3.8) * mm});
            skArc(sketch, "E19.51.4", {"start": v(5.5, 3.18) * mm, "mid": v(5.33, 3.46) * mm, "end": v(5.14, 3.73) * mm});
            skLineSegment(sketch, "E19.51.5", {"start": v(5.5, 3.18) * mm, "end": v(5.86, 3.8) * mm});
            skLineSegment(sketch, "E19.52.0", {"start": v(0, 0) * mm, "end": v(4.72, 4.25) * mm});
            skLineSegment(sketch, "E19.52.1", {"start": v(0, 0) * mm, "end": v(5.43, 4.4) * mm});
            skLineSegment(sketch, "E19.52.2", {"start": v(0, 0) * mm, "end": v(5.14, 3.73) * mm});
            skLineSegment(sketch, "E19.52.3", {"start": v(4.72, 4.25) * mm, "end": v(5.43, 4.4) * mm});
            skArc(sketch, "E19.52.4", {"start": v(5.14, 3.73) * mm, "mid": v(4.93, 4) * mm, "end": v(4.72, 4.25) * mm});
            skLineSegment(sketch, "E19.52.5", {"start": v(5.14, 3.73) * mm, "end": v(5.43, 4.4) * mm});
            skLineSegment(sketch, "E19.53.0", {"start": v(0, 0) * mm, "end": v(4.25, 4.72) * mm});
            skLineSegment(sketch, "E19.53.1", {"start": v(0, 0) * mm, "end": v(4.94, 4.94) * mm});
            skLineSegment(sketch, "E19.53.2", {"start": v(0, 0) * mm, "end": v(4.72, 4.25) * mm});
            skLineSegment(sketch, "E19.53.3", {"start": v(4.25, 4.72) * mm, "end": v(4.94, 4.94) * mm});
            skArc(sketch, "E19.53.4", {"start": v(4.72, 4.25) * mm, "mid": v(4.5, 4.5) * mm, "end": v(4.25, 4.72) * mm});
            skLineSegment(sketch, "E19.53.5", {"start": v(4.72, 4.25) * mm, "end": v(4.94, 4.94) * mm});
            skLineSegment(sketch, "E19.54.0", {"start": v(0, 0) * mm, "end": v(3.73, 5.14) * mm});
            skLineSegment(sketch, "E19.54.1", {"start": v(0, 0) * mm, "end": v(4.4, 5.43) * mm});
            skLineSegment(sketch, "E19.54.2", {"start": v(0, 0) * mm, "end": v(4.25, 4.72) * mm});
            skLineSegment(sketch, "E19.54.3", {"start": v(3.73, 5.14) * mm, "end": v(4.4, 5.43) * mm});
            skArc(sketch, "E19.54.4", {"start": v(4.25, 4.72) * mm, "mid": v(4, 4.93) * mm, "end": v(3.73, 5.14) * mm});
            skLineSegment(sketch, "E19.54.5", {"start": v(4.25, 4.72) * mm, "end": v(4.4, 5.43) * mm});
            skLineSegment(sketch, "E19.55.0", {"start": v(0, 0) * mm, "end": v(3.17, 5.5) * mm});
            skLineSegment(sketch, "E19.55.1", {"start": v(0, 0) * mm, "end": v(3.8, 5.86) * mm});
            skLineSegment(sketch, "E19.55.2", {"start": v(0, 0) * mm, "end": v(3.73, 5.14) * mm});
            skLineSegment(sketch, "E19.55.3", {"start": v(3.17, 5.5) * mm, "end": v(3.8, 5.86) * mm});
            skArc(sketch, "E19.55.4", {"start": v(3.73, 5.14) * mm, "mid": v(3.46, 5.33) * mm, "end": v(3.17, 5.5) * mm});
            skLineSegment(sketch, "E19.55.5", {"start": v(3.73, 5.14) * mm, "end": v(3.8, 5.86) * mm});
            skLineSegment(sketch, "E19.56.0", {"start": v(0, 0) * mm, "end": v(2.58, 5.8) * mm});
            skLineSegment(sketch, "E19.56.1", {"start": v(0, 0) * mm, "end": v(3.17, 6.22) * mm});
            skLineSegment(sketch, "E19.56.2", {"start": v(0, 0) * mm, "end": v(3.17, 5.5) * mm});
            skLineSegment(sketch, "E19.56.3", {"start": v(2.58, 5.8) * mm, "end": v(3.17, 6.22) * mm});
            skArc(sketch, "E19.56.4", {"start": v(3.17, 5.5) * mm, "mid": v(2.88, 5.66) * mm, "end": v(2.58, 5.8) * mm});
            skLineSegment(sketch, "E19.56.5", {"start": v(3.17, 5.5) * mm, "end": v(3.17, 6.22) * mm});
            skLineSegment(sketch, "E19.57.0", {"start": v(0, 0) * mm, "end": v(1.96, 6.04) * mm});
            skLineSegment(sketch, "E19.57.1", {"start": v(0, 0) * mm, "end": v(2.5, 6.52) * mm});
            skLineSegment(sketch, "E19.57.2", {"start": v(0, 0) * mm, "end": v(2.58, 5.8) * mm});
            skLineSegment(sketch, "E19.57.3", {"start": v(1.96, 6.04) * mm, "end": v(2.5, 6.52) * mm});
            skArc(sketch, "E19.57.4", {"start": v(2.58, 5.8) * mm, "mid": v(2.28, 5.93) * mm, "end": v(1.96, 6.04) * mm});
            skLineSegment(sketch, "E19.57.5", {"start": v(2.58, 5.8) * mm, "end": v(2.5, 6.52) * mm});
            skLineSegment(sketch, "E19.58.0", {"start": v(0, 0) * mm, "end": v(1.32, 6.21) * mm});
            skLineSegment(sketch, "E19.58.1", {"start": v(0, 0) * mm, "end": v(1.8, 6.75) * mm});
            skLineSegment(sketch, "E19.58.2", {"start": v(0, 0) * mm, "end": v(1.96, 6.04) * mm});
            skLineSegment(sketch, "E19.58.3", {"start": v(1.32, 6.21) * mm, "end": v(1.8, 6.75) * mm});
            skArc(sketch, "E19.58.4", {"start": v(1.96, 6.04) * mm, "mid": v(1.64, 6.13) * mm, "end": v(1.32, 6.21) * mm});
            skLineSegment(sketch, "E19.58.5", {"start": v(1.96, 6.04) * mm, "end": v(1.8, 6.75) * mm});
            skLineSegment(sketch, "E19.59.1", {"start": v(0, 0) * mm, "end": v(1.1, 6.9) * mm});
            skLineSegment(sketch, "E19.59.2", {"start": v(0, 0) * mm, "end": v(1.32, 6.21) * mm});
            skLineSegment(sketch, "E19.59.3", {"start": v(0.66, 6.32) * mm, "end": v(1.1, 6.9) * mm});
            skArc(sketch, "E19.59.4", {"start": v(1.32, 6.21) * mm, "mid": v(1, 6.27) * mm, "end": v(0.66, 6.32) * mm});
            skLineSegment(sketch, "E19.59.5", {"start": v(1.32, 6.21) * mm, "end": v(1.1, 6.9) * mm});
            skSolve(sketch);
        }
        {
            var Q0;
            Q0 = qSketchRegion(id + "F12", true);
            extrude(context, id + "F13", {"entities" : qUnion([Q0]), "operationType" : NewBodyOperationType.ADD, "depth" : 25.4 * mm, "offsetDistance" : 25.4 * mm});
        }
        {
            var Q0;
            Q0=makeQuery(id+"F13.opExtrude","CAP_FACE",FACE,{"disambiguationData":[OSD([sQuery(id+"F12.wireOp",EDGE,"E17"),sQuery(id+"F12.wireOp",EDGE,"E18"),sQuery(id+"F12.wireOp",EDGE,"E19.1.3"),sQuery(id+"F12.wireOp",EDGE,"E19.1.5"),sQuery(id+"F12.wireOp",EDGE,"E19.2.3"),sQuery(id+"F12.wireOp",EDGE,"E19.2.5"),sQuery(id+"F12.wireOp",EDGE,"E19.3.3"),sQuery(id+"F12.wireOp",EDGE,"E19.3.5"),sQuery(id+"F12.wireOp",EDGE,"E19.4.3"),sQuery(id+"F12.wireOp",EDGE,"E19.4.5"),sQuery(id+"F12.wireOp",EDGE,"E19.5.3"),sQuery(id+"F12.wireOp",EDGE,"E19.5.5"),sQuery(id+"F12.wireOp",EDGE,"E19.6.3"),sQuery(id+"F12.wireOp",EDGE,"E19.6.5"),sQuery(id+"F12.wireOp",EDGE,"E19.7.3"),sQuery(id+"F12.wireOp",EDGE,"E19.7.5"),sQuery(id+"F12.wireOp",EDGE,"E19.8.3"),sQuery(id+"F12.wireOp",EDGE,"E19.8.5"),sQuery(id+"F12.wireOp",EDGE,"E19.9.3"),sQuery(id+"F12.wireOp",EDGE,"E19.9.5"),sQuery(id+"F12.wireOp",EDGE,"E19.10.3"),sQuery(id+"F12.wireOp",EDGE,"E19.10.5"),sQuery(id+"F12.wireOp",EDGE,"E19.11.3"),sQuery(id+"F12.wireOp",EDGE,"E19.11.5"),sQuery(id+"F12.wireOp",EDGE,"E19.12.3"),sQuery(id+"F12.wireOp",EDGE,"E19.12.5"),sQuery(id+"F12.wireOp",EDGE,"E19.13.3"),sQuery(id+"F12.wireOp",EDGE,"E19.13.5"),sQuery(id+"F12.wireOp",EDGE,"E19.14.3"),sQuery(id+"F12.wireOp",EDGE,"E19.14.5"),sQuery(id+"F12.wireOp",EDGE,"E19.15.3"),sQuery(id+"F12.wireOp",EDGE,"E19.15.5"),sQuery(id+"F12.wireOp",EDGE,"E19.16.3"),sQuery(id+"F12.wireOp",EDGE,"E19.16.5"),sQuery(id+"F12.wireOp",EDGE,"E19.17.3"),sQuery(id+"F12.wireOp",EDGE,"E19.17.5"),sQuery(id+"F12.wireOp",EDGE,"E19.18.3"),sQuery(id+"F12.wireOp",EDGE,"E19.18.5"),sQuery(id+"F12.wireOp",EDGE,"E19.19.3"),sQuery(id+"F12.wireOp",EDGE,"E19.19.5"),sQuery(id+"F12.wireOp",EDGE,"E19.20.3"),sQuery(id+"F12.wireOp",EDGE,"E19.20.5"),sQuery(id+"F12.wireOp",EDGE,"E19.21.3"),sQuery(id+"F12.wireOp",EDGE,"E19.21.5"),sQuery(id+"F12.wireOp",EDGE,"E19.22.3"),sQuery(id+"F12.wireOp",EDGE,"E19.22.5"),sQuery(id+"F12.wireOp",EDGE,"E19.23.3"),sQuery(id+"F12.wireOp",EDGE,"E19.23.5"),sQuery(id+"F12.wireOp",EDGE,"E19.24.3"),sQuery(id+"F12.wireOp",EDGE,"E19.24.5"),sQuery(id+"F12.wireOp",EDGE,"E19.25.3"),sQuery(id+"F12.wireOp",EDGE,"E19.25.5"),sQuery(id+"F12.wireOp",EDGE,"E19.26.3"),sQuery(id+"F12.wireOp",EDGE,"E19.26.5"),sQuery(id+"F12.wireOp",EDGE,"E19.27.3"),sQuery(id+"F12.wireOp",EDGE,"E19.27.5"),sQuery(id+"F12.wireOp",EDGE,"E19.28.3"),sQuery(id+"F12.wireOp",EDGE,"E19.28.5"),sQuery(id+"F12.wireOp",EDGE,"E19.29.3"),sQuery(id+"F12.wireOp",EDGE,"E19.29.5"),sQuery(id+"F12.wireOp",EDGE,"E19.30.3"),sQuery(id+"F12.wireOp",EDGE,"E19.30.5"),sQuery(id+"F12.wireOp",EDGE,"E19.31.3"),sQuery(id+"F12.wireOp",EDGE,"E19.31.5"),sQuery(id+"F12.wireOp",EDGE,"E19.32.3"),sQuery(id+"F12.wireOp",EDGE,"E19.32.5"),sQuery(id+"F12.wireOp",EDGE,"E19.33.3"),sQuery(id+"F12.wireOp",EDGE,"E19.33.5"),sQuery(id+"F12.wireOp",EDGE,"E19.34.3"),sQuery(id+"F12.wireOp",EDGE,"E19.34.5"),sQuery(id+"F12.wireOp",EDGE,"E19.35.3"),sQuery(id+"F12.wireOp",EDGE,"E19.35.5"),sQuery(id+"F12.wireOp",EDGE,"E19.36.3"),sQuery(id+"F12.wireOp",EDGE,"E19.36.5"),sQuery(id+"F12.wireOp",EDGE,"E19.37.3"),sQuery(id+"F12.wireOp",EDGE,"E19.37.5"),sQuery(id+"F12.wireOp",EDGE,"E19.38.3"),sQuery(id+"F12.wireOp",EDGE,"E19.38.5"),sQuery(id+"F12.wireOp",EDGE,"E19.39.3"),sQuery(id+"F12.wireOp",EDGE,"E19.39.5"),sQuery(id+"F12.wireOp",EDGE,"E19.40.3"),sQuery(id+"F12.wireOp",EDGE,"E19.40.5"),sQuery(id+"F12.wireOp",EDGE,"E19.41.3"),sQuery(id+"F12.wireOp",EDGE,"E19.41.5"),sQuery(id+"F12.wireOp",EDGE,"E19.42.3"),sQuery(id+"F12.wireOp",EDGE,"E19.42.5"),sQuery(id+"F12.wireOp",EDGE,"E19.43.3"),sQuery(id+"F12.wireOp",EDGE,"E19.43.5"),sQuery(id+"F12.wireOp",EDGE,"E19.44.3"),sQuery(id+"F12.wireOp",EDGE,"E19.44.5"),sQuery(id+"F12.wireOp",EDGE,"E19.45.3"),sQuery(id+"F12.wireOp",EDGE,"E19.45.5"),sQuery(id+"F12.wireOp",EDGE,"E19.46.3"),sQuery(id+"F12.wireOp",EDGE,"E19.46.5"),sQuery(id+"F12.wireOp",EDGE,"E19.47.3"),sQuery(id+"F12.wireOp",EDGE,"E19.47.5"),sQuery(id+"F12.wireOp",EDGE,"E19.48.3"),sQuery(id+"F12.wireOp",EDGE,"E19.48.5"),sQuery(id+"F12.wireOp",EDGE,"E19.49.3"),sQuery(id+"F12.wireOp",EDGE,"E19.49.5"),sQuery(id+"F12.wireOp",EDGE,"E19.50.3"),sQuery(id+"F12.wireOp",EDGE,"E19.50.5"),sQuery(id+"F12.wireOp",EDGE,"E19.51.3"),sQuery(id+"F12.wireOp",EDGE,"E19.51.5"),sQuery(id+"F12.wireOp",EDGE,"E19.52.3"),sQuery(id+"F12.wireOp",EDGE,"E19.52.5"),sQuery(id+"F12.wireOp",EDGE,"E19.53.3"),sQuery(id+"F12.wireOp",EDGE,"E19.53.5"),sQuery(id+"F12.wireOp",EDGE,"E19.54.3"),sQuery(id+"F12.wireOp",EDGE,"E19.54.5"),sQuery(id+"F12.wireOp",EDGE,"E19.55.3"),sQuery(id+"F12.wireOp",EDGE,"E19.55.5"),sQuery(id+"F12.wireOp",EDGE,"E19.56.3"),sQuery(id+"F12.wireOp",EDGE,"E19.56.5"),sQuery(id+"F12.wireOp",EDGE,"E19.57.3"),sQuery(id+"F12.wireOp",EDGE,"E19.57.5"),sQuery(id+"F12.wireOp",EDGE,"E19.58.3"),sQuery(id+"F12.wireOp",EDGE,"E19.58.5"),sQuery(id+"F12.wireOp",EDGE,"E19.59.3"),sQuery(id+"F12.wireOp",EDGE,"E19.59.5")])],"isStart":false});
            chamfer(context, id + "F14", {"entities" : qUnion([Q0]), "chamferType" : ChamferType.OFFSET_ANGLE, "width" : 0.25 * mm, "oppositeDirection" : false, "angle" : 45 * degree, "tangentPropagation" : true});
        }
    });
